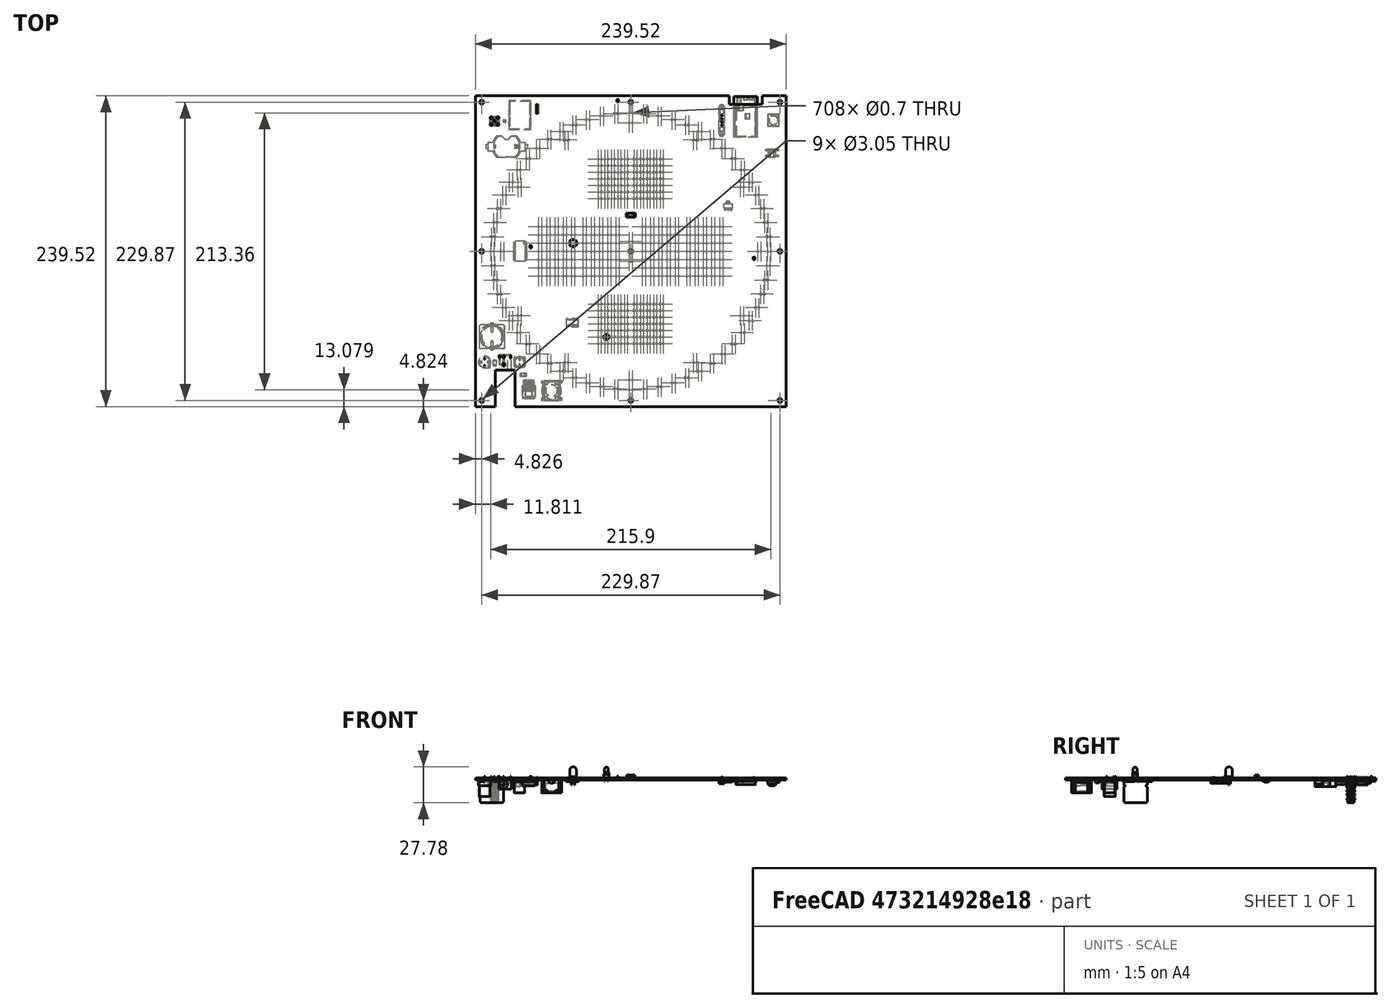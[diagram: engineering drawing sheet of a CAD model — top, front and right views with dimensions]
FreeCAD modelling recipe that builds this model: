
FCSTD DOCUMENT  (FreeCAD 0.20R29603 (Git))
Label: printed_circuit_board
License: All rights reserved
LicenseURL: http://en.wikipedia.org/wiki/All_rights_reserved
objects: App::Link×552, Part::Feature×29, App::Part×5, PartDesign::CoordinateSystem×1, Sketcher::SketchObject×1
note: 31 computed .brp shape members not serialized (recipe doc carries the construction recipe); baked Part::Feature solids carry a one-line shape summary decoded from their .brp

FEATURE [PartDesign::CoordinateSystem] Local_CS_7181
  AttacherType = Attacher::AttachEngine3D
  MapMode = 2
  Support = -> [X_Axis001]
FEATURE [Part::Feature] Pcb_7181
  Placement = pos=(-25.654,25.654,0) rot=(0,0,1;0rad)
  shape: bbox 239.5 x 239.5 x 1.6 mm, 770 faces (baked)
FEATURE [Sketcher::SketchObject] PCB_Sketch_7181
  FullyConstrained = false
  sketch-geometry (21):
    g0: LineSegment StartX=195.58 StartY=0 StartZ=0 EndX=0 EndY=0 EndZ=0
    g1: LineSegment StartX=239.522 StartY=-239.522 StartZ=0 EndX=239.522 EndY=0 EndZ=0
    g2: LineSegment StartX=0 StartY=-239.522 StartZ=0 EndX=15.24 EndY=-239.522 EndZ=0
    g3: LineSegment StartX=220.98 StartY=-6.604 StartZ=0 EndX=220.98 EndY=0 EndZ=0
    g4: LineSegment StartX=30.48 StartY=-239.522 StartZ=0 EndX=239.522 EndY=-239.522 EndZ=0
    g5: LineSegment StartX=30.48 StartY=-211.328 StartZ=0 EndX=30.48 EndY=-239.522 EndZ=0
    g6: LineSegment StartX=195.58 StartY=0 StartZ=0 EndX=195.58 EndY=-6.604 EndZ=0
    g7: LineSegment StartX=195.58 StartY=-6.604 StartZ=0 EndX=220.98 EndY=-6.604 EndZ=0
    g8: LineSegment StartX=15.24 StartY=-239.522 StartZ=0 EndX=15.24 EndY=-211.328 EndZ=0
    g9: LineSegment StartX=220.98 StartY=0 StartZ=0 EndX=239.522 EndY=0 EndZ=0
    g10: LineSegment StartX=0 StartY=0 StartZ=0 EndX=0 EndY=-239.522 EndZ=0
    g11: LineSegment StartX=15.24 StartY=-211.328 StartZ=0 EndX=30.48 EndY=-211.328 EndZ=0
    g12: Circle CenterX=234.696 CenterY=-119.761 CenterZ=0 NormalX=0 NormalY=0 NormalZ=1 AngleXU=0 Radius=1.524
    g13: Circle CenterX=234.696 CenterY=-234.696 CenterZ=0 NormalX=0 NormalY=0 NormalZ=1 AngleXU=0 Radius=1.524
    g14: Circle CenterX=4.826 CenterY=-4.826 CenterZ=0 NormalX=0 NormalY=0 NormalZ=1 AngleXU=0 Radius=1.524
    g15: Circle CenterX=234.696 CenterY=-4.826 CenterZ=0 NormalX=0 NormalY=0 NormalZ=1 AngleXU=0 Radius=1.524
    g16: Circle CenterX=119.761 CenterY=-234.696 CenterZ=0 NormalX=0 NormalY=0 NormalZ=1 AngleXU=0 Radius=1.524
    g17: Circle CenterX=119.761 CenterY=-4.826 CenterZ=0 NormalX=0 NormalY=0 NormalZ=1 AngleXU=0 Radius=1.524
    g18: Circle CenterX=119.761 CenterY=-119.761 CenterZ=0 NormalX=0 NormalY=0 NormalZ=1 AngleXU=0 Radius=1.524
    g19: Circle CenterX=4.826 CenterY=-119.761 CenterZ=0 NormalX=0 NormalY=0 NormalZ=1 AngleXU=0 Radius=1.524
    g20: Circle CenterX=4.826 CenterY=-234.696 CenterZ=0 NormalX=0 NormalY=0 NormalZ=1 AngleXU=0 Radius=1.524
  constraints (12):
    c: Coincident(g2,g10)
    c: Coincident(g0,g10)
    c: Coincident(g2,g8)
    c: Coincident(g8,g11)
    c: Coincident(g4,g5)
    c: Coincident(g5,g11)
    c: Coincident(g6,g7)
    c: Coincident(g0,g6)
    c: Coincident(g3,g7)
    c: Coincident(g3,g9)
    c: Coincident(g1,g4)
    c: Coincident(g1,g9)
FEATURE [App::Part] Board_Geoms_7181
  Group = -> [Pcb_7181,PCB_Sketch_7181]
  Origin = -> Origin
FEATURE [Part::Feature] Shape  label="${REFERENCE}_LED_D3.0mm_null"
  Placement = pos=(99.695,-185.801,0) rot=(0,0,1;0rad)
  shape: bbox 3.4 x 3.8 x 10.8 mm, 16 faces (baked)
FEATURE [Part::Feature] Shape001  label="${REFERENCE}_Body_null[2]"
  Placement = pos=(100.965,-185.801,0) rot=(0,0,1;0rad)
  shape: bbox 4 x 4 x 3 mm, 17 faces (baked)
FEATURE [App::Link] __REFERENCE__LED_D3_0mm_null_ln_  label="${REFERENCE}_LED_D3.0mm_null001"
  LinkPlacement = pos=(122.047,-190.881,0) rot=(0,0,1;0rad)
  LinkedObject = -> Shape
  Placement = pos=(122.047,-190.881,0) rot=(0,0,1;0rad)
FEATURE [App::Link] __REFERENCE__Body_null_2__ln_  label="${REFERENCE}_Body_null[2]001"
  LinkPlacement = pos=(123.317,-190.881,0) rot=(0,0,1;0rad)
  LinkedObject = -> Shape001
  Placement = pos=(123.317,-190.881,0) rot=(0,0,1;0rad)
FEATURE [Part::Feature] Shape002  label="${REFERENCE}_LED_D5.0mm_null"
  Placement = pos=(74.041,-113.411,-3) rot=(0,0,1;0rad)
  shape: bbox 5.4 x 5.8 x 14.1 mm, 16 faces (baked)
FEATURE [App::Link] __REFERENCE__LED_D5_0mm_null_ln_  label="${REFERENCE}_LED_D5.0mm_null001"
  LinkPlacement = pos=(55.7861,-33.4551,-3) rot=(0,0,1;0rad)
  LinkedObject = -> Shape002
  Placement = pos=(55.7861,-33.4551,-3) rot=(0,0,1;0rad)
FEATURE [App::Link] __REFERENCE__LED_D5_0mm_null_ln_001  label="${REFERENCE}_LED_D5.0mm_null002"
  LinkPlacement = pos=(147.701,-132.461,-3) rot=(0,0,1;0rad)
  LinkedObject = -> Shape002
  Placement = pos=(147.701,-132.461,-3) rot=(0,0,1;0rad)
FEATURE [App::Link] __REFERENCE__LED_D5_0mm_null_ln_002  label="${REFERENCE}_LED_D5.0mm_null003"
  LinkPlacement = pos=(11.811,-119.761,-3) rot=(0,0,1;0rad)
  LinkedObject = -> Shape002
  Placement = pos=(11.811,-119.761,-3) rot=(0,0,1;0rad)
FEATURE [App::Link] __REFERENCE__LED_D5_0mm_null_ln_003  label="${REFERENCE}_LED_D5.0mm_null004"
  LinkPlacement = pos=(168.021,-205.549,-3) rot=(0,0,1;0rad)
  LinkedObject = -> Shape002
  Placement = pos=(168.021,-205.549,-3) rot=(0,0,1;0rad)
FEATURE [App::Link] __REFERENCE__LED_D5_0mm_null_ln_004  label="${REFERENCE}_LED_D5.0mm_null005"
  LinkPlacement = pos=(118.491,-226.441,-3) rot=(0,0,1;0rad)
  LinkedObject = -> Shape002
  Placement = pos=(118.491,-226.441,-3) rot=(0,0,1;0rad)
FEATURE [App::Link] __REFERENCE__LED_D5_0mm_null_ln_005  label="${REFERENCE}_LED_D5.0mm_null006"
  LinkPlacement = pos=(95.631,-138.811,-3) rot=(0,0,1;0rad)
  LinkedObject = -> Shape002
  Placement = pos=(95.631,-138.811,-3) rot=(0,0,1;0rad)
FEATURE [App::Link] __REFERENCE__LED_D5_0mm_null_ln_006  label="${REFERENCE}_LED_D5.0mm_null007"
  LinkPlacement = pos=(82.931,-107.061,-3) rot=(0,0,1;0rad)
  LinkedObject = -> Shape002
  Placement = pos=(82.931,-107.061,-3) rot=(0,0,1;0rad)
FEATURE [App::Link] __REFERENCE__LED_D5_0mm_null_ln_007  label="${REFERENCE}_LED_D5.0mm_null008"
  LinkPlacement = pos=(118.491,-112.141,-3) rot=(0,0,1;0rad)
  LinkedObject = -> Shape002
  Placement = pos=(118.491,-112.141,-3) rot=(0,0,1;0rad)
FEATURE [App::Link] __REFERENCE__LED_D5_0mm_null_ln_008  label="${REFERENCE}_LED_D5.0mm_null009"
  LinkPlacement = pos=(54.991,-132.461,-3) rot=(0,0,1;0rad)
  LinkedObject = -> Shape002
  Placement = pos=(54.991,-132.461,-3) rot=(0,0,1;0rad)
FEATURE [App::Link] __REFERENCE__LED_D3_0mm_null_ln_001  label="${REFERENCE}_LED_D3.0mm_null002"
  LinkPlacement = pos=(109.855,-180.721,0) rot=(0,0,1;0rad)
  LinkedObject = -> Shape
  Placement = pos=(109.855,-180.721,0) rot=(0,0,1;0rad)
FEATURE [App::Link] __REFERENCE__Body_null_2__ln_001  label="${REFERENCE}_Body_null[2]002"
  LinkPlacement = pos=(111.125,-180.721,0) rot=(0,0,1;0rad)
  LinkedObject = -> Shape001
  Placement = pos=(111.125,-180.721,0) rot=(0,0,1;0rad)
FEATURE [App::Link] __REFERENCE__LED_D5_0mm_null_ln_009  label="${REFERENCE}_LED_D5.0mm_null010"
  LinkPlacement = pos=(161.882,-217.218,-3) rot=(0,0,1;0rad)
  LinkedObject = -> Shape002
  Placement = pos=(161.882,-217.218,-3) rot=(0,0,1;0rad)
FEATURE [App::Link] __REFERENCE__LED_D5_0mm_null_ln_010  label="${REFERENCE}_LED_D5.0mm_null011"
  LinkPlacement = pos=(82.931,-126.111,-3) rot=(0,0,1;0rad)
  LinkedObject = -> Shape002
  Placement = pos=(82.931,-126.111,-3) rot=(0,0,1;0rad)
FEATURE [App::Link] __REFERENCE__LED_D3_0mm_null_ln_002  label="${REFERENCE}_LED_D3.0mm_null003"
  LinkPlacement = pos=(137.287,-53.721,0) rot=(0,0,1;0rad)
  LinkedObject = -> Shape
  Placement = pos=(137.287,-53.721,0) rot=(0,0,1;0rad)
FEATURE [App::Link] __REFERENCE__Body_null_2__ln_002  label="${REFERENCE}_Body_null[2]003"
  LinkPlacement = pos=(138.557,-53.721,0) rot=(0,0,1;0rad)
  LinkedObject = -> Shape001
  Placement = pos=(138.557,-53.721,0) rot=(0,0,1;0rad)
FEATURE [App::Link] __REFERENCE__LED_D3_0mm_null_ln_003  label="${REFERENCE}_LED_D3.0mm_null004"
  LinkPlacement = pos=(99.695,-63.881,0) rot=(0,0,1;0rad)
  LinkedObject = -> Shape
  Placement = pos=(99.695,-63.881,0) rot=(0,0,1;0rad)
FEATURE [App::Link] __REFERENCE__Body_null_2__ln_003  label="${REFERENCE}_Body_null[2]004"
  LinkPlacement = pos=(100.965,-63.881,0) rot=(0,0,1;0rad)
  LinkedObject = -> Shape001
  Placement = pos=(100.965,-63.881,0) rot=(0,0,1;0rad)
FEATURE [App::Link] __REFERENCE__LED_D5_0mm_null_ln_011  label="${REFERENCE}_LED_D5.0mm_null012"
  LinkPlacement = pos=(82.931,-113.411,-3) rot=(0,0,1;0rad)
  LinkedObject = -> Shape002
  Placement = pos=(82.931,-113.411,-3) rot=(0,0,1;0rad)
FEATURE [App::Link] __REFERENCE__LED_D5_0mm_null_ln_012  label="${REFERENCE}_LED_D5.0mm_null013"
  LinkPlacement = pos=(67.691,-132.461,-3) rot=(0,0,1;0rad)
  LinkedObject = -> Shape002
  Placement = pos=(67.691,-132.461,-3) rot=(0,0,1;0rad)
FEATURE [App::Link] __REFERENCE__LED_D5_0mm_null_ln_013  label="${REFERENCE}_LED_D5.0mm_null014"
  LinkPlacement = pos=(181.991,-100.711,-3) rot=(0,0,1;0rad)
  LinkedObject = -> Shape002
  Placement = pos=(181.991,-100.711,-3) rot=(0,0,1;0rad)
FEATURE [App::Link] __REFERENCE__LED_D5_0mm_null_ln_014  label="${REFERENCE}_LED_D5.0mm_null015"
  LinkPlacement = pos=(154.051,-138.811,-3) rot=(0,0,1;0rad)
  LinkedObject = -> Shape002
  Placement = pos=(154.051,-138.811,-3) rot=(0,0,1;0rad)
FEATURE [App::Link] __REFERENCE__LED_D5_0mm_null_ln_015  label="${REFERENCE}_LED_D5.0mm_null016"
  LinkPlacement = pos=(82.931,-119.761,-3) rot=(0,0,1;0rad)
  LinkedObject = -> Shape002
  Placement = pos=(82.931,-119.761,-3) rot=(0,0,1;0rad)
FEATURE [App::Link] __REFERENCE__LED_D5_0mm_null_ln_016  label="${REFERENCE}_LED_D5.0mm_null017"
  LinkPlacement = pos=(129.642,-13.6654,-3) rot=(0,0,1;0rad)
  LinkedObject = -> Shape002
  Placement = pos=(129.642,-13.6654,-3) rot=(0,0,1;0rad)
FEATURE [Part::Feature] Shape003  label="${REFERENCE}_R_0805_2012Metric_null"
  Placement = pos=(214.757,-125.222,0) rot=(0,0,1;1.5708rad)
  shape: bbox 1.2 x 2 x 0.45 mm, 26 faces (baked)
FEATURE [App::Link] __REFERENCE__LED_D5_0mm_null_ln_017  label="${REFERENCE}_LED_D5.0mm_null018"
  LinkPlacement = pos=(108.331,-113.411,-3) rot=(0,0,1;0rad)
  LinkedObject = -> Shape002
  Placement = pos=(108.331,-113.411,-3) rot=(0,0,1;0rad)
FEATURE [App::Link] __REFERENCE__LED_D5_0mm_null_ln_018  label="${REFERENCE}_LED_D5.0mm_null019"
  LinkPlacement = pos=(108.331,-119.761,-3) rot=(0,0,1;0rad)
  LinkedObject = -> Shape002
  Placement = pos=(108.331,-119.761,-3) rot=(0,0,1;0rad)
FEATURE [App::Link] __REFERENCE__LED_D5_0mm_null_ln_019  label="${REFERENCE}_LED_D5.0mm_null020"
  LinkPlacement = pos=(54.991,-113.411,-3) rot=(0,0,1;0rad)
  LinkedObject = -> Shape002
  Placement = pos=(54.991,-113.411,-3) rot=(0,0,1;0rad)
FEATURE [App::Link] __REFERENCE__LED_D3_0mm_null_ln_004  label="${REFERENCE}_LED_D3.0mm_null005"
  LinkPlacement = pos=(127.127,-58.801,0) rot=(0,0,1;0rad)
  LinkedObject = -> Shape
  Placement = pos=(127.127,-58.801,0) rot=(0,0,1;0rad)
FEATURE [App::Link] __REFERENCE__Body_null_2__ln_004  label="${REFERENCE}_Body_null[2]005"
  LinkPlacement = pos=(128.397,-58.801,0) rot=(0,0,1;0rad)
  LinkedObject = -> Shape001
  Placement = pos=(128.397,-58.801,0) rot=(0,0,1;0rad)
FEATURE [App::Link] __REFERENCE__LED_D5_0mm_null_ln_020  label="${REFERENCE}_LED_D5.0mm_null021"
  LinkPlacement = pos=(21.034,-163.152,-3) rot=(0,0,1;0rad)
  LinkedObject = -> Shape002
  Placement = pos=(21.034,-163.152,-3) rot=(0,0,1;0rad)
FEATURE [App::Link] __REFERENCE__LED_D3_0mm_null_ln_005  label="${REFERENCE}_LED_D3.0mm_null006"
  LinkPlacement = pos=(109.855,-74.041,0) rot=(0,0,1;0rad)
  LinkedObject = -> Shape
  Placement = pos=(109.855,-74.041,0) rot=(0,0,1;0rad)
FEATURE [App::Link] __REFERENCE__Body_null_2__ln_005  label="${REFERENCE}_Body_null[2]006"
  LinkPlacement = pos=(111.125,-74.041,0) rot=(0,0,1;0rad)
  LinkedObject = -> Shape001
  Placement = pos=(111.125,-74.041,0) rot=(0,0,1;0rad)
FEATURE [App::Link] __REFERENCE__LED_D5_0mm_null_ln_021  label="${REFERENCE}_LED_D5.0mm_null022"
  LinkPlacement = pos=(108.331,-132.461,-3) rot=(0,0,1;0rad)
  LinkedObject = -> Shape002
  Placement = pos=(108.331,-132.461,-3) rot=(0,0,1;0rad)
FEATURE [App::Link] __REFERENCE__LED_D3_0mm_null_ln_006  label="${REFERENCE}_LED_D3.0mm_null007"
  LinkPlacement = pos=(104.775,-79.121,0) rot=(0,0,1;0rad)
  LinkedObject = -> Shape
  Placement = pos=(104.775,-79.121,0) rot=(0,0,1;0rad)
FEATURE [App::Link] __REFERENCE__Body_null_2__ln_006  label="${REFERENCE}_Body_null[2]007"
  LinkPlacement = pos=(106.045,-79.121,0) rot=(0,0,1;0rad)
  LinkedObject = -> Shape001
  Placement = pos=(106.045,-79.121,0) rot=(0,0,1;0rad)
FEATURE [App::Link] __REFERENCE__LED_D3_0mm_null_ln_007  label="${REFERENCE}_LED_D3.0mm_null008"
  LinkPlacement = pos=(94.615,-48.641,0) rot=(0,0,1;0rad)
  LinkedObject = -> Shape
  Placement = pos=(94.615,-48.641,0) rot=(0,0,1;0rad)
FEATURE [App::Link] __REFERENCE__Body_null_2__ln_007  label="${REFERENCE}_Body_null[2]008"
  LinkPlacement = pos=(95.885,-48.641,0) rot=(0,0,1;0rad)
  LinkedObject = -> Shape001
  Placement = pos=(95.885,-48.641,0) rot=(0,0,1;0rad)
FEATURE [App::Link] __REFERENCE__LED_D3_0mm_null_ln_008  label="${REFERENCE}_LED_D3.0mm_null009"
  LinkPlacement = pos=(94.615,-190.881,0) rot=(0,0,1;0rad)
  LinkedObject = -> Shape
  Placement = pos=(94.615,-190.881,0) rot=(0,0,1;0rad)
FEATURE [App::Link] __REFERENCE__Body_null_2__ln_008  label="${REFERENCE}_Body_null[2]009"
  LinkPlacement = pos=(95.885,-190.881,0) rot=(0,0,1;0rad)
  LinkedObject = -> Shape001
  Placement = pos=(95.885,-190.881,0) rot=(0,0,1;0rad)
FEATURE [App::Link] __REFERENCE__LED_D5_0mm_null_ln_022  label="${REFERENCE}_LED_D5.0mm_null023"
  LinkPlacement = pos=(96.311,-15.4122,-3) rot=(0,0,1;0rad)
  LinkedObject = -> Shape002
  Placement = pos=(96.311,-15.4122,-3) rot=(0,0,1;0rad)
FEATURE [App::Link] __REFERENCE__LED_D5_0mm_null_ln_023  label="${REFERENCE}_LED_D5.0mm_null024"
  LinkPlacement = pos=(32.1851,-182.466,-3) rot=(0,0,1;0rad)
  LinkedObject = -> Shape002
  Placement = pos=(32.1851,-182.466,-3) rot=(0,0,1;0rad)
FEATURE [App::Link] __REFERENCE__LED_D5_0mm_null_ln_024  label="${REFERENCE}_LED_D5.0mm_null025"
  LinkPlacement = pos=(128.651,-100.711,-3) rot=(0,0,1;0rad)
  LinkedObject = -> Shape002
  Placement = pos=(128.651,-100.711,-3) rot=(0,0,1;0rad)
FEATURE [App::Link] __REFERENCE__LED_D5_0mm_null_ln_025  label="${REFERENCE}_LED_D5.0mm_null026"
  LinkPlacement = pos=(140.671,-224.11,-3) rot=(0,0,1;0rad)
  LinkedObject = -> Shape002
  Placement = pos=(140.671,-224.11,-3) rot=(0,0,1;0rad)
FEATURE [App::Link] __REFERENCE__LED_D3_0mm_null_ln_009  label="${REFERENCE}_LED_D3.0mm_null010"
  LinkPlacement = pos=(99.695,-53.721,0) rot=(0,0,1;0rad)
  LinkedObject = -> Shape
  Placement = pos=(99.695,-53.721,0) rot=(0,0,1;0rad)
FEATURE [App::Link] __REFERENCE__Body_null_2__ln_009  label="${REFERENCE}_Body_null[2]010"
  LinkPlacement = pos=(100.965,-53.721,0) rot=(0,0,1;0rad)
  LinkedObject = -> Shape001
  Placement = pos=(100.965,-53.721,0) rot=(0,0,1;0rad)
FEATURE [App::Link] __REFERENCE__LED_D3_0mm_null_ln_010  label="${REFERENCE}_LED_D3.0mm_null011"
  LinkPlacement = pos=(132.207,-175.641,0) rot=(0,0,1;0rad)
  LinkedObject = -> Shape
  Placement = pos=(132.207,-175.641,0) rot=(0,0,1;0rad)
FEATURE [App::Link] __REFERENCE__Body_null_2__ln_010  label="${REFERENCE}_Body_null[2]011"
  LinkPlacement = pos=(133.477,-175.641,0) rot=(0,0,1;0rad)
  LinkedObject = -> Shape001
  Placement = pos=(133.477,-175.641,0) rot=(0,0,1;0rad)
FEATURE [App::Link] __REFERENCE__LED_D5_0mm_null_ln_026  label="${REFERENCE}_LED_D5.0mm_null027"
  LinkPlacement = pos=(89.281,-132.461,-3) rot=(0,0,1;0rad)
  LinkedObject = -> Shape002
  Placement = pos=(89.281,-132.461,-3) rot=(0,0,1;0rad)
FEATURE [App::Link] __REFERENCE__LED_D5_0mm_null_ln_027  label="${REFERENCE}_LED_D5.0mm_null028"
  LinkPlacement = pos=(55.7861,-206.067,-3) rot=(0,0,1;0rad)
  LinkedObject = -> Shape002
  Placement = pos=(55.7861,-206.067,-3) rot=(0,0,1;0rad)
FEATURE [App::Link] __REFERENCE__LED_D3_0mm_null_ln_011  label="${REFERENCE}_LED_D3.0mm_null012"
  LinkPlacement = pos=(122.047,-79.121,0) rot=(0,0,1;0rad)
  LinkedObject = -> Shape
  Placement = pos=(122.047,-79.121,0) rot=(0,0,1;0rad)
FEATURE [App::Link] __REFERENCE__Body_null_2__ln_011  label="${REFERENCE}_Body_null[2]012"
  LinkPlacement = pos=(123.317,-79.121,0) rot=(0,0,1;0rad)
  LinkedObject = -> Shape001
  Placement = pos=(123.317,-79.121,0) rot=(0,0,1;0rad)
FEATURE [App::Link] __REFERENCE__LED_D5_0mm_null_ln_028  label="${REFERENCE}_LED_D5.0mm_null029"
  LinkPlacement = pos=(67.691,-100.711,-3) rot=(0,0,1;0rad)
  LinkedObject = -> Shape002
  Placement = pos=(67.691,-100.711,-3) rot=(0,0,1;0rad)
FEATURE [App::Link] __REFERENCE__LED_D5_0mm_null_ln_029  label="${REFERENCE}_LED_D5.0mm_null030"
  LinkPlacement = pos=(54.991,-100.711,-3) rot=(0,0,1;0rad)
  LinkedObject = -> Shape002
  Placement = pos=(54.991,-100.711,-3) rot=(0,0,1;0rad)
FEATURE [App::Link] __REFERENCE__LED_D5_0mm_null_ln_030  label="${REFERENCE}_LED_D5.0mm_null031"
  LinkPlacement = pos=(89.281,-113.411,-3) rot=(0,0,1;0rad)
  LinkedObject = -> Shape002
  Placement = pos=(89.281,-113.411,-3) rot=(0,0,1;0rad)
FEATURE [App::Link] __REFERENCE__LED_D3_0mm_null_ln_012  label="${REFERENCE}_LED_D3.0mm_null013"
  LinkPlacement = pos=(142.367,-160.401,0) rot=(0,0,1;0rad)
  LinkedObject = -> Shape
  Placement = pos=(142.367,-160.401,0) rot=(0,0,1;0rad)
FEATURE [App::Link] __REFERENCE__Body_null_2__ln_012  label="${REFERENCE}_Body_null[2]013"
  LinkPlacement = pos=(143.637,-160.401,0) rot=(0,0,1;0rad)
  LinkedObject = -> Shape001
  Placement = pos=(143.637,-160.401,0) rot=(0,0,1;0rad)
FEATURE [Part::Feature] Shape004  label="${REFERENCE}_C_0805_2012Metric_null"
  Placement = pos=(42.545,-116.332,0) rot=(0,0,-1;1.5708rad)
  shape: bbox 1.25 x 2 x 1.25 mm, 28 faces (baked)
FEATURE [App::Link] __REFERENCE__LED_D5_0mm_null_ln_031  label="${REFERENCE}_LED_D5.0mm_null032"
  LinkPlacement = pos=(95.631,-126.111,-3) rot=(0,0,1;0rad)
  LinkedObject = -> Shape002
  Placement = pos=(95.631,-126.111,-3) rot=(0,0,1;0rad)
FEATURE [App::Link] __REFERENCE__LED_D3_0mm_null_ln_013  label="${REFERENCE}_LED_D3.0mm_null014"
  LinkPlacement = pos=(142.367,-170.561,0) rot=(0,0,1;0rad)
  LinkedObject = -> Shape
  Placement = pos=(142.367,-170.561,0) rot=(0,0,1;0rad)
FEATURE [App::Link] __REFERENCE__Body_null_2__ln_013  label="${REFERENCE}_Body_null[2]014"
  LinkPlacement = pos=(143.637,-170.561,0) rot=(0,0,1;0rad)
  LinkedObject = -> Shape001
  Placement = pos=(143.637,-170.561,0) rot=(0,0,1;0rad)
FEATURE [App::Link] __REFERENCE__LED_D3_0mm_null_ln_014  label="${REFERENCE}_LED_D3.0mm_null015"
  LinkPlacement = pos=(94.615,-53.721,0) rot=(0,0,1;0rad)
  LinkedObject = -> Shape
  Placement = pos=(94.615,-53.721,0) rot=(0,0,1;0rad)
FEATURE [App::Link] __REFERENCE__Body_null_2__ln_014  label="${REFERENCE}_Body_null[2]015"
  LinkPlacement = pos=(95.885,-53.721,0) rot=(0,0,1;0rad)
  LinkedObject = -> Shape001
  Placement = pos=(95.885,-53.721,0) rot=(0,0,1;0rad)
FEATURE [App::Link] __REFERENCE__LED_D5_0mm_null_ln_032  label="${REFERENCE}_LED_D5.0mm_null033"
  LinkPlacement = pos=(12.3954,-108.61,-3) rot=(0,0,1;0rad)
  LinkedObject = -> Shape002
  Placement = pos=(12.3954,-108.61,-3) rot=(0,0,1;0rad)
FEATURE [App::Link] __REFERENCE__LED_D5_0mm_null_ln_033  label="${REFERENCE}_LED_D5.0mm_null034"
  LinkPlacement = pos=(54.991,-119.761,-3) rot=(0,0,1;0rad)
  LinkedObject = -> Shape002
  Placement = pos=(54.991,-119.761,-3) rot=(0,0,1;0rad)
FEATURE [App::Link] __REFERENCE__LED_D5_0mm_null_ln_034  label="${REFERENCE}_LED_D5.0mm_null035"
  LinkPlacement = pos=(154.051,-107.061,-3) rot=(0,0,1;0rad)
  LinkedObject = -> Shape002
  Placement = pos=(154.051,-107.061,-3) rot=(0,0,1;0rad)
FEATURE [App::Link] __REFERENCE__LED_D3_0mm_null_ln_015  label="${REFERENCE}_LED_D3.0mm_null016"
  LinkPlacement = pos=(94.615,-63.881,0) rot=(0,0,1;0rad)
  LinkedObject = -> Shape
  Placement = pos=(94.615,-63.881,0) rot=(0,0,1;0rad)
FEATURE [App::Link] __REFERENCE__Body_null_2__ln_015  label="${REFERENCE}_Body_null[2]016"
  LinkPlacement = pos=(95.885,-63.881,0) rot=(0,0,1;0rad)
  LinkedObject = -> Shape001
  Placement = pos=(95.885,-63.881,0) rot=(0,0,1;0rad)
FEATURE [App::Link] __REFERENCE__LED_D3_0mm_null_ln_016  label="${REFERENCE}_LED_D3.0mm_null017"
  LinkPlacement = pos=(122.047,-48.641,0) rot=(0,0,1;0rad)
  LinkedObject = -> Shape
  Placement = pos=(122.047,-48.641,0) rot=(0,0,1;0rad)
FEATURE [App::Link] __REFERENCE__Body_null_2__ln_016  label="${REFERENCE}_Body_null[2]017"
  LinkPlacement = pos=(123.317,-48.641,0) rot=(0,0,1;0rad)
  LinkedObject = -> Shape001
  Placement = pos=(123.317,-48.641,0) rot=(0,0,1;0rad)
FEATURE [App::Link] __REFERENCE__LED_D5_0mm_null_ln_035  label="${REFERENCE}_LED_D5.0mm_null036"
  LinkPlacement = pos=(161.882,-22.304,-3) rot=(0,0,1;0rad)
  LinkedObject = -> Shape002
  Placement = pos=(161.882,-22.304,-3) rot=(0,0,1;0rad)
FEATURE [App::Link] __REFERENCE__LED_D3_0mm_null_ln_017  label="${REFERENCE}_LED_D3.0mm_null018"
  LinkPlacement = pos=(132.207,-53.721,0) rot=(0,0,1;0rad)
  LinkedObject = -> Shape
  Placement = pos=(132.207,-53.721,0) rot=(0,0,1;0rad)
FEATURE [App::Link] __REFERENCE__Body_null_2__ln_017  label="${REFERENCE}_Body_null[2]018"
  LinkPlacement = pos=(133.477,-53.721,0) rot=(0,0,1;0rad)
  LinkedObject = -> Shape001
  Placement = pos=(133.477,-53.721,0) rot=(0,0,1;0rad)
FEATURE [App::Link] __REFERENCE__LED_D3_0mm_null_ln_018  label="${REFERENCE}_LED_D3.0mm_null019"
  LinkPlacement = pos=(114.935,-58.801,0) rot=(0,0,1;0rad)
  LinkedObject = -> Shape
  Placement = pos=(114.935,-58.801,0) rot=(0,0,1;0rad)
FEATURE [App::Link] __REFERENCE__Body_null_2__ln_018  label="${REFERENCE}_Body_null[2]019"
  LinkPlacement = pos=(116.205,-58.801,0) rot=(0,0,1;0rad)
  LinkedObject = -> Shape001
  Placement = pos=(116.205,-58.801,0) rot=(0,0,1;0rad)
FEATURE [App::Link] __REFERENCE__LED_D5_0mm_null_ln_036  label="${REFERENCE}_LED_D5.0mm_null037"
  LinkPlacement = pos=(26.1034,-173.101,-3) rot=(0,0,1;0rad)
  LinkedObject = -> Shape002
  Placement = pos=(26.1034,-173.101,-3) rot=(0,0,1;0rad)
FEATURE [App::Link] __REFERENCE__LED_D3_0mm_null_ln_019  label="${REFERENCE}_LED_D3.0mm_null020"
  LinkPlacement = pos=(94.615,-170.561,0) rot=(0,0,1;0rad)
  LinkedObject = -> Shape
  Placement = pos=(94.615,-170.561,0) rot=(0,0,1;0rad)
FEATURE [App::Link] __REFERENCE__Body_null_2__ln_019  label="${REFERENCE}_Body_null[2]020"
  LinkPlacement = pos=(95.885,-170.561,0) rot=(0,0,1;0rad)
  LinkedObject = -> Shape001
  Placement = pos=(95.885,-170.561,0) rot=(0,0,1;0rad)
FEATURE [App::Link] __REFERENCE__R_0805_2012Metric_null_ln_  label="${REFERENCE}_R_0805_2012Metric_null001"
  LinkPlacement = pos=(212.471,-125.222,0) rot=(0,0,-1;1.5708rad)
  LinkedObject = -> Shape003
  Placement = pos=(212.471,-125.222,0) rot=(0,0,-1;1.5708rad)
FEATURE [App::Link] __REFERENCE__LED_D3_0mm_null_ln_020  label="${REFERENCE}_LED_D3.0mm_null021"
  LinkPlacement = pos=(142.367,-58.801,0) rot=(0,0,1;0rad)
  LinkedObject = -> Shape
  Placement = pos=(142.367,-58.801,0) rot=(0,0,1;0rad)
FEATURE [App::Link] __REFERENCE__Body_null_2__ln_020  label="${REFERENCE}_Body_null[2]021"
  LinkPlacement = pos=(143.637,-58.801,0) rot=(0,0,1;0rad)
  LinkedObject = -> Shape001
  Placement = pos=(143.637,-58.801,0) rot=(0,0,1;0rad)
FEATURE [App::Link] __REFERENCE__R_0805_2012Metric_null_ln_001  label="${REFERENCE}_R_0805_2012Metric_null002"
  LinkPlacement = pos=(212.09,-19.558,0) rot=(0,0,1;1.5708rad)
  LinkedObject = -> Shape003
  Placement = pos=(212.09,-19.558,0) rot=(0,0,1;1.5708rad)
FEATURE [App::Link] __REFERENCE__LED_D5_0mm_null_ln_037  label="${REFERENCE}_LED_D5.0mm_null038"
  LinkPlacement = pos=(175.641,-100.711,-3) rot=(0,0,1;0rad)
  LinkedObject = -> Shape002
  Placement = pos=(175.641,-100.711,-3) rot=(0,0,1;0rad)
FEATURE [App::Link] __REFERENCE__LED_D5_0mm_null_ln_038  label="${REFERENCE}_LED_D5.0mm_null039"
  LinkPlacement = pos=(48.641,-138.811,-3) rot=(0,0,1;0rad)
  LinkedObject = -> Shape002
  Placement = pos=(48.641,-138.811,-3) rot=(0,0,1;0rad)
FEATURE [App::Link] __REFERENCE__LED_D5_0mm_null_ln_039  label="${REFERENCE}_LED_D5.0mm_null040"
  LinkPlacement = pos=(129.642,-225.857,-3) rot=(0,0,1;0rad)
  LinkedObject = -> Shape002
  Placement = pos=(129.642,-225.857,-3) rot=(0,0,1;0rad)
FEATURE [App::Link] __REFERENCE__LED_D5_0mm_null_ln_040  label="${REFERENCE}_LED_D5.0mm_null041"
  LinkPlacement = pos=(82.931,-138.811,-3) rot=(0,0,1;0rad)
  LinkedObject = -> Shape002
  Placement = pos=(82.931,-138.811,-3) rot=(0,0,1;0rad)
FEATURE [App::Link] __REFERENCE__LED_D3_0mm_null_ln_021  label="${REFERENCE}_LED_D3.0mm_null022"
  LinkPlacement = pos=(137.287,-79.121,0) rot=(0,0,1;0rad)
  LinkedObject = -> Shape
  Placement = pos=(137.287,-79.121,0) rot=(0,0,1;0rad)
FEATURE [App::Link] __REFERENCE__Body_null_2__ln_021  label="${REFERENCE}_Body_null[2]022"
  LinkPlacement = pos=(138.557,-79.121,0) rot=(0,0,1;0rad)
  LinkedObject = -> Shape001
  Placement = pos=(138.557,-79.121,0) rot=(0,0,1;0rad)
FEATURE [App::Link] __REFERENCE__LED_D5_0mm_null_ln_041  label="${REFERENCE}_LED_D5.0mm_null042"
  LinkPlacement = pos=(181.991,-138.811,-3) rot=(0,0,1;0rad)
  LinkedObject = -> Shape002
  Placement = pos=(181.991,-138.811,-3) rot=(0,0,1;0rad)
FEATURE [App::Link] __REFERENCE__LED_D5_0mm_null_ln_042  label="${REFERENCE}_LED_D5.0mm_null043"
  LinkPlacement = pos=(210.879,-173.101,-3) rot=(0,0,1;0rad)
  LinkedObject = -> Shape002
  Placement = pos=(210.879,-173.101,-3) rot=(0,0,1;0rad)
FEATURE [App::Link] __REFERENCE__LED_D5_0mm_null_ln_043  label="${REFERENCE}_LED_D5.0mm_null044"
  LinkPlacement = pos=(108.331,-100.711,-3) rot=(0,0,1;0rad)
  LinkedObject = -> Shape002
  Placement = pos=(108.331,-100.711,-3) rot=(0,0,1;0rad)
FEATURE [App::Link] __REFERENCE__LED_D3_0mm_null_ln_022  label="${REFERENCE}_LED_D3.0mm_null023"
  LinkPlacement = pos=(109.855,-185.801,0) rot=(0,0,1;0rad)
  LinkedObject = -> Shape
  Placement = pos=(109.855,-185.801,0) rot=(0,0,1;0rad)
FEATURE [App::Link] __REFERENCE__Body_null_2__ln_022  label="${REFERENCE}_Body_null[2]023"
  LinkPlacement = pos=(111.125,-185.801,0) rot=(0,0,1;0rad)
  LinkedObject = -> Shape001
  Placement = pos=(111.125,-185.801,0) rot=(0,0,1;0rad)
FEATURE [App::Link] __REFERENCE__LED_D3_0mm_null_ln_023  label="${REFERENCE}_LED_D3.0mm_null024"
  LinkPlacement = pos=(109.855,-53.721,0) rot=(0,0,1;0rad)
  LinkedObject = -> Shape
  Placement = pos=(109.855,-53.721,0) rot=(0,0,1;0rad)
FEATURE [App::Link] __REFERENCE__Body_null_2__ln_023  label="${REFERENCE}_Body_null[2]024"
  LinkPlacement = pos=(111.125,-53.721,0) rot=(0,0,1;0rad)
  LinkedObject = -> Shape001
  Placement = pos=(111.125,-53.721,0) rot=(0,0,1;0rad)
FEATURE [App::Link] __REFERENCE__LED_D5_0mm_null_ln_044  label="${REFERENCE}_LED_D5.0mm_null045"
  LinkPlacement = pos=(61.341,-126.111,-3) rot=(0,0,1;0rad)
  LinkedObject = -> Shape002
  Placement = pos=(61.341,-126.111,-3) rot=(0,0,1;0rad)
FEATURE [App::Link] __REFERENCE__LED_D5_0mm_null_ln_045  label="${REFERENCE}_LED_D5.0mm_null046"
  LinkPlacement = pos=(141.351,-138.811,-3) rot=(0,0,1;0rad)
  LinkedObject = -> Shape002
  Placement = pos=(141.351,-138.811,-3) rot=(0,0,1;0rad)
FEATURE [App::Link] __REFERENCE__R_0805_2012Metric_null_ln_002  label="${REFERENCE}_R_0805_2012Metric_null003"
  LinkPlacement = pos=(160.274,-169.672,0) rot=(0,0,1;3.14159rad)
  LinkedObject = -> Shape003
  Placement = pos=(160.274,-169.672,0) rot=(0,0,1;3.14159rad)
FEATURE [App::Link] __REFERENCE__LED_D3_0mm_null_ln_024  label="${REFERENCE}_LED_D3.0mm_null025"
  LinkPlacement = pos=(104.775,-160.401,0) rot=(0,0,1;0rad)
  LinkedObject = -> Shape
  Placement = pos=(104.775,-160.401,0) rot=(0,0,1;0rad)
FEATURE [App::Link] __REFERENCE__Body_null_2__ln_024  label="${REFERENCE}_Body_null[2]025"
  LinkPlacement = pos=(106.045,-160.401,0) rot=(0,0,1;0rad)
  LinkedObject = -> Shape001
  Placement = pos=(106.045,-160.401,0) rot=(0,0,1;0rad)
FEATURE [App::Link] __REFERENCE__LED_D3_0mm_null_ln_025  label="${REFERENCE}_LED_D3.0mm_null026"
  LinkPlacement = pos=(132.207,-165.481,0) rot=(0,0,1;0rad)
  LinkedObject = -> Shape
  Placement = pos=(132.207,-165.481,0) rot=(0,0,1;0rad)
FEATURE [App::Link] __REFERENCE__Body_null_2__ln_025  label="${REFERENCE}_Body_null[2]026"
  LinkPlacement = pos=(133.477,-165.481,0) rot=(0,0,1;0rad)
  LinkedObject = -> Shape001
  Placement = pos=(133.477,-165.481,0) rot=(0,0,1;0rad)
FEATURE [App::Link] __REFERENCE__LED_D3_0mm_null_ln_026  label="${REFERENCE}_LED_D3.0mm_null027"
  LinkPlacement = pos=(132.207,-79.121,0) rot=(0,0,1;0rad)
  LinkedObject = -> Shape
  Placement = pos=(132.207,-79.121,0) rot=(0,0,1;0rad)
FEATURE [App::Link] __REFERENCE__Body_null_2__ln_026  label="${REFERENCE}_Body_null[2]027"
  LinkPlacement = pos=(133.477,-79.121,0) rot=(0,0,1;0rad)
  LinkedObject = -> Shape001
  Placement = pos=(133.477,-79.121,0) rot=(0,0,1;0rad)
FEATURE [App::Link] __REFERENCE__LED_D5_0mm_null_ln_046  label="${REFERENCE}_LED_D5.0mm_null047"
  LinkPlacement = pos=(204.797,-57.0561,-3) rot=(0,0,1;0rad)
  LinkedObject = -> Shape002
  Placement = pos=(204.797,-57.0561,-3) rot=(0,0,1;0rad)
FEATURE [App::Link] __REFERENCE__LED_D5_0mm_null_ln_047  label="${REFERENCE}_LED_D5.0mm_null048"
  LinkPlacement = pos=(19.431,-119.761,-3) rot=(0,0,1;0rad)
  LinkedObject = -> Shape002
  Placement = pos=(19.431,-119.761,-3) rot=(0,0,1;0rad)
FEATURE [App::Link] __REFERENCE__LED_D3_0mm_null_ln_027  label="${REFERENCE}_LED_D3.0mm_null028"
  LinkPlacement = pos=(94.615,-165.481,0) rot=(0,0,1;0rad)
  LinkedObject = -> Shape
  Placement = pos=(94.615,-165.481,0) rot=(0,0,1;0rad)
FEATURE [App::Link] __REFERENCE__Body_null_2__ln_027  label="${REFERENCE}_Body_null[2]028"
  LinkPlacement = pos=(95.885,-165.481,0) rot=(0,0,1;0rad)
  LinkedObject = -> Shape001
  Placement = pos=(95.885,-165.481,0) rot=(0,0,1;0rad)
FEATURE [App::Link] __REFERENCE__LED_D5_0mm_null_ln_048  label="${REFERENCE}_LED_D5.0mm_null049"
  LinkPlacement = pos=(210.879,-66.421,-3) rot=(0,0,1;0rad)
  LinkedObject = -> Shape002
  Placement = pos=(210.879,-66.421,-3) rot=(0,0,1;0rad)
FEATURE [App::Link] __REFERENCE__LED_D5_0mm_null_ln_049  label="${REFERENCE}_LED_D5.0mm_null050"
  LinkPlacement = pos=(169.291,-138.811,-3) rot=(0,0,1;0rad)
  LinkedObject = -> Shape002
  Placement = pos=(169.291,-138.811,-3) rot=(0,0,1;0rad)
FEATURE [App::Link] __REFERENCE__LED_D5_0mm_null_ln_050  label="${REFERENCE}_LED_D5.0mm_null051"
  LinkPlacement = pos=(197.77,-191.144,-3) rot=(0,0,1;0rad)
  LinkedObject = -> Shape002
  Placement = pos=(197.77,-191.144,-3) rot=(0,0,1;0rad)
FEATURE [App::Link] __REFERENCE__LED_D3_0mm_null_ln_028  label="${REFERENCE}_LED_D3.0mm_null029"
  LinkPlacement = pos=(137.287,-68.961,0) rot=(0,0,1;0rad)
  LinkedObject = -> Shape
  Placement = pos=(137.287,-68.961,0) rot=(0,0,1;0rad)
FEATURE [App::Link] __REFERENCE__Body_null_2__ln_028  label="${REFERENCE}_Body_null[2]029"
  LinkPlacement = pos=(138.557,-68.961,0) rot=(0,0,1;0rad)
  LinkedObject = -> Shape001
  Placement = pos=(138.557,-68.961,0) rot=(0,0,1;0rad)
FEATURE [App::Link] __REFERENCE__LED_D5_0mm_null_ln_051  label="${REFERENCE}_LED_D5.0mm_null052"
  LinkPlacement = pos=(118.491,-218.821,-3) rot=(0,0,1;0rad)
  LinkedObject = -> Shape002
  Placement = pos=(118.491,-218.821,-3) rot=(0,0,1;0rad)
FEATURE [App::Link] __REFERENCE__LED_D3_0mm_null_ln_029  label="${REFERENCE}_LED_D3.0mm_null030"
  LinkPlacement = pos=(104.775,-180.721,0) rot=(0,0,1;0rad)
  LinkedObject = -> Shape
  Placement = pos=(104.775,-180.721,0) rot=(0,0,1;0rad)
FEATURE [App::Link] __REFERENCE__Body_null_2__ln_029  label="${REFERENCE}_Body_null[2]030"
  LinkPlacement = pos=(106.045,-180.721,0) rot=(0,0,1;0rad)
  LinkedObject = -> Shape001
  Placement = pos=(106.045,-180.721,0) rot=(0,0,1;0rad)
FEATURE [App::Link] __REFERENCE__LED_D5_0mm_null_ln_052  label="${REFERENCE}_LED_D5.0mm_null053"
  LinkPlacement = pos=(89.281,-107.061,-3) rot=(0,0,1;0rad)
  LinkedObject = -> Shape002
  Placement = pos=(89.281,-107.061,-3) rot=(0,0,1;0rad)
FEATURE [App::Link] __REFERENCE__LED_D3_0mm_null_ln_030  label="${REFERENCE}_LED_D3.0mm_null031"
  LinkPlacement = pos=(132.207,-190.881,0) rot=(0,0,1;0rad)
  LinkedObject = -> Shape
  Placement = pos=(132.207,-190.881,0) rot=(0,0,1;0rad)
FEATURE [App::Link] __REFERENCE__Body_null_2__ln_030  label="${REFERENCE}_Body_null[2]031"
  LinkPlacement = pos=(133.477,-190.881,0) rot=(0,0,1;0rad)
  LinkedObject = -> Shape001
  Placement = pos=(133.477,-190.881,0) rot=(0,0,1;0rad)
FEATURE [App::Link] __REFERENCE__LED_D3_0mm_null_ln_031  label="${REFERENCE}_LED_D3.0mm_null032"
  LinkPlacement = pos=(127.127,-160.401,0) rot=(0,0,1;0rad)
  LinkedObject = -> Shape
  Placement = pos=(127.127,-160.401,0) rot=(0,0,1;0rad)
FEATURE [App::Link] __REFERENCE__Body_null_2__ln_031  label="${REFERENCE}_Body_null[2]032"
  LinkPlacement = pos=(128.397,-160.401,0) rot=(0,0,1;0rad)
  LinkedObject = -> Shape001
  Placement = pos=(128.397,-160.401,0) rot=(0,0,1;0rad)
FEATURE [App::Link] __REFERENCE__LED_D3_0mm_null_ln_032  label="${REFERENCE}_LED_D3.0mm_null033"
  LinkPlacement = pos=(127.127,-165.481,0) rot=(0,0,1;0rad)
  LinkedObject = -> Shape
  Placement = pos=(127.127,-165.481,0) rot=(0,0,1;0rad)
FEATURE [App::Link] __REFERENCE__Body_null_2__ln_032  label="${REFERENCE}_Body_null[2]033"
  LinkPlacement = pos=(128.397,-165.481,0) rot=(0,0,1;0rad)
  LinkedObject = -> Shape001
  Placement = pos=(128.397,-165.481,0) rot=(0,0,1;0rad)
FEATURE [App::Link] __REFERENCE__LED_D5_0mm_null_ln_053  label="${REFERENCE}_LED_D5.0mm_null054"
  LinkPlacement = pos=(151.457,-221.22,-3) rot=(0,0,1;0rad)
  LinkedObject = -> Shape002
  Placement = pos=(151.457,-221.22,-3) rot=(0,0,1;0rad)
FEATURE [App::Link] __REFERENCE__LED_D5_0mm_null_ln_054  label="${REFERENCE}_LED_D5.0mm_null055"
  LinkPlacement = pos=(162.941,-126.111,-3) rot=(0,0,1;0rad)
  LinkedObject = -> Shape002
  Placement = pos=(162.941,-126.111,-3) rot=(0,0,1;0rad)
FEATURE [App::Link] __REFERENCE__R_0805_2012Metric_null_ln_003  label="${REFERENCE}_R_0805_2012Metric_null004"
  LinkPlacement = pos=(214.757,-12.065,0) rot=(0,0,-1;1.5708rad)
  LinkedObject = -> Shape003
  Placement = pos=(214.757,-12.065,0) rot=(0,0,-1;1.5708rad)
FEATURE [App::Link] __REFERENCE__LED_D5_0mm_null_ln_055  label="${REFERENCE}_LED_D5.0mm_null056"
  LinkPlacement = pos=(39.2123,-191.144,-3) rot=(0,0,1;0rad)
  LinkedObject = -> Shape002
  Placement = pos=(39.2123,-191.144,-3) rot=(0,0,1;0rad)
FEATURE [App::Link] __REFERENCE__LED_D5_0mm_null_ln_056  label="${REFERENCE}_LED_D5.0mm_null057"
  LinkPlacement = pos=(154.051,-100.711,-3) rot=(0,0,1;0rad)
  LinkedObject = -> Shape002
  Placement = pos=(154.051,-100.711,-3) rot=(0,0,1;0rad)
FEATURE [App::Link] __REFERENCE__LED_D5_0mm_null_ln_057  label="${REFERENCE}_LED_D5.0mm_null058"
  LinkPlacement = pos=(135.001,-107.061,-3) rot=(0,0,1;0rad)
  LinkedObject = -> Shape002
  Placement = pos=(135.001,-107.061,-3) rot=(0,0,1;0rad)
FEATURE [App::Link] __REFERENCE__LED_D5_0mm_null_ln_058  label="${REFERENCE}_LED_D5.0mm_null059"
  LinkPlacement = pos=(39.2123,-48.3781,-3) rot=(0,0,1;0rad)
  LinkedObject = -> Shape002
  Placement = pos=(39.2123,-48.3781,-3) rot=(0,0,1;0rad)
FEATURE [App::Link] __REFERENCE__LED_D5_0mm_null_ln_059  label="${REFERENCE}_LED_D5.0mm_null060"
  LinkPlacement = pos=(128.651,-113.411,-3) rot=(0,0,1;0rad)
  LinkedObject = -> Shape002
  Placement = pos=(128.651,-113.411,-3) rot=(0,0,1;0rad)
FEATURE [App::Link] __REFERENCE__LED_D5_0mm_null_ln_060  label="${REFERENCE}_LED_D5.0mm_null061"
  LinkPlacement = pos=(14.1422,-97.581,-3) rot=(0,0,1;0rad)
  LinkedObject = -> Shape002
  Placement = pos=(14.1422,-97.581,-3) rot=(0,0,1;0rad)
FEATURE [App::Link] __REFERENCE__C_0805_2012Metric_null_ln_  label="${REFERENCE}_C_0805_2012Metric_null001"
  LinkPlacement = pos=(158.191,-174.752,0) rot=(0,0,-1;1.5708rad)
  LinkedObject = -> Shape004
  Placement = pos=(158.191,-174.752,0) rot=(0,0,-1;1.5708rad)
FEATURE [App::Link] __REFERENCE__LED_D3_0mm_null_ln_033  label="${REFERENCE}_LED_D3.0mm_null034"
  LinkPlacement = pos=(142.367,-185.801,0) rot=(0,0,1;0rad)
  LinkedObject = -> Shape
  Placement = pos=(142.367,-185.801,0) rot=(0,0,1;0rad)
FEATURE [App::Link] __REFERENCE__Body_null_2__ln_033  label="${REFERENCE}_Body_null[2]034"
  LinkPlacement = pos=(143.637,-185.801,0) rot=(0,0,1;0rad)
  LinkedObject = -> Shape001
  Placement = pos=(143.637,-185.801,0) rot=(0,0,1;0rad)
FEATURE [App::Link] __REFERENCE__LED_D5_0mm_null_ln_061  label="${REFERENCE}_LED_D5.0mm_null062"
  LinkPlacement = pos=(188.341,-113.411,-3) rot=(0,0,1;0rad)
  LinkedObject = -> Shape002
  Placement = pos=(188.341,-113.411,-3) rot=(0,0,1;0rad)
FEATURE [App::Link] __REFERENCE__LED_D3_0mm_null_ln_034  label="${REFERENCE}_LED_D3.0mm_null035"
  LinkPlacement = pos=(137.287,-185.801,0) rot=(0,0,1;0rad)
  LinkedObject = -> Shape
  Placement = pos=(137.287,-185.801,0) rot=(0,0,1;0rad)
FEATURE [App::Link] __REFERENCE__Body_null_2__ln_034  label="${REFERENCE}_Body_null[2]035"
  LinkPlacement = pos=(138.557,-185.801,0) rot=(0,0,1;0rad)
  LinkedObject = -> Shape001
  Placement = pos=(138.557,-185.801,0) rot=(0,0,1;0rad)
FEATURE [App::Link] __REFERENCE__LED_D3_0mm_null_ln_035  label="${REFERENCE}_LED_D3.0mm_null036"
  LinkPlacement = pos=(127.127,-53.721,0) rot=(0,0,1;0rad)
  LinkedObject = -> Shape
  Placement = pos=(127.127,-53.721,0) rot=(0,0,1;0rad)
FEATURE [App::Link] __REFERENCE__Body_null_2__ln_035  label="${REFERENCE}_Body_null[2]036"
  LinkPlacement = pos=(128.397,-53.721,0) rot=(0,0,1;0rad)
  LinkedObject = -> Shape001
  Placement = pos=(128.397,-53.721,0) rot=(0,0,1;0rad)
FEATURE [App::Link] __REFERENCE__LED_D3_0mm_null_ln_036  label="${REFERENCE}_LED_D3.0mm_null037"
  LinkPlacement = pos=(94.615,-160.401,0) rot=(0,0,1;0rad)
  LinkedObject = -> Shape
  Placement = pos=(94.615,-160.401,0) rot=(0,0,1;0rad)
FEATURE [App::Link] __REFERENCE__Body_null_2__ln_036  label="${REFERENCE}_Body_null[2]037"
  LinkPlacement = pos=(95.885,-160.401,0) rot=(0,0,1;0rad)
  LinkedObject = -> Shape001
  Placement = pos=(95.885,-160.401,0) rot=(0,0,1;0rad)
FEATURE [App::Link] __REFERENCE__LED_D3_0mm_null_ln_037  label="${REFERENCE}_LED_D3.0mm_null038"
  LinkPlacement = pos=(142.367,-74.041,0) rot=(0,0,1;0rad)
  LinkedObject = -> Shape
  Placement = pos=(142.367,-74.041,0) rot=(0,0,1;0rad)
FEATURE [App::Link] __REFERENCE__Body_null_2__ln_037  label="${REFERENCE}_Body_null[2]038"
  LinkPlacement = pos=(143.637,-74.041,0) rot=(0,0,1;0rad)
  LinkedObject = -> Shape001
  Placement = pos=(143.637,-74.041,0) rot=(0,0,1;0rad)
FEATURE [App::Link] __REFERENCE__LED_D3_0mm_null_ln_038  label="${REFERENCE}_LED_D3.0mm_null039"
  LinkPlacement = pos=(109.855,-68.961,0) rot=(0,0,1;0rad)
  LinkedObject = -> Shape
  Placement = pos=(109.855,-68.961,0) rot=(0,0,1;0rad)
FEATURE [App::Link] __REFERENCE__Body_null_2__ln_038  label="${REFERENCE}_Body_null[2]039"
  LinkPlacement = pos=(111.125,-68.961,0) rot=(0,0,1;0rad)
  LinkedObject = -> Shape001
  Placement = pos=(111.125,-68.961,0) rot=(0,0,1;0rad)
FEATURE [App::Link] __REFERENCE__LED_D5_0mm_null_ln_062  label="${REFERENCE}_LED_D5.0mm_null063"
  LinkPlacement = pos=(175.641,-138.811,-3) rot=(0,0,1;0rad)
  LinkedObject = -> Shape002
  Placement = pos=(175.641,-138.811,-3) rot=(0,0,1;0rad)
FEATURE [App::Link] __REFERENCE__LED_D3_0mm_null_ln_039  label="${REFERENCE}_LED_D3.0mm_null040"
  LinkPlacement = pos=(127.127,-175.641,0) rot=(0,0,1;0rad)
  LinkedObject = -> Shape
  Placement = pos=(127.127,-175.641,0) rot=(0,0,1;0rad)
FEATURE [App::Link] __REFERENCE__Body_null_2__ln_039  label="${REFERENCE}_Body_null[2]040"
  LinkPlacement = pos=(128.397,-175.641,0) rot=(0,0,1;0rad)
  LinkedObject = -> Shape001
  Placement = pos=(128.397,-175.641,0) rot=(0,0,1;0rad)
FEATURE [App::Link] __REFERENCE__LED_D5_0mm_null_ln_063  label="${REFERENCE}_LED_D5.0mm_null064"
  LinkPlacement = pos=(154.051,-119.761,-3) rot=(0,0,1;0rad)
  LinkedObject = -> Shape002
  Placement = pos=(154.051,-119.761,-3) rot=(0,0,1;0rad)
FEATURE [App::Link] __REFERENCE__R_0805_2012Metric_null_ln_004  label="${REFERENCE}_R_0805_2012Metric_null005"
  LinkPlacement = pos=(115.214,-199.695,0) rot=(0,0,1;3.14159rad)
  LinkedObject = -> Shape003
  Placement = pos=(115.214,-199.695,0) rot=(0,0,1;3.14159rad)
FEATURE [App::Link] __REFERENCE__LED_D5_0mm_null_ln_064  label="${REFERENCE}_LED_D5.0mm_null065"
  LinkPlacement = pos=(108.331,-107.061,-3) rot=(0,0,1;0rad)
  LinkedObject = -> Shape002
  Placement = pos=(108.331,-107.061,-3) rot=(0,0,1;0rad)
FEATURE [App::Link] __REFERENCE__LED_D3_0mm_null_ln_040  label="${REFERENCE}_LED_D3.0mm_null041"
  LinkPlacement = pos=(114.935,-48.641,0) rot=(0,0,1;0rad)
  LinkedObject = -> Shape
  Placement = pos=(114.935,-48.641,0) rot=(0,0,1;0rad)
FEATURE [App::Link] __REFERENCE__Body_null_2__ln_040  label="${REFERENCE}_Body_null[2]041"
  LinkPlacement = pos=(116.205,-48.641,0) rot=(0,0,1;0rad)
  LinkedObject = -> Shape001
  Placement = pos=(116.205,-48.641,0) rot=(0,0,1;0rad)
FEATURE [App::Link] __REFERENCE__LED_D5_0mm_null_ln_065  label="${REFERENCE}_LED_D5.0mm_null066"
  LinkPlacement = pos=(101.981,-107.061,-3) rot=(0,0,1;0rad)
  LinkedObject = -> Shape002
  Placement = pos=(101.981,-107.061,-3) rot=(0,0,1;0rad)
FEATURE [App::Link] __REFERENCE__LED_D3_0mm_null_ln_041  label="${REFERENCE}_LED_D3.0mm_null042"
  LinkPlacement = pos=(104.775,-48.641,0) rot=(0,0,1;0rad)
  LinkedObject = -> Shape
  Placement = pos=(104.775,-48.641,0) rot=(0,0,1;0rad)
FEATURE [App::Link] __REFERENCE__Body_null_2__ln_041  label="${REFERENCE}_Body_null[2]042"
  LinkPlacement = pos=(106.045,-48.641,0) rot=(0,0,1;0rad)
  LinkedObject = -> Shape001
  Placement = pos=(106.045,-48.641,0) rot=(0,0,1;0rad)
FEATURE [App::Link] __REFERENCE__LED_D5_0mm_null_ln_066  label="${REFERENCE}_LED_D5.0mm_null067"
  LinkPlacement = pos=(154.051,-132.461,-3) rot=(0,0,1;0rad)
  LinkedObject = -> Shape002
  Placement = pos=(154.051,-132.461,-3) rot=(0,0,1;0rad)
FEATURE [App::Link] __REFERENCE__LED_D5_0mm_null_ln_067  label="${REFERENCE}_LED_D5.0mm_null068"
  LinkPlacement = pos=(61.341,-132.461,-3) rot=(0,0,1;0rad)
  LinkedObject = -> Shape002
  Placement = pos=(61.341,-132.461,-3) rot=(0,0,1;0rad)
FEATURE [App::Link] __REFERENCE__LED_D5_0mm_null_ln_068  label="${REFERENCE}_LED_D5.0mm_null069"
  LinkPlacement = pos=(48.641,-113.411,-3) rot=(0,0,1;0rad)
  LinkedObject = -> Shape002
  Placement = pos=(48.641,-113.411,-3) rot=(0,0,1;0rad)
FEATURE [Part::Feature] Shape005  label="${REFERENCE}_LED_0805_2012Metric_null"
  Placement = pos=(109.727,-3.75988,0) rot=(0,0,1;1.5708rad)
  shape: bbox 1.25 x 2 x 1.1 mm, 50 faces (baked)
FEATURE [App::Link] __REFERENCE__LED_D3_0mm_null_ln_042  label="${REFERENCE}_LED_D3.0mm_null043"
  LinkPlacement = pos=(114.935,-79.121,0) rot=(0,0,1;0rad)
  LinkedObject = -> Shape
  Placement = pos=(114.935,-79.121,0) rot=(0,0,1;0rad)
FEATURE [App::Link] __REFERENCE__Body_null_2__ln_042  label="${REFERENCE}_Body_null[2]043"
  LinkPlacement = pos=(116.205,-79.121,0) rot=(0,0,1;0rad)
  LinkedObject = -> Shape001
  Placement = pos=(116.205,-79.121,0) rot=(0,0,1;0rad)
FEATURE [App::Link] __REFERENCE__C_0805_2012Metric_null_ln_001  label="${REFERENCE}_C_0805_2012Metric_null002"
  LinkPlacement = pos=(159.639,-69.469,0) rot=(0,0,1;3.14159rad)
  LinkedObject = -> Shape004
  Placement = pos=(159.639,-69.469,0) rot=(0,0,1;3.14159rad)
FEATURE [App::Link] __REFERENCE__LED_D5_0mm_null_ln_069  label="${REFERENCE}_LED_D5.0mm_null070"
  LinkPlacement = pos=(108.331,-126.111,-3) rot=(0,0,1;0rad)
  LinkedObject = -> Shape002
  Placement = pos=(108.331,-126.111,-3) rot=(0,0,1;0rad)
FEATURE [App::Link] __REFERENCE__LED_D5_0mm_null_ln_070  label="${REFERENCE}_LED_D5.0mm_null071"
  LinkPlacement = pos=(204.797,-182.466,-3) rot=(0,0,1;0rad)
  LinkedObject = -> Shape002
  Placement = pos=(204.797,-182.466,-3) rot=(0,0,1;0rad)
FEATURE [App::Link] __REFERENCE__LED_D5_0mm_null_ln_071  label="${REFERENCE}_LED_D5.0mm_null072"
  LinkPlacement = pos=(89.281,-119.761,-3) rot=(0,0,1;0rad)
  LinkedObject = -> Shape002
  Placement = pos=(89.281,-119.761,-3) rot=(0,0,1;0rad)
FEATURE [App::Link] __REFERENCE__LED_D5_0mm_null_ln_072  label="${REFERENCE}_LED_D5.0mm_null073"
  LinkPlacement = pos=(95.631,-132.461,-3) rot=(0,0,1;0rad)
  LinkedObject = -> Shape002
  Placement = pos=(95.631,-132.461,-3) rot=(0,0,1;0rad)
FEATURE [App::Link] __REFERENCE__LED_D3_0mm_null_ln_043  label="${REFERENCE}_LED_D3.0mm_null044"
  LinkPlacement = pos=(94.615,-79.121,0) rot=(0,0,1;0rad)
  LinkedObject = -> Shape
  Placement = pos=(94.615,-79.121,0) rot=(0,0,1;0rad)
FEATURE [App::Link] __REFERENCE__Body_null_2__ln_043  label="${REFERENCE}_Body_null[2]044"
  LinkPlacement = pos=(95.885,-79.121,0) rot=(0,0,1;0rad)
  LinkedObject = -> Shape001
  Placement = pos=(95.885,-79.121,0) rot=(0,0,1;0rad)
FEATURE [App::Link] __REFERENCE__LED_D5_0mm_null_ln_073  label="${REFERENCE}_LED_D5.0mm_null074"
  LinkPlacement = pos=(135.001,-132.461,-3) rot=(0,0,1;0rad)
  LinkedObject = -> Shape002
  Placement = pos=(135.001,-132.461,-3) rot=(0,0,1;0rad)
FEATURE [App::Link] __REFERENCE__LED_D3_0mm_null_ln_044  label="${REFERENCE}_LED_D3.0mm_null045"
  LinkPlacement = pos=(104.775,-53.721,0) rot=(0,0,1;0rad)
  LinkedObject = -> Shape
  Placement = pos=(104.775,-53.721,0) rot=(0,0,1;0rad)
FEATURE [App::Link] __REFERENCE__Body_null_2__ln_044  label="${REFERENCE}_Body_null[2]045"
  LinkPlacement = pos=(106.045,-53.721,0) rot=(0,0,1;0rad)
  LinkedObject = -> Shape001
  Placement = pos=(106.045,-53.721,0) rot=(0,0,1;0rad)
FEATURE [App::Link] __REFERENCE__LED_D3_0mm_null_ln_045  label="${REFERENCE}_LED_D3.0mm_null046"
  LinkPlacement = pos=(104.775,-170.561,0) rot=(0,0,1;0rad)
  LinkedObject = -> Shape
  Placement = pos=(104.775,-170.561,0) rot=(0,0,1;0rad)
FEATURE [App::Link] __REFERENCE__Body_null_2__ln_045  label="${REFERENCE}_Body_null[2]046"
  LinkPlacement = pos=(106.045,-170.561,0) rot=(0,0,1;0rad)
  LinkedObject = -> Shape001
  Placement = pos=(106.045,-170.561,0) rot=(0,0,1;0rad)
FEATURE [App::Link] __REFERENCE__LED_D5_0mm_null_ln_074  label="${REFERENCE}_LED_D5.0mm_null075"
  LinkPlacement = pos=(175.641,-119.761,-3) rot=(0,0,1;0rad)
  LinkedObject = -> Shape002
  Placement = pos=(175.641,-119.761,-3) rot=(0,0,1;0rad)
FEATURE [App::Link] __REFERENCE__LED_D5_0mm_null_ln_075  label="${REFERENCE}_LED_D5.0mm_null076"
  LinkPlacement = pos=(135.001,-119.761,-3) rot=(0,0,1;0rad)
  LinkedObject = -> Shape002
  Placement = pos=(135.001,-119.761,-3) rot=(0,0,1;0rad)
FEATURE [App::Link] __REFERENCE__LED_D3_0mm_null_ln_046  label="${REFERENCE}_LED_D3.0mm_null047"
  LinkPlacement = pos=(94.615,-68.961,0) rot=(0,0,1;0rad)
  LinkedObject = -> Shape
  Placement = pos=(94.615,-68.961,0) rot=(0,0,1;0rad)
FEATURE [App::Link] __REFERENCE__Body_null_2__ln_046  label="${REFERENCE}_Body_null[2]047"
  LinkPlacement = pos=(95.885,-68.961,0) rot=(0,0,1;0rad)
  LinkedObject = -> Shape001
  Placement = pos=(95.885,-68.961,0) rot=(0,0,1;0rad)
FEATURE [App::Link] __REFERENCE__LED_D3_0mm_null_ln_047  label="${REFERENCE}_LED_D3.0mm_null048"
  LinkPlacement = pos=(94.615,-185.801,0) rot=(0,0,1;0rad)
  LinkedObject = -> Shape
  Placement = pos=(94.615,-185.801,0) rot=(0,0,1;0rad)
FEATURE [App::Link] __REFERENCE__Body_null_2__ln_047  label="${REFERENCE}_Body_null[2]048"
  LinkPlacement = pos=(95.885,-185.801,0) rot=(0,0,1;0rad)
  LinkedObject = -> Shape001
  Placement = pos=(95.885,-185.801,0) rot=(0,0,1;0rad)
FEATURE [App::Link] __REFERENCE__LED_D5_0mm_null_ln_076  label="${REFERENCE}_LED_D5.0mm_null077"
  LinkPlacement = pos=(65.151,-27.3734,-3) rot=(0,0,1;0rad)
  LinkedObject = -> Shape002
  Placement = pos=(65.151,-27.3734,-3) rot=(0,0,1;0rad)
FEATURE [App::Link] __REFERENCE__LED_D5_0mm_null_ln_077  label="${REFERENCE}_LED_D5.0mm_null078"
  LinkPlacement = pos=(96.311,-224.11,-3) rot=(0,0,1;0rad)
  LinkedObject = -> Shape002
  Placement = pos=(96.311,-224.11,-3) rot=(0,0,1;0rad)
FEATURE [App::Link] __REFERENCE__LED_D3_0mm_null_ln_048  label="${REFERENCE}_LED_D3.0mm_null049"
  LinkPlacement = pos=(142.367,-63.881,0) rot=(0,0,1;0rad)
  LinkedObject = -> Shape
  Placement = pos=(142.367,-63.881,0) rot=(0,0,1;0rad)
FEATURE [App::Link] __REFERENCE__Body_null_2__ln_048  label="${REFERENCE}_Body_null[2]049"
  LinkPlacement = pos=(143.637,-63.881,0) rot=(0,0,1;0rad)
  LinkedObject = -> Shape001
  Placement = pos=(143.637,-63.881,0) rot=(0,0,1;0rad)
FEATURE [App::Link] __REFERENCE__LED_D3_0mm_null_ln_049  label="${REFERENCE}_LED_D3.0mm_null050"
  LinkPlacement = pos=(94.615,-58.801,0) rot=(0,0,1;0rad)
  LinkedObject = -> Shape
  Placement = pos=(94.615,-58.801,0) rot=(0,0,1;0rad)
FEATURE [App::Link] __REFERENCE__Body_null_2__ln_049  label="${REFERENCE}_Body_null[2]050"
  LinkPlacement = pos=(95.885,-58.801,0) rot=(0,0,1;0rad)
  LinkedObject = -> Shape001
  Placement = pos=(95.885,-58.801,0) rot=(0,0,1;0rad)
FEATURE [App::Link] __REFERENCE__LED_D3_0mm_null_ln_050  label="${REFERENCE}_LED_D3.0mm_null051"
  LinkPlacement = pos=(114.935,-68.961,0) rot=(0,0,1;0rad)
  LinkedObject = -> Shape
  Placement = pos=(114.935,-68.961,0) rot=(0,0,1;0rad)
FEATURE [App::Link] __REFERENCE__Body_null_2__ln_050  label="${REFERENCE}_Body_null[2]051"
  LinkPlacement = pos=(116.205,-68.961,0) rot=(0,0,1;0rad)
  LinkedObject = -> Shape001
  Placement = pos=(116.205,-68.961,0) rot=(0,0,1;0rad)
FEATURE [App::Link] __REFERENCE__LED_D5_0mm_null_ln_078  label="${REFERENCE}_LED_D5.0mm_null079"
  LinkPlacement = pos=(74.041,-100.711,-3) rot=(0,0,1;0rad)
  LinkedObject = -> Shape002
  Placement = pos=(74.041,-100.711,-3) rot=(0,0,1;0rad)
FEATURE [App::Link] __REFERENCE__LED_D3_0mm_null_ln_051  label="${REFERENCE}_LED_D3.0mm_null052"
  LinkPlacement = pos=(104.775,-58.801,0) rot=(0,0,1;0rad)
  LinkedObject = -> Shape
  Placement = pos=(104.775,-58.801,0) rot=(0,0,1;0rad)
FEATURE [App::Link] __REFERENCE__Body_null_2__ln_051  label="${REFERENCE}_Body_null[2]052"
  LinkPlacement = pos=(106.045,-58.801,0) rot=(0,0,1;0rad)
  LinkedObject = -> Shape001
  Placement = pos=(106.045,-58.801,0) rot=(0,0,1;0rad)
FEATURE [App::Link] __REFERENCE__LED_D5_0mm_null_ln_079  label="${REFERENCE}_LED_D5.0mm_null080"
  LinkPlacement = pos=(118.491,-127.381,-3) rot=(0,0,1;0rad)
  LinkedObject = -> Shape002
  Placement = pos=(118.491,-127.381,-3) rot=(0,0,1;0rad)
FEATURE [App::Link] __REFERENCE__LED_D5_0mm_null_ln_080  label="${REFERENCE}_LED_D5.0mm_null081"
  LinkPlacement = pos=(32.1851,-57.0561,-3) rot=(0,0,1;0rad)
  LinkedObject = -> Shape002
  Placement = pos=(32.1851,-57.0561,-3) rot=(0,0,1;0rad)
FEATURE [App::Link] __REFERENCE__LED_D5_0mm_null_ln_081  label="${REFERENCE}_LED_D5.0mm_null082"
  LinkPlacement = pos=(175.641,-107.061,-3) rot=(0,0,1;0rad)
  LinkedObject = -> Shape002
  Placement = pos=(175.641,-107.061,-3) rot=(0,0,1;0rad)
FEATURE [App::Link] __REFERENCE__LED_D3_0mm_null_ln_052  label="${REFERENCE}_LED_D3.0mm_null053"
  LinkPlacement = pos=(122.047,-170.561,0) rot=(0,0,1;0rad)
  LinkedObject = -> Shape
  Placement = pos=(122.047,-170.561,0) rot=(0,0,1;0rad)
FEATURE [App::Link] __REFERENCE__Body_null_2__ln_052  label="${REFERENCE}_Body_null[2]053"
  LinkPlacement = pos=(123.317,-170.561,0) rot=(0,0,1;0rad)
  LinkedObject = -> Shape001
  Placement = pos=(123.317,-170.561,0) rot=(0,0,1;0rad)
FEATURE [App::Link] __REFERENCE__LED_D5_0mm_null_ln_082  label="${REFERENCE}_LED_D5.0mm_null083"
  LinkPlacement = pos=(67.691,-107.061,-3) rot=(0,0,1;0rad)
  LinkedObject = -> Shape002
  Placement = pos=(67.691,-107.061,-3) rot=(0,0,1;0rad)
FEATURE [App::Link] __REFERENCE__LED_D5_0mm_null_ln_083  label="${REFERENCE}_LED_D5.0mm_null084"
  LinkPlacement = pos=(17.0323,-86.7951,-3) rot=(0,0,1;0rad)
  LinkedObject = -> Shape002
  Placement = pos=(17.0323,-86.7951,-3) rot=(0,0,1;0rad)
FEATURE [App::Link] __REFERENCE__LED_D5_0mm_null_ln_084  label="${REFERENCE}_LED_D5.0mm_null085"
  LinkPlacement = pos=(48.641,-119.761,-3) rot=(0,0,1;0rad)
  LinkedObject = -> Shape002
  Placement = pos=(48.641,-119.761,-3) rot=(0,0,1;0rad)
FEATURE [App::Link] __REFERENCE__LED_D3_0mm_null_ln_053  label="${REFERENCE}_LED_D3.0mm_null054"
  LinkPlacement = pos=(137.287,-48.641,0) rot=(0,0,1;0rad)
  LinkedObject = -> Shape
  Placement = pos=(137.287,-48.641,0) rot=(0,0,1;0rad)
FEATURE [App::Link] __REFERENCE__Body_null_2__ln_053  label="${REFERENCE}_Body_null[2]054"
  LinkPlacement = pos=(138.557,-48.641,0) rot=(0,0,1;0rad)
  LinkedObject = -> Shape001
  Placement = pos=(138.557,-48.641,0) rot=(0,0,1;0rad)
FEATURE [App::Link] __REFERENCE__LED_D5_0mm_null_ln_085  label="${REFERENCE}_LED_D5.0mm_null086"
  LinkPlacement = pos=(147.701,-107.061,-3) rot=(0,0,1;0rad)
  LinkedObject = -> Shape002
  Placement = pos=(147.701,-107.061,-3) rot=(0,0,1;0rad)
FEATURE [App::Link] __REFERENCE__LED_D3_0mm_null_ln_054  label="${REFERENCE}_LED_D3.0mm_null055"
  LinkPlacement = pos=(127.127,-79.121,0) rot=(0,0,1;0rad)
  LinkedObject = -> Shape
  Placement = pos=(127.127,-79.121,0) rot=(0,0,1;0rad)
FEATURE [App::Link] __REFERENCE__Body_null_2__ln_054  label="${REFERENCE}_Body_null[2]055"
  LinkPlacement = pos=(128.397,-79.121,0) rot=(0,0,1;0rad)
  LinkedObject = -> Shape001
  Placement = pos=(128.397,-79.121,0) rot=(0,0,1;0rad)
FEATURE [App::Link] __REFERENCE__LED_D5_0mm_null_ln_086  label="${REFERENCE}_LED_D5.0mm_null087"
  LinkPlacement = pos=(189.874,-199.04,-3) rot=(0,0,1;0rad)
  LinkedObject = -> Shape002
  Placement = pos=(189.874,-199.04,-3) rot=(0,0,1;0rad)
FEATURE [App::Link] __REFERENCE__LED_D3_0mm_null_ln_055  label="${REFERENCE}_LED_D3.0mm_null056"
  LinkPlacement = pos=(109.855,-170.561,0) rot=(0,0,1;0rad)
  LinkedObject = -> Shape
  Placement = pos=(109.855,-170.561,0) rot=(0,0,1;0rad)
FEATURE [App::Link] __REFERENCE__Body_null_2__ln_055  label="${REFERENCE}_Body_null[2]056"
  LinkPlacement = pos=(111.125,-170.561,0) rot=(0,0,1;0rad)
  LinkedObject = -> Shape001
  Placement = pos=(111.125,-170.561,0) rot=(0,0,1;0rad)
FEATURE [App::Link] __REFERENCE__LED_D5_0mm_null_ln_087  label="${REFERENCE}_LED_D5.0mm_null088"
  LinkPlacement = pos=(32.7025,-169.291,-3) rot=(0,0,1;0rad)
  LinkedObject = -> Shape002
  Placement = pos=(32.7025,-169.291,-3) rot=(0,0,1;0rad)
FEATURE [App::Link] __REFERENCE__LED_D3_0mm_null_ln_056  label="${REFERENCE}_LED_D3.0mm_null057"
  LinkPlacement = pos=(114.935,-180.721,0) rot=(0,0,1;0rad)
  LinkedObject = -> Shape
  Placement = pos=(114.935,-180.721,0) rot=(0,0,1;0rad)
FEATURE [App::Link] __REFERENCE__Body_null_2__ln_056  label="${REFERENCE}_Body_null[2]057"
  LinkPlacement = pos=(116.205,-180.721,0) rot=(0,0,1;0rad)
  LinkedObject = -> Shape001
  Placement = pos=(116.205,-180.721,0) rot=(0,0,1;0rad)
FEATURE [App::Link] __REFERENCE__LED_D5_0mm_null_ln_088  label="${REFERENCE}_LED_D5.0mm_null089"
  LinkPlacement = pos=(101.981,-100.711,-3) rot=(0,0,1;0rad)
  LinkedObject = -> Shape002
  Placement = pos=(101.981,-100.711,-3) rot=(0,0,1;0rad)
FEATURE [App::Link] __REFERENCE__LED_D3_0mm_null_ln_057  label="${REFERENCE}_LED_D3.0mm_null058"
  LinkPlacement = pos=(142.367,-190.881,0) rot=(0,0,1;0rad)
  LinkedObject = -> Shape
  Placement = pos=(142.367,-190.881,0) rot=(0,0,1;0rad)
FEATURE [App::Link] __REFERENCE__Body_null_2__ln_057  label="${REFERENCE}_Body_null[2]058"
  LinkPlacement = pos=(143.637,-190.881,0) rot=(0,0,1;0rad)
  LinkedObject = -> Shape001
  Placement = pos=(143.637,-190.881,0) rot=(0,0,1;0rad)
FEATURE [App::Link] __REFERENCE__LED_D5_0mm_null_ln_089  label="${REFERENCE}_LED_D5.0mm_null090"
  LinkPlacement = pos=(188.341,-138.811,-3) rot=(0,0,1;0rad)
  LinkedObject = -> Shape002
  Placement = pos=(188.341,-138.811,-3) rot=(0,0,1;0rad)
FEATURE [App::Link] __REFERENCE__LED_D5_0mm_null_ln_090  label="${REFERENCE}_LED_D5.0mm_null091"
  LinkPlacement = pos=(67.691,-126.111,-3) rot=(0,0,1;0rad)
  LinkedObject = -> Shape002
  Placement = pos=(67.691,-126.111,-3) rot=(0,0,1;0rad)
FEATURE [App::Link] __REFERENCE__LED_D5_0mm_null_ln_091  label="${REFERENCE}_LED_D5.0mm_null092"
  LinkPlacement = pos=(215.948,-76.3703,-3) rot=(0,0,1;0rad)
  LinkedObject = -> Shape002
  Placement = pos=(215.948,-76.3703,-3) rot=(0,0,1;0rad)
FEATURE [App::Link] __REFERENCE__LED_D5_0mm_null_ln_092  label="${REFERENCE}_LED_D5.0mm_null093"
  LinkPlacement = pos=(118.491,-20.701,-3) rot=(0,0,1;0rad)
  LinkedObject = -> Shape002
  Placement = pos=(118.491,-20.701,-3) rot=(0,0,1;0rad)
FEATURE [App::Link] __REFERENCE__LED_D5_0mm_null_ln_093  label="${REFERENCE}_LED_D5.0mm_null094"
  LinkPlacement = pos=(171.831,-27.3734,-3) rot=(0,0,1;0rad)
  LinkedObject = -> Shape002
  Placement = pos=(171.831,-27.3734,-3) rot=(0,0,1;0rad)
FEATURE [App::Link] __REFERENCE__LED_D5_0mm_null_ln_094  label="${REFERENCE}_LED_D5.0mm_null095"
  LinkPlacement = pos=(147.701,-100.711,-3) rot=(0,0,1;0rad)
  LinkedObject = -> Shape002
  Placement = pos=(147.701,-100.711,-3) rot=(0,0,1;0rad)
FEATURE [App::Link] __REFERENCE__LED_D5_0mm_null_ln_095  label="${REFERENCE}_LED_D5.0mm_null096"
  LinkPlacement = pos=(141.351,-126.111,-3) rot=(0,0,1;0rad)
  LinkedObject = -> Shape002
  Placement = pos=(141.351,-126.111,-3) rot=(0,0,1;0rad)
FEATURE [App::Link] __REFERENCE__LED_D5_0mm_null_ln_096  label="${REFERENCE}_LED_D5.0mm_null097"
  LinkPlacement = pos=(169.291,-132.461,-3) rot=(0,0,1;0rad)
  LinkedObject = -> Shape002
  Placement = pos=(169.291,-132.461,-3) rot=(0,0,1;0rad)
FEATURE [App::Link] __REFERENCE__LED_D3_0mm_null_ln_058  label="${REFERENCE}_LED_D3.0mm_null059"
  LinkPlacement = pos=(109.855,-190.881,0) rot=(0,0,1;0rad)
  LinkedObject = -> Shape
  Placement = pos=(109.855,-190.881,0) rot=(0,0,1;0rad)
FEATURE [App::Link] __REFERENCE__Body_null_2__ln_058  label="${REFERENCE}_Body_null[2]059"
  LinkPlacement = pos=(111.125,-190.881,0) rot=(0,0,1;0rad)
  LinkedObject = -> Shape001
  Placement = pos=(111.125,-190.881,0) rot=(0,0,1;0rad)
FEATURE [App::Link] __REFERENCE__LED_D3_0mm_null_ln_059  label="${REFERENCE}_LED_D3.0mm_null060"
  LinkPlacement = pos=(122.047,-160.401,0) rot=(0,0,1;0rad)
  LinkedObject = -> Shape
  Placement = pos=(122.047,-160.401,0) rot=(0,0,1;0rad)
FEATURE [App::Link] __REFERENCE__Body_null_2__ln_059  label="${REFERENCE}_Body_null[2]060"
  LinkPlacement = pos=(123.317,-160.401,0) rot=(0,0,1;0rad)
  LinkedObject = -> Shape001
  Placement = pos=(123.317,-160.401,0) rot=(0,0,1;0rad)
FEATURE [App::Link] __REFERENCE__LED_D5_0mm_null_ln_097  label="${REFERENCE}_LED_D5.0mm_null098"
  LinkPlacement = pos=(74.041,-107.061,-3) rot=(0,0,1;0rad)
  LinkedObject = -> Shape002
  Placement = pos=(74.041,-107.061,-3) rot=(0,0,1;0rad)
FEATURE [App::Link] __REFERENCE__LED_D5_0mm_null_ln_098  label="${REFERENCE}_LED_D5.0mm_null099"
  LinkPlacement = pos=(107.34,-225.857,-3) rot=(0,0,1;0rad)
  LinkedObject = -> Shape002
  Placement = pos=(107.34,-225.857,-3) rot=(0,0,1;0rad)
FEATURE [App::Link] __REFERENCE__LED_D3_0mm_null_ln_060  label="${REFERENCE}_LED_D3.0mm_null061"
  LinkPlacement = pos=(99.695,-190.881,0) rot=(0,0,1;0rad)
  LinkedObject = -> Shape
  Placement = pos=(99.695,-190.881,0) rot=(0,0,1;0rad)
FEATURE [App::Link] __REFERENCE__Body_null_2__ln_060  label="${REFERENCE}_Body_null[2]061"
  LinkPlacement = pos=(100.965,-190.881,0) rot=(0,0,1;0rad)
  LinkedObject = -> Shape001
  Placement = pos=(100.965,-190.881,0) rot=(0,0,1;0rad)
FEATURE [App::Link] __REFERENCE__R_0805_2012Metric_null_ln_005  label="${REFERENCE}_R_0805_2012Metric_null006"
  LinkPlacement = pos=(27.0764,-125.07,0) rot=(0,0,-1;1.5708rad)
  LinkedObject = -> Shape003
  Placement = pos=(27.0764,-125.07,0) rot=(0,0,-1;1.5708rad)
FEATURE [App::Link] __REFERENCE__LED_D5_0mm_null_ln_099  label="${REFERENCE}_LED_D5.0mm_null100"
  LinkPlacement = pos=(147.701,-126.111,-3) rot=(0,0,1;0rad)
  LinkedObject = -> Shape002
  Placement = pos=(147.701,-126.111,-3) rot=(0,0,1;0rad)
FEATURE [App::Link] __REFERENCE__LED_D3_0mm_null_ln_061  label="${REFERENCE}_LED_D3.0mm_null062"
  LinkPlacement = pos=(137.287,-170.561,0) rot=(0,0,1;0rad)
  LinkedObject = -> Shape
  Placement = pos=(137.287,-170.561,0) rot=(0,0,1;0rad)
FEATURE [App::Link] __REFERENCE__Body_null_2__ln_061  label="${REFERENCE}_Body_null[2]062"
  LinkPlacement = pos=(138.557,-170.561,0) rot=(0,0,1;0rad)
  LinkedObject = -> Shape001
  Placement = pos=(138.557,-170.561,0) rot=(0,0,1;0rad)
FEATURE [App::Link] __REFERENCE__LED_D5_0mm_null_ln_100  label="${REFERENCE}_LED_D5.0mm_null101"
  LinkPlacement = pos=(68.961,-205.549,-3) rot=(0,0,1;0rad)
  LinkedObject = -> Shape002
  Placement = pos=(68.961,-205.549,-3) rot=(0,0,1;0rad)
FEATURE [App::Link] __REFERENCE__C_0805_2012Metric_null_ln_002  label="${REFERENCE}_C_0805_2012Metric_null003"
  LinkPlacement = pos=(114.161,-91.761,0) rot=(0,0,-1;1.5708rad)
  LinkedObject = -> Shape004
  Placement = pos=(114.161,-91.761,0) rot=(0,0,-1;1.5708rad)
FEATURE [App::Link] __REFERENCE__LED_D5_0mm_null_ln_101  label="${REFERENCE}_LED_D5.0mm_null102"
  LinkPlacement = pos=(181.991,-119.761,-3) rot=(0,0,1;0rad)
  LinkedObject = -> Shape002
  Placement = pos=(181.991,-119.761,-3) rot=(0,0,1;0rad)
FEATURE [App::Link] __REFERENCE__LED_D5_0mm_null_ln_102  label="${REFERENCE}_LED_D5.0mm_null103"
  LinkPlacement = pos=(169.291,-126.111,-3) rot=(0,0,1;0rad)
  LinkedObject = -> Shape002
  Placement = pos=(169.291,-126.111,-3) rot=(0,0,1;0rad)
FEATURE [App::Link] __REFERENCE__LED_D5_0mm_null_ln_103  label="${REFERENCE}_LED_D5.0mm_null104"
  LinkPlacement = pos=(141.351,-119.761,-3) rot=(0,0,1;0rad)
  LinkedObject = -> Shape002
  Placement = pos=(141.351,-119.761,-3) rot=(0,0,1;0rad)
FEATURE [App::Link] __REFERENCE__LED_D3_0mm_null_ln_062  label="${REFERENCE}_LED_D3.0mm_null063"
  LinkPlacement = pos=(132.207,-74.041,0) rot=(0,0,1;0rad)
  LinkedObject = -> Shape
  Placement = pos=(132.207,-74.041,0) rot=(0,0,1;0rad)
FEATURE [App::Link] __REFERENCE__Body_null_2__ln_062  label="${REFERENCE}_Body_null[2]063"
  LinkPlacement = pos=(133.477,-74.041,0) rot=(0,0,1;0rad)
  LinkedObject = -> Shape001
  Placement = pos=(133.477,-74.041,0) rot=(0,0,1;0rad)
FEATURE [App::Link] __REFERENCE__LED_D5_0mm_null_ln_104  label="${REFERENCE}_LED_D5.0mm_null105"
  LinkPlacement = pos=(101.981,-126.111,-3) rot=(0,0,1;0rad)
  LinkedObject = -> Shape002
  Placement = pos=(101.981,-126.111,-3) rot=(0,0,1;0rad)
FEATURE [App::Link] __REFERENCE__C_0805_2012Metric_null_ln_003  label="${REFERENCE}_C_0805_2012Metric_null004"
  LinkPlacement = pos=(31.75,-125.07,0) rot=(0,0,1;1.5708rad)
  LinkedObject = -> Shape004
  Placement = pos=(31.75,-125.07,0) rot=(0,0,1;1.5708rad)
FEATURE [App::Link] __REFERENCE__LED_D3_0mm_null_ln_063  label="${REFERENCE}_LED_D3.0mm_null064"
  LinkPlacement = pos=(122.047,-68.961,0) rot=(0,0,1;0rad)
  LinkedObject = -> Shape
  Placement = pos=(122.047,-68.961,0) rot=(0,0,1;0rad)
FEATURE [App::Link] __REFERENCE__Body_null_2__ln_063  label="${REFERENCE}_Body_null[2]064"
  LinkPlacement = pos=(123.317,-68.961,0) rot=(0,0,1;0rad)
  LinkedObject = -> Shape001
  Placement = pos=(123.317,-68.961,0) rot=(0,0,1;0rad)
FEATURE [App::Link] __REFERENCE__LED_D5_0mm_null_ln_105  label="${REFERENCE}_LED_D5.0mm_null106"
  LinkPlacement = pos=(101.981,-113.411,-3) rot=(0,0,1;0rad)
  LinkedObject = -> Shape002
  Placement = pos=(101.981,-113.411,-3) rot=(0,0,1;0rad)
FEATURE [App::Link] __REFERENCE__LED_D5_0mm_null_ln_106  label="${REFERENCE}_LED_D5.0mm_null107"
  LinkPlacement = pos=(74.041,-119.761,-3) rot=(0,0,1;0rad)
  LinkedObject = -> Shape002
  Placement = pos=(74.041,-119.761,-3) rot=(0,0,1;0rad)
FEATURE [App::Link] __REFERENCE__LED_D3_0mm_null_ln_064  label="${REFERENCE}_LED_D3.0mm_null065"
  LinkPlacement = pos=(132.207,-63.881,0) rot=(0,0,1;0rad)
  LinkedObject = -> Shape
  Placement = pos=(132.207,-63.881,0) rot=(0,0,1;0rad)
FEATURE [App::Link] __REFERENCE__Body_null_2__ln_064  label="${REFERENCE}_Body_null[2]065"
  LinkPlacement = pos=(133.477,-63.881,0) rot=(0,0,1;0rad)
  LinkedObject = -> Shape001
  Placement = pos=(133.477,-63.881,0) rot=(0,0,1;0rad)
FEATURE [App::Link] __REFERENCE__LED_D5_0mm_null_ln_107  label="${REFERENCE}_LED_D5.0mm_null108"
  LinkPlacement = pos=(54.991,-138.811,-3) rot=(0,0,1;0rad)
  LinkedObject = -> Shape002
  Placement = pos=(54.991,-138.811,-3) rot=(0,0,1;0rad)
FEATURE [App::Link] __REFERENCE__LED_D3_0mm_null_ln_065  label="${REFERENCE}_LED_D3.0mm_null066"
  LinkPlacement = pos=(104.775,-175.641,0) rot=(0,0,1;0rad)
  LinkedObject = -> Shape
  Placement = pos=(104.775,-175.641,0) rot=(0,0,1;0rad)
FEATURE [App::Link] __REFERENCE__Body_null_2__ln_065  label="${REFERENCE}_Body_null[2]066"
  LinkPlacement = pos=(106.045,-175.641,0) rot=(0,0,1;0rad)
  LinkedObject = -> Shape001
  Placement = pos=(106.045,-175.641,0) rot=(0,0,1;0rad)
FEATURE [App::Link] __REFERENCE__LED_D5_0mm_null_ln_108  label="${REFERENCE}_LED_D5.0mm_null109"
  LinkPlacement = pos=(141.351,-113.411,-3) rot=(0,0,1;0rad)
  LinkedObject = -> Shape002
  Placement = pos=(141.351,-113.411,-3) rot=(0,0,1;0rad)
FEATURE [App::Link] __REFERENCE__LED_D3_0mm_null_ln_066  label="${REFERENCE}_LED_D3.0mm_null067"
  LinkPlacement = pos=(99.695,-48.641,0) rot=(0,0,1;0rad)
  LinkedObject = -> Shape
  Placement = pos=(99.695,-48.641,0) rot=(0,0,1;0rad)
FEATURE [App::Link] __REFERENCE__Body_null_2__ln_066  label="${REFERENCE}_Body_null[2]067"
  LinkPlacement = pos=(100.965,-48.641,0) rot=(0,0,1;0rad)
  LinkedObject = -> Shape001
  Placement = pos=(100.965,-48.641,0) rot=(0,0,1;0rad)
FEATURE [App::Link] __REFERENCE__R_0805_2012Metric_null_ln_006  label="${REFERENCE}_R_0805_2012Metric_null007"
  LinkPlacement = pos=(70.358,-169.672,0) rot=(0,0,1;3.14159rad)
  LinkedObject = -> Shape003
  Placement = pos=(70.358,-169.672,0) rot=(0,0,1;3.14159rad)
FEATURE [App::Link] __REFERENCE__LED_D5_0mm_null_ln_109  label="${REFERENCE}_LED_D5.0mm_null110"
  LinkPlacement = pos=(74.041,-132.461,-3) rot=(0,0,1;0rad)
  LinkedObject = -> Shape002
  Placement = pos=(74.041,-132.461,-3) rot=(0,0,1;0rad)
FEATURE [App::Link] __REFERENCE__LED_D5_0mm_null_ln_110  label="${REFERENCE}_LED_D5.0mm_null111"
  LinkPlacement = pos=(175.641,-126.111,-3) rot=(0,0,1;0rad)
  LinkedObject = -> Shape002
  Placement = pos=(175.641,-126.111,-3) rot=(0,0,1;0rad)
FEATURE [App::Link] __REFERENCE__LED_D5_0mm_null_ln_111  label="${REFERENCE}_LED_D5.0mm_null112"
  LinkPlacement = pos=(141.351,-100.711,-3) rot=(0,0,1;0rad)
  LinkedObject = -> Shape002
  Placement = pos=(141.351,-100.711,-3) rot=(0,0,1;0rad)
FEATURE [App::Link] __REFERENCE__C_0805_2012Metric_null_ln_004  label="${REFERENCE}_C_0805_2012Metric_null005"
  LinkPlacement = pos=(81.4324,-64.77,0) rot=(0,0,1;1.5708rad)
  LinkedObject = -> Shape004
  Placement = pos=(81.4324,-64.77,0) rot=(0,0,1;1.5708rad)
FEATURE [App::Link] __REFERENCE__LED_D5_0mm_null_ln_112  label="${REFERENCE}_LED_D5.0mm_null113"
  LinkPlacement = pos=(21.034,-76.3703,-3) rot=(0,0,1;0rad)
  LinkedObject = -> Shape002
  Placement = pos=(21.034,-76.3703,-3) rot=(0,0,1;0rad)
FEATURE [App::Link] __REFERENCE__R_0805_2012Metric_null_ln_007  label="${REFERENCE}_R_0805_2012Metric_null008"
  LinkPlacement = pos=(27.0764,-130.404,0) rot=(0,0,1;1.5708rad)
  LinkedObject = -> Shape003
  Placement = pos=(27.0764,-130.404,0) rot=(0,0,1;1.5708rad)
FEATURE [App::Link] __REFERENCE__LED_D5_0mm_null_ln_113  label="${REFERENCE}_LED_D5.0mm_null114"
  LinkPlacement = pos=(12.3954,-130.912,-3) rot=(0,0,1;0rad)
  LinkedObject = -> Shape002
  Placement = pos=(12.3954,-130.912,-3) rot=(0,0,1;0rad)
FEATURE [App::Link] __REFERENCE__LED_D5_0mm_null_ln_114  label="${REFERENCE}_LED_D5.0mm_null115"
  LinkPlacement = pos=(181.196,-33.4551,-3) rot=(0,0,1;0rad)
  LinkedObject = -> Shape002
  Placement = pos=(181.196,-33.4551,-3) rot=(0,0,1;0rad)
FEATURE [App::Link] __REFERENCE__C_0805_2012Metric_null_ln_005  label="${REFERENCE}_C_0805_2012Metric_null006"
  LinkPlacement = pos=(214.732,-115.214,0) rot=(0,0,1;1.5708rad)
  LinkedObject = -> Shape004
  Placement = pos=(214.732,-115.214,0) rot=(0,0,1;1.5708rad)
FEATURE [App::Link] __REFERENCE__LED_D5_0mm_null_ln_115  label="${REFERENCE}_LED_D5.0mm_null116"
  LinkPlacement = pos=(189.874,-40.4823,-3) rot=(0,0,1;0rad)
  LinkedObject = -> Shape002
  Placement = pos=(189.874,-40.4823,-3) rot=(0,0,1;0rad)
FEATURE [App::Link] __REFERENCE__LED_D5_0mm_null_ln_116  label="${REFERENCE}_LED_D5.0mm_null117"
  LinkPlacement = pos=(162.941,-119.761,-3) rot=(0,0,1;0rad)
  LinkedObject = -> Shape002
  Placement = pos=(162.941,-119.761,-3) rot=(0,0,1;0rad)
FEATURE [App::Link] __REFERENCE__LED_D3_0mm_null_ln_067  label="${REFERENCE}_LED_D3.0mm_null068"
  LinkPlacement = pos=(94.615,-180.721,0) rot=(0,0,1;0rad)
  LinkedObject = -> Shape
  Placement = pos=(94.615,-180.721,0) rot=(0,0,1;0rad)
FEATURE [App::Link] __REFERENCE__Body_null_2__ln_067  label="${REFERENCE}_Body_null[2]068"
  LinkPlacement = pos=(95.885,-180.721,0) rot=(0,0,1;0rad)
  LinkedObject = -> Shape001
  Placement = pos=(95.885,-180.721,0) rot=(0,0,1;0rad)
FEATURE [App::Link] __REFERENCE__LED_D3_0mm_null_ln_068  label="${REFERENCE}_LED_D3.0mm_null069"
  LinkPlacement = pos=(104.775,-185.801,0) rot=(0,0,1;0rad)
  LinkedObject = -> Shape
  Placement = pos=(104.775,-185.801,0) rot=(0,0,1;0rad)
FEATURE [App::Link] __REFERENCE__Body_null_2__ln_068  label="${REFERENCE}_Body_null[2]069"
  LinkPlacement = pos=(106.045,-185.801,0) rot=(0,0,1;0rad)
  LinkedObject = -> Shape001
  Placement = pos=(106.045,-185.801,0) rot=(0,0,1;0rad)
FEATURE [App::Link] __REFERENCE__LED_D5_0mm_null_ln_117  label="${REFERENCE}_LED_D5.0mm_null118"
  LinkPlacement = pos=(14.1422,-141.941,-3) rot=(0,0,1;0rad)
  LinkedObject = -> Shape002
  Placement = pos=(14.1422,-141.941,-3) rot=(0,0,1;0rad)
FEATURE [App::Link] __REFERENCE__LED_D5_0mm_null_ln_118  label="${REFERENCE}_LED_D5.0mm_null119"
  LinkPlacement = pos=(188.341,-100.711,-3) rot=(0,0,1;0rad)
  LinkedObject = -> Shape002
  Placement = pos=(188.341,-100.711,-3) rot=(0,0,1;0rad)
FEATURE [App::Link] __REFERENCE__LED_D3_0mm_null_ln_069  label="${REFERENCE}_LED_D3.0mm_null070"
  LinkPlacement = pos=(137.287,-190.881,0) rot=(0,0,1;0rad)
  LinkedObject = -> Shape
  Placement = pos=(137.287,-190.881,0) rot=(0,0,1;0rad)
FEATURE [App::Link] __REFERENCE__Body_null_2__ln_069  label="${REFERENCE}_Body_null[2]070"
  LinkPlacement = pos=(138.557,-190.881,0) rot=(0,0,1;0rad)
  LinkedObject = -> Shape001
  Placement = pos=(138.557,-190.881,0) rot=(0,0,1;0rad)
FEATURE [App::Link] __REFERENCE__C_0805_2012Metric_null_ln_006  label="${REFERENCE}_C_0805_2012Metric_null007"
  LinkPlacement = pos=(113.03,-204.775,0) rot=(0,0,-1;1.5708rad)
  LinkedObject = -> Shape004
  Placement = pos=(113.03,-204.775,0) rot=(0,0,-1;1.5708rad)
FEATURE [App::Link] __REFERENCE__LED_D5_0mm_null_ln_119  label="${REFERENCE}_LED_D5.0mm_null120"
  LinkPlacement = pos=(224.587,-108.61,-3) rot=(0,0,1;0rad)
  LinkedObject = -> Shape002
  Placement = pos=(224.587,-108.61,-3) rot=(0,0,1;0rad)
FEATURE [App::Link] __REFERENCE__LED_D3_0mm_null_ln_070  label="${REFERENCE}_LED_D3.0mm_null071"
  LinkPlacement = pos=(122.047,-165.481,0) rot=(0,0,1;0rad)
  LinkedObject = -> Shape
  Placement = pos=(122.047,-165.481,0) rot=(0,0,1;0rad)
FEATURE [App::Link] __REFERENCE__Body_null_2__ln_070  label="${REFERENCE}_Body_null[2]071"
  LinkPlacement = pos=(123.317,-165.481,0) rot=(0,0,1;0rad)
  LinkedObject = -> Shape001
  Placement = pos=(123.317,-165.481,0) rot=(0,0,1;0rad)
FEATURE [App::Link] __REFERENCE__LED_D5_0mm_null_ln_120  label="${REFERENCE}_LED_D5.0mm_null121"
  LinkPlacement = pos=(128.651,-132.461,-3) rot=(0,0,1;0rad)
  LinkedObject = -> Shape002
  Placement = pos=(128.651,-132.461,-3) rot=(0,0,1;0rad)
FEATURE [App::Link] __REFERENCE__LED_D5_0mm_null_ln_121  label="${REFERENCE}_LED_D5.0mm_null122"
  LinkPlacement = pos=(140.671,-15.4122,-3) rot=(0,0,1;0rad)
  LinkedObject = -> Shape002
  Placement = pos=(140.671,-15.4122,-3) rot=(0,0,1;0rad)
FEATURE [App::Link] __REFERENCE__LED_D5_0mm_null_ln_122  label="${REFERENCE}_LED_D5.0mm_null123"
  LinkPlacement = pos=(162.941,-113.411,-3) rot=(0,0,1;0rad)
  LinkedObject = -> Shape002
  Placement = pos=(162.941,-113.411,-3) rot=(0,0,1;0rad)
FEATURE [App::Link] __REFERENCE__LED_D5_0mm_null_ln_123  label="${REFERENCE}_LED_D5.0mm_null124"
  LinkPlacement = pos=(188.341,-126.111,-3) rot=(0,0,1;0rad)
  LinkedObject = -> Shape002
  Placement = pos=(188.341,-126.111,-3) rot=(0,0,1;0rad)
FEATURE [App::Link] __REFERENCE__LED_D3_0mm_null_ln_071  label="${REFERENCE}_LED_D3.0mm_null072"
  LinkPlacement = pos=(99.695,-170.561,0) rot=(0,0,1;0rad)
  LinkedObject = -> Shape
  Placement = pos=(99.695,-170.561,0) rot=(0,0,1;0rad)
FEATURE [App::Link] __REFERENCE__Body_null_2__ln_071  label="${REFERENCE}_Body_null[2]072"
  LinkPlacement = pos=(100.965,-170.561,0) rot=(0,0,1;0rad)
  LinkedObject = -> Shape001
  Placement = pos=(100.965,-170.561,0) rot=(0,0,1;0rad)
FEATURE [App::Link] __REFERENCE__LED_D5_0mm_null_ln_124  label="${REFERENCE}_LED_D5.0mm_null125"
  LinkPlacement = pos=(154.051,-126.111,-3) rot=(0,0,1;0rad)
  LinkedObject = -> Shape002
  Placement = pos=(154.051,-126.111,-3) rot=(0,0,1;0rad)
FEATURE [App::Link] __REFERENCE__LED_D5_0mm_null_ln_125  label="${REFERENCE}_LED_D5.0mm_null126"
  LinkPlacement = pos=(222.84,-141.941,-3) rot=(0,0,1;0rad)
  LinkedObject = -> Shape002
  Placement = pos=(222.84,-141.941,-3) rot=(0,0,1;0rad)
FEATURE [App::Link] __REFERENCE__LED_D3_0mm_null_ln_072  label="${REFERENCE}_LED_D3.0mm_null073"
  LinkPlacement = pos=(132.207,-170.561,0) rot=(0,0,1;0rad)
  LinkedObject = -> Shape
  Placement = pos=(132.207,-170.561,0) rot=(0,0,1;0rad)
FEATURE [App::Link] __REFERENCE__Body_null_2__ln_072  label="${REFERENCE}_Body_null[2]073"
  LinkPlacement = pos=(133.477,-170.561,0) rot=(0,0,1;0rad)
  LinkedObject = -> Shape001
  Placement = pos=(133.477,-170.561,0) rot=(0,0,1;0rad)
FEATURE [App::Link] __REFERENCE__LED_D3_0mm_null_ln_073  label="${REFERENCE}_LED_D3.0mm_null074"
  LinkPlacement = pos=(137.287,-160.401,0) rot=(0,0,1;0rad)
  LinkedObject = -> Shape
  Placement = pos=(137.287,-160.401,0) rot=(0,0,1;0rad)
FEATURE [App::Link] __REFERENCE__Body_null_2__ln_073  label="${REFERENCE}_Body_null[2]074"
  LinkPlacement = pos=(138.557,-160.401,0) rot=(0,0,1;0rad)
  LinkedObject = -> Shape001
  Placement = pos=(138.557,-160.401,0) rot=(0,0,1;0rad)
FEATURE [App::Link] __REFERENCE__LED_D5_0mm_null_ln_126  label="${REFERENCE}_LED_D5.0mm_null127"
  LinkPlacement = pos=(181.991,-113.411,-3) rot=(0,0,1;0rad)
  LinkedObject = -> Shape002
  Placement = pos=(181.991,-113.411,-3) rot=(0,0,1;0rad)
FEATURE [App::Link] __REFERENCE__LED_D3_0mm_null_ln_074  label="${REFERENCE}_LED_D3.0mm_null075"
  LinkPlacement = pos=(104.775,-63.881,0) rot=(0,0,1;0rad)
  LinkedObject = -> Shape
  Placement = pos=(104.775,-63.881,0) rot=(0,0,1;0rad)
FEATURE [App::Link] __REFERENCE__Body_null_2__ln_074  label="${REFERENCE}_Body_null[2]075"
  LinkPlacement = pos=(106.045,-63.881,0) rot=(0,0,1;0rad)
  LinkedObject = -> Shape001
  Placement = pos=(106.045,-63.881,0) rot=(0,0,1;0rad)
FEATURE [App::Link] __REFERENCE__LED_D3_0mm_null_ln_075  label="${REFERENCE}_LED_D3.0mm_null076"
  LinkPlacement = pos=(122.047,-180.721,0) rot=(0,0,1;0rad)
  LinkedObject = -> Shape
  Placement = pos=(122.047,-180.721,0) rot=(0,0,1;0rad)
FEATURE [App::Link] __REFERENCE__Body_null_2__ln_075  label="${REFERENCE}_Body_null[2]076"
  LinkPlacement = pos=(123.317,-180.721,0) rot=(0,0,1;0rad)
  LinkedObject = -> Shape001
  Placement = pos=(123.317,-180.721,0) rot=(0,0,1;0rad)
FEATURE [App::Link] __REFERENCE__LED_D5_0mm_null_ln_127  label="${REFERENCE}_LED_D5.0mm_null128"
  LinkPlacement = pos=(135.001,-126.111,-3) rot=(0,0,1;0rad)
  LinkedObject = -> Shape002
  Placement = pos=(135.001,-126.111,-3) rot=(0,0,1;0rad)
FEATURE [App::Link] __REFERENCE__LED_D5_0mm_null_ln_128  label="${REFERENCE}_LED_D5.0mm_null129"
  LinkPlacement = pos=(188.341,-107.061,-3) rot=(0,0,1;0rad)
  LinkedObject = -> Shape002
  Placement = pos=(188.341,-107.061,-3) rot=(0,0,1;0rad)
FEATURE [App::Link] __REFERENCE__LED_D3_0mm_null_ln_076  label="${REFERENCE}_LED_D3.0mm_null077"
  LinkPlacement = pos=(122.047,-185.801,0) rot=(0,0,1;0rad)
  LinkedObject = -> Shape
  Placement = pos=(122.047,-185.801,0) rot=(0,0,1;0rad)
FEATURE [App::Link] __REFERENCE__Body_null_2__ln_076  label="${REFERENCE}_Body_null[2]077"
  LinkPlacement = pos=(123.317,-185.801,0) rot=(0,0,1;0rad)
  LinkedObject = -> Shape001
  Placement = pos=(123.317,-185.801,0) rot=(0,0,1;0rad)
FEATURE [App::Link] __REFERENCE__LED_D5_0mm_null_ln_129  label="${REFERENCE}_LED_D5.0mm_null130"
  LinkPlacement = pos=(85.5251,-221.22,-3) rot=(0,0,1;0rad)
  LinkedObject = -> Shape002
  Placement = pos=(85.5251,-221.22,-3) rot=(0,0,1;0rad)
FEATURE [App::Link] __REFERENCE__LED_D3_0mm_null_ln_077  label="${REFERENCE}_LED_D3.0mm_null078"
  LinkPlacement = pos=(99.695,-180.721,0) rot=(0,0,1;0rad)
  LinkedObject = -> Shape
  Placement = pos=(99.695,-180.721,0) rot=(0,0,1;0rad)
FEATURE [App::Link] __REFERENCE__Body_null_2__ln_077  label="${REFERENCE}_Body_null[2]078"
  LinkPlacement = pos=(100.965,-180.721,0) rot=(0,0,1;0rad)
  LinkedObject = -> Shape001
  Placement = pos=(100.965,-180.721,0) rot=(0,0,1;0rad)
FEATURE [App::Link] __REFERENCE__LED_D5_0mm_null_ln_130  label="${REFERENCE}_LED_D5.0mm_null131"
  LinkPlacement = pos=(225.171,-119.761,-3) rot=(0,0,1;0rad)
  LinkedObject = -> Shape002
  Placement = pos=(225.171,-119.761,-3) rot=(0,0,1;0rad)
FEATURE [App::Link] __REFERENCE__LED_D5_0mm_null_ln_131  label="${REFERENCE}_LED_D5.0mm_null132"
  LinkPlacement = pos=(135.001,-100.711,-3) rot=(0,0,1;0rad)
  LinkedObject = -> Shape002
  Placement = pos=(135.001,-100.711,-3) rot=(0,0,1;0rad)
FEATURE [App::Link] __REFERENCE__LED_D5_0mm_null_ln_132  label="${REFERENCE}_LED_D5.0mm_null133"
  LinkPlacement = pos=(95.631,-107.061,-3) rot=(0,0,1;0rad)
  LinkedObject = -> Shape002
  Placement = pos=(95.631,-107.061,-3) rot=(0,0,1;0rad)
FEATURE [App::Link] __REFERENCE__LED_D5_0mm_null_ln_133  label="${REFERENCE}_LED_D5.0mm_null134"
  LinkPlacement = pos=(32.7025,-70.231,-3) rot=(0,0,1;0rad)
  LinkedObject = -> Shape002
  Placement = pos=(32.7025,-70.231,-3) rot=(0,0,1;0rad)
FEATURE [App::Link] __REFERENCE__LED_D5_0mm_null_ln_134  label="${REFERENCE}_LED_D5.0mm_null135"
  LinkPlacement = pos=(147.701,-138.811,-3) rot=(0,0,1;0rad)
  LinkedObject = -> Shape002
  Placement = pos=(147.701,-138.811,-3) rot=(0,0,1;0rad)
FEATURE [App::Link] __REFERENCE__LED_D5_0mm_null_ln_135  label="${REFERENCE}_LED_D5.0mm_null136"
  LinkPlacement = pos=(75.1003,-217.218,-3) rot=(0,0,1;0rad)
  LinkedObject = -> Shape002
  Placement = pos=(75.1003,-217.218,-3) rot=(0,0,1;0rad)
FEATURE [App::Link] __REFERENCE__LED_D3_0mm_null_ln_078  label="${REFERENCE}_LED_D3.0mm_null079"
  LinkPlacement = pos=(109.855,-160.401,0) rot=(0,0,1;0rad)
  LinkedObject = -> Shape
  Placement = pos=(109.855,-160.401,0) rot=(0,0,1;0rad)
FEATURE [App::Link] __REFERENCE__Body_null_2__ln_078  label="${REFERENCE}_Body_null[2]079"
  LinkPlacement = pos=(111.125,-160.401,0) rot=(0,0,1;0rad)
  LinkedObject = -> Shape001
  Placement = pos=(111.125,-160.401,0) rot=(0,0,1;0rad)
FEATURE [App::Link] __REFERENCE__LED_D3_0mm_null_ln_079  label="${REFERENCE}_LED_D3.0mm_null080"
  LinkPlacement = pos=(114.935,-190.881,0) rot=(0,0,1;0rad)
  LinkedObject = -> Shape
  Placement = pos=(114.935,-190.881,0) rot=(0,0,1;0rad)
FEATURE [App::Link] __REFERENCE__Body_null_2__ln_079  label="${REFERENCE}_Body_null[2]080"
  LinkPlacement = pos=(116.205,-190.881,0) rot=(0,0,1;0rad)
  LinkedObject = -> Shape001
  Placement = pos=(116.205,-190.881,0) rot=(0,0,1;0rad)
FEATURE [App::Link] __REFERENCE__LED_D3_0mm_null_ln_080  label="${REFERENCE}_LED_D3.0mm_null081"
  LinkPlacement = pos=(127.127,-48.641,0) rot=(0,0,1;0rad)
  LinkedObject = -> Shape
  Placement = pos=(127.127,-48.641,0) rot=(0,0,1;0rad)
FEATURE [App::Link] __REFERENCE__Body_null_2__ln_080  label="${REFERENCE}_Body_null[2]081"
  LinkPlacement = pos=(128.397,-48.641,0) rot=(0,0,1;0rad)
  LinkedObject = -> Shape001
  Placement = pos=(128.397,-48.641,0) rot=(0,0,1;0rad)
FEATURE [App::Link] __REFERENCE__LED_D3_0mm_null_ln_081  label="${REFERENCE}_LED_D3.0mm_null082"
  LinkPlacement = pos=(94.615,-74.041,0) rot=(0,0,1;0rad)
  LinkedObject = -> Shape
  Placement = pos=(94.615,-74.041,0) rot=(0,0,1;0rad)
FEATURE [App::Link] __REFERENCE__Body_null_2__ln_081  label="${REFERENCE}_Body_null[2]082"
  LinkPlacement = pos=(95.885,-74.041,0) rot=(0,0,1;0rad)
  LinkedObject = -> Shape001
  Placement = pos=(95.885,-74.041,0) rot=(0,0,1;0rad)
FEATURE [App::Link] __REFERENCE__LED_D5_0mm_null_ln_136  label="${REFERENCE}_LED_D5.0mm_null137"
  LinkPlacement = pos=(141.351,-132.461,-3) rot=(0,0,1;0rad)
  LinkedObject = -> Shape002
  Placement = pos=(141.351,-132.461,-3) rot=(0,0,1;0rad)
FEATURE [App::Link] __REFERENCE__LED_D5_0mm_null_ln_137  label="${REFERENCE}_LED_D5.0mm_null138"
  LinkPlacement = pos=(95.631,-113.411,-3) rot=(0,0,1;0rad)
  LinkedObject = -> Shape002
  Placement = pos=(95.631,-113.411,-3) rot=(0,0,1;0rad)
FEATURE [App::Link] __REFERENCE__LED_D5_0mm_null_ln_138  label="${REFERENCE}_LED_D5.0mm_null139"
  LinkPlacement = pos=(101.981,-138.811,-3) rot=(0,0,1;0rad)
  LinkedObject = -> Shape002
  Placement = pos=(101.981,-138.811,-3) rot=(0,0,1;0rad)
FEATURE [App::Link] __REFERENCE__LED_D3_0mm_null_ln_082  label="${REFERENCE}_LED_D3.0mm_null083"
  LinkPlacement = pos=(104.775,-165.481,0) rot=(0,0,1;0rad)
  LinkedObject = -> Shape
  Placement = pos=(104.775,-165.481,0) rot=(0,0,1;0rad)
FEATURE [App::Link] __REFERENCE__Body_null_2__ln_082  label="${REFERENCE}_Body_null[2]083"
  LinkPlacement = pos=(106.045,-165.481,0) rot=(0,0,1;0rad)
  LinkedObject = -> Shape001
  Placement = pos=(106.045,-165.481,0) rot=(0,0,1;0rad)
FEATURE [App::Link] __REFERENCE__LED_D5_0mm_null_ln_139  label="${REFERENCE}_LED_D5.0mm_null140"
  LinkPlacement = pos=(67.691,-113.411,-3) rot=(0,0,1;0rad)
  LinkedObject = -> Shape002
  Placement = pos=(67.691,-113.411,-3) rot=(0,0,1;0rad)
FEATURE [App::Link] __REFERENCE__LED_D5_0mm_null_ln_140  label="${REFERENCE}_LED_D5.0mm_null141"
  LinkPlacement = pos=(169.291,-113.411,-3) rot=(0,0,1;0rad)
  LinkedObject = -> Shape002
  Placement = pos=(169.291,-113.411,-3) rot=(0,0,1;0rad)
FEATURE [App::Link] __REFERENCE__LED_D3_0mm_null_ln_083  label="${REFERENCE}_LED_D3.0mm_null084"
  LinkPlacement = pos=(142.367,-68.961,0) rot=(0,0,1;0rad)
  LinkedObject = -> Shape
  Placement = pos=(142.367,-68.961,0) rot=(0,0,1;0rad)
FEATURE [App::Link] __REFERENCE__Body_null_2__ln_083  label="${REFERENCE}_Body_null[2]084"
  LinkPlacement = pos=(143.637,-68.961,0) rot=(0,0,1;0rad)
  LinkedObject = -> Shape001
  Placement = pos=(143.637,-68.961,0) rot=(0,0,1;0rad)
FEATURE [App::Link] __REFERENCE__LED_0805_2012Metric_null_ln_  label="${REFERENCE}_LED_0805_2012Metric_null001"
  LinkPlacement = pos=(89.6611,-3.75988,0) rot=(0,0,1;1.5708rad)
  LinkedObject = -> Shape005
  Placement = pos=(89.6611,-3.75988,0) rot=(0,0,1;1.5708rad)
FEATURE [App::Link] __REFERENCE__LED_D3_0mm_null_ln_084  label="${REFERENCE}_LED_D3.0mm_null085"
  LinkPlacement = pos=(132.207,-58.801,0) rot=(0,0,1;0rad)
  LinkedObject = -> Shape
  Placement = pos=(132.207,-58.801,0) rot=(0,0,1;0rad)
FEATURE [App::Link] __REFERENCE__Body_null_2__ln_084  label="${REFERENCE}_Body_null[2]085"
  LinkPlacement = pos=(133.477,-58.801,0) rot=(0,0,1;0rad)
  LinkedObject = -> Shape001
  Placement = pos=(133.477,-58.801,0) rot=(0,0,1;0rad)
FEATURE [App::Link] __REFERENCE__C_0805_2012Metric_null_ln_007  label="${REFERENCE}_C_0805_2012Metric_null008"
  LinkPlacement = pos=(201.879,-125.12,0) rot=(0,0,1;1.5708rad)
  LinkedObject = -> Shape004
  Placement = pos=(201.879,-125.12,0) rot=(0,0,1;1.5708rad)
FEATURE [App::Link] __REFERENCE__LED_D3_0mm_null_ln_085  label="${REFERENCE}_LED_D3.0mm_null086"
  LinkPlacement = pos=(122.047,-58.801,0) rot=(0,0,1;0rad)
  LinkedObject = -> Shape
  Placement = pos=(122.047,-58.801,0) rot=(0,0,1;0rad)
FEATURE [App::Link] __REFERENCE__Body_null_2__ln_085  label="${REFERENCE}_Body_null[2]086"
  LinkPlacement = pos=(123.317,-58.801,0) rot=(0,0,1;0rad)
  LinkedObject = -> Shape001
  Placement = pos=(123.317,-58.801,0) rot=(0,0,1;0rad)
FEATURE [App::Link] __REFERENCE__LED_D5_0mm_null_ln_141  label="${REFERENCE}_LED_D5.0mm_null142"
  LinkPlacement = pos=(204.279,-169.291,-3) rot=(0,0,1;0rad)
  LinkedObject = -> Shape002
  Placement = pos=(204.279,-169.291,-3) rot=(0,0,1;0rad)
FEATURE [App::Link] __REFERENCE__LED_D3_0mm_null_ln_086  label="${REFERENCE}_LED_D3.0mm_null087"
  LinkPlacement = pos=(127.127,-180.721,0) rot=(0,0,1;0rad)
  LinkedObject = -> Shape
  Placement = pos=(127.127,-180.721,0) rot=(0,0,1;0rad)
FEATURE [App::Link] __REFERENCE__Body_null_2__ln_086  label="${REFERENCE}_Body_null[2]087"
  LinkPlacement = pos=(128.397,-180.721,0) rot=(0,0,1;0rad)
  LinkedObject = -> Shape001
  Placement = pos=(128.397,-180.721,0) rot=(0,0,1;0rad)
FEATURE [App::Link] __REFERENCE__LED_D5_0mm_null_ln_142  label="${REFERENCE}_LED_D5.0mm_null143"
  LinkPlacement = pos=(47.1081,-199.04,-3) rot=(0,0,1;0rad)
  LinkedObject = -> Shape002
  Placement = pos=(47.1081,-199.04,-3) rot=(0,0,1;0rad)
FEATURE [App::Link] __REFERENCE__LED_D5_0mm_null_ln_143  label="${REFERENCE}_LED_D5.0mm_null144"
  LinkPlacement = pos=(61.341,-138.811,-3) rot=(0,0,1;0rad)
  LinkedObject = -> Shape002
  Placement = pos=(61.341,-138.811,-3) rot=(0,0,1;0rad)
FEATURE [App::Link] __REFERENCE__LED_D5_0mm_null_ln_144  label="${REFERENCE}_LED_D5.0mm_null145"
  LinkPlacement = pos=(219.95,-152.727,-3) rot=(0,0,1;0rad)
  LinkedObject = -> Shape002
  Placement = pos=(219.95,-152.727,-3) rot=(0,0,1;0rad)
FEATURE [App::Link] __REFERENCE__LED_D3_0mm_null_ln_087  label="${REFERENCE}_LED_D3.0mm_null088"
  LinkPlacement = pos=(99.695,-58.801,0) rot=(0,0,1;0rad)
  LinkedObject = -> Shape
  Placement = pos=(99.695,-58.801,0) rot=(0,0,1;0rad)
FEATURE [App::Link] __REFERENCE__Body_null_2__ln_087  label="${REFERENCE}_Body_null[2]088"
  LinkPlacement = pos=(100.965,-58.801,0) rot=(0,0,1;0rad)
  LinkedObject = -> Shape001
  Placement = pos=(100.965,-58.801,0) rot=(0,0,1;0rad)
FEATURE [App::Link] __REFERENCE__LED_D5_0mm_null_ln_145  label="${REFERENCE}_LED_D5.0mm_null146"
  LinkPlacement = pos=(135.001,-113.411,-3) rot=(0,0,1;0rad)
  LinkedObject = -> Shape002
  Placement = pos=(135.001,-113.411,-3) rot=(0,0,1;0rad)
FEATURE [App::Link] __REFERENCE__LED_D5_0mm_null_ln_146  label="${REFERENCE}_LED_D5.0mm_null147"
  LinkPlacement = pos=(147.701,-119.761,-3) rot=(0,0,1;0rad)
  LinkedObject = -> Shape002
  Placement = pos=(147.701,-119.761,-3) rot=(0,0,1;0rad)
FEATURE [App::Link] __REFERENCE__LED_D3_0mm_null_ln_088  label="${REFERENCE}_LED_D3.0mm_null089"
  LinkPlacement = pos=(94.615,-175.641,0) rot=(0,0,1;0rad)
  LinkedObject = -> Shape
  Placement = pos=(94.615,-175.641,0) rot=(0,0,1;0rad)
FEATURE [App::Link] __REFERENCE__Body_null_2__ln_088  label="${REFERENCE}_Body_null[2]089"
  LinkPlacement = pos=(95.885,-175.641,0) rot=(0,0,1;0rad)
  LinkedObject = -> Shape001
  Placement = pos=(95.885,-175.641,0) rot=(0,0,1;0rad)
FEATURE [App::Link] __REFERENCE__LED_D3_0mm_null_ln_089  label="${REFERENCE}_LED_D3.0mm_null090"
  LinkPlacement = pos=(132.207,-185.801,0) rot=(0,0,1;0rad)
  LinkedObject = -> Shape
  Placement = pos=(132.207,-185.801,0) rot=(0,0,1;0rad)
FEATURE [App::Link] __REFERENCE__Body_null_2__ln_089  label="${REFERENCE}_Body_null[2]090"
  LinkPlacement = pos=(133.477,-185.801,0) rot=(0,0,1;0rad)
  LinkedObject = -> Shape001
  Placement = pos=(133.477,-185.801,0) rot=(0,0,1;0rad)
FEATURE [App::Link] __REFERENCE__LED_D5_0mm_null_ln_147  label="${REFERENCE}_LED_D5.0mm_null148"
  LinkPlacement = pos=(188.341,-132.461,-3) rot=(0,0,1;0rad)
  LinkedObject = -> Shape002
  Placement = pos=(188.341,-132.461,-3) rot=(0,0,1;0rad)
FEATURE [App::Link] __REFERENCE__LED_D5_0mm_null_ln_148  label="${REFERENCE}_LED_D5.0mm_null149"
  LinkPlacement = pos=(151.457,-18.3023,-3) rot=(0,0,1;0rad)
  LinkedObject = -> Shape002
  Placement = pos=(151.457,-18.3023,-3) rot=(0,0,1;0rad)
FEATURE [App::Link] __REFERENCE__LED_D3_0mm_null_ln_090  label="${REFERENCE}_LED_D3.0mm_null091"
  LinkPlacement = pos=(99.695,-160.401,0) rot=(0,0,1;0rad)
  LinkedObject = -> Shape
  Placement = pos=(99.695,-160.401,0) rot=(0,0,1;0rad)
FEATURE [App::Link] __REFERENCE__Body_null_2__ln_090  label="${REFERENCE}_Body_null[2]091"
  LinkPlacement = pos=(100.965,-160.401,0) rot=(0,0,1;0rad)
  LinkedObject = -> Shape001
  Placement = pos=(100.965,-160.401,0) rot=(0,0,1;0rad)
FEATURE [App::Link] __REFERENCE__LED_D5_0mm_null_ln_149  label="${REFERENCE}_LED_D5.0mm_null150"
  LinkPlacement = pos=(48.641,-132.461,-3) rot=(0,0,1;0rad)
  LinkedObject = -> Shape002
  Placement = pos=(48.641,-132.461,-3) rot=(0,0,1;0rad)
FEATURE [App::Link] __REFERENCE__LED_D3_0mm_null_ln_091  label="${REFERENCE}_LED_D3.0mm_null092"
  LinkPlacement = pos=(104.775,-68.961,0) rot=(0,0,1;0rad)
  LinkedObject = -> Shape
  Placement = pos=(104.775,-68.961,0) rot=(0,0,1;0rad)
FEATURE [App::Link] __REFERENCE__Body_null_2__ln_091  label="${REFERENCE}_Body_null[2]092"
  LinkPlacement = pos=(106.045,-68.961,0) rot=(0,0,1;0rad)
  LinkedObject = -> Shape001
  Placement = pos=(106.045,-68.961,0) rot=(0,0,1;0rad)
FEATURE [App::Link] __REFERENCE__LED_D3_0mm_null_ln_092  label="${REFERENCE}_LED_D3.0mm_null093"
  LinkPlacement = pos=(109.855,-48.641,0) rot=(0,0,1;0rad)
  LinkedObject = -> Shape
  Placement = pos=(109.855,-48.641,0) rot=(0,0,1;0rad)
FEATURE [App::Link] __REFERENCE__Body_null_2__ln_092  label="${REFERENCE}_Body_null[2]093"
  LinkPlacement = pos=(111.125,-48.641,0) rot=(0,0,1;0rad)
  LinkedObject = -> Shape001
  Placement = pos=(111.125,-48.641,0) rot=(0,0,1;0rad)
FEATURE [App::Link] __REFERENCE__LED_D3_0mm_null_ln_093  label="${REFERENCE}_LED_D3.0mm_null094"
  LinkPlacement = pos=(142.367,-53.721,0) rot=(0,0,1;0rad)
  LinkedObject = -> Shape
  Placement = pos=(142.367,-53.721,0) rot=(0,0,1;0rad)
FEATURE [App::Link] __REFERENCE__Body_null_2__ln_093  label="${REFERENCE}_Body_null[2]094"
  LinkPlacement = pos=(143.637,-53.721,0) rot=(0,0,1;0rad)
  LinkedObject = -> Shape001
  Placement = pos=(143.637,-53.721,0) rot=(0,0,1;0rad)
FEATURE [App::Link] __REFERENCE__LED_D3_0mm_null_ln_094  label="${REFERENCE}_LED_D3.0mm_null095"
  LinkPlacement = pos=(104.775,-190.881,0) rot=(0,0,1;0rad)
  LinkedObject = -> Shape
  Placement = pos=(104.775,-190.881,0) rot=(0,0,1;0rad)
FEATURE [App::Link] __REFERENCE__Body_null_2__ln_094  label="${REFERENCE}_Body_null[2]095"
  LinkPlacement = pos=(106.045,-190.881,0) rot=(0,0,1;0rad)
  LinkedObject = -> Shape001
  Placement = pos=(106.045,-190.881,0) rot=(0,0,1;0rad)
FEATURE [App::Link] __REFERENCE__LED_D3_0mm_null_ln_095  label="${REFERENCE}_LED_D3.0mm_null096"
  LinkPlacement = pos=(99.695,-175.641,0) rot=(0,0,1;0rad)
  LinkedObject = -> Shape
  Placement = pos=(99.695,-175.641,0) rot=(0,0,1;0rad)
FEATURE [App::Link] __REFERENCE__Body_null_2__ln_095  label="${REFERENCE}_Body_null[2]096"
  LinkPlacement = pos=(100.965,-175.641,0) rot=(0,0,1;0rad)
  LinkedObject = -> Shape001
  Placement = pos=(100.965,-175.641,0) rot=(0,0,1;0rad)
FEATURE [App::Link] __REFERENCE__LED_0805_2012Metric_null_ln_001  label="${REFERENCE}_LED_0805_2012Metric_null002"
  LinkPlacement = pos=(129.793,-3.75988,0) rot=(0,0,1;1.5708rad)
  LinkedObject = -> Shape005
  Placement = pos=(129.793,-3.75988,0) rot=(0,0,1;1.5708rad)
FEATURE [App::Link] __REFERENCE__R_0805_2012Metric_null_ln_008  label="${REFERENCE}_R_0805_2012Metric_null009"
  LinkPlacement = pos=(79.0448,-70.0024,0) rot=(0,0,1;0rad)
  LinkedObject = -> Shape003
  Placement = pos=(79.0448,-70.0024,0) rot=(0,0,1;0rad)
FEATURE [App::Link] __REFERENCE__LED_D3_0mm_null_ln_096  label="${REFERENCE}_LED_D3.0mm_null097"
  LinkPlacement = pos=(99.695,-79.121,0) rot=(0,0,1;0rad)
  LinkedObject = -> Shape
  Placement = pos=(99.695,-79.121,0) rot=(0,0,1;0rad)
FEATURE [App::Link] __REFERENCE__Body_null_2__ln_096  label="${REFERENCE}_Body_null[2]097"
  LinkPlacement = pos=(100.965,-79.121,0) rot=(0,0,1;0rad)
  LinkedObject = -> Shape001
  Placement = pos=(100.965,-79.121,0) rot=(0,0,1;0rad)
FEATURE [App::Link] __REFERENCE__LED_D3_0mm_null_ln_097  label="${REFERENCE}_LED_D3.0mm_null098"
  LinkPlacement = pos=(142.367,-180.721,0) rot=(0,0,1;0rad)
  LinkedObject = -> Shape
  Placement = pos=(142.367,-180.721,0) rot=(0,0,1;0rad)
FEATURE [App::Link] __REFERENCE__Body_null_2__ln_097  label="${REFERENCE}_Body_null[2]098"
  LinkPlacement = pos=(143.637,-180.721,0) rot=(0,0,1;0rad)
  LinkedObject = -> Shape001
  Placement = pos=(143.637,-180.721,0) rot=(0,0,1;0rad)
FEATURE [App::Link] __REFERENCE__LED_D3_0mm_null_ln_098  label="${REFERENCE}_LED_D3.0mm_null099"
  LinkPlacement = pos=(142.367,-48.641,0) rot=(0,0,1;0rad)
  LinkedObject = -> Shape
  Placement = pos=(142.367,-48.641,0) rot=(0,0,1;0rad)
FEATURE [App::Link] __REFERENCE__Body_null_2__ln_098  label="${REFERENCE}_Body_null[2]099"
  LinkPlacement = pos=(143.637,-48.641,0) rot=(0,0,1;0rad)
  LinkedObject = -> Shape001
  Placement = pos=(143.637,-48.641,0) rot=(0,0,1;0rad)
FEATURE [App::Link] __REFERENCE__LED_D3_0mm_null_ln_099  label="${REFERENCE}_LED_D3.0mm_null100"
  LinkPlacement = pos=(109.855,-58.801,0) rot=(0,0,1;0rad)
  LinkedObject = -> Shape
  Placement = pos=(109.855,-58.801,0) rot=(0,0,1;0rad)
FEATURE [App::Link] __REFERENCE__Body_null_2__ln_099  label="${REFERENCE}_Body_null[2]100"
  LinkPlacement = pos=(111.125,-58.801,0) rot=(0,0,1;0rad)
  LinkedObject = -> Shape001
  Placement = pos=(111.125,-58.801,0) rot=(0,0,1;0rad)
FEATURE [App::Link] __REFERENCE__LED_D5_0mm_null_ln_150  label="${REFERENCE}_LED_D5.0mm_null151"
  LinkPlacement = pos=(65.151,-212.149,-3) rot=(0,0,1;0rad)
  LinkedObject = -> Shape002
  Placement = pos=(65.151,-212.149,-3) rot=(0,0,1;0rad)
FEATURE [App::Link] __REFERENCE__LED_D5_0mm_null_ln_151  label="${REFERENCE}_LED_D5.0mm_null152"
  LinkPlacement = pos=(89.281,-126.111,-3) rot=(0,0,1;0rad)
  LinkedObject = -> Shape002
  Placement = pos=(89.281,-126.111,-3) rot=(0,0,1;0rad)
FEATURE [App::Link] __REFERENCE__LED_D5_0mm_null_ln_152  label="${REFERENCE}_LED_D5.0mm_null153"
  LinkPlacement = pos=(181.991,-126.111,-3) rot=(0,0,1;0rad)
  LinkedObject = -> Shape002
  Placement = pos=(181.991,-126.111,-3) rot=(0,0,1;0rad)
FEATURE [App::Link] __REFERENCE__LED_D5_0mm_null_ln_153  label="${REFERENCE}_LED_D5.0mm_null154"
  LinkPlacement = pos=(162.941,-100.711,-3) rot=(0,0,1;0rad)
  LinkedObject = -> Shape002
  Placement = pos=(162.941,-100.711,-3) rot=(0,0,1;0rad)
FEATURE [App::Link] __REFERENCE__LED_D5_0mm_null_ln_154  label="${REFERENCE}_LED_D5.0mm_null155"
  LinkPlacement = pos=(169.291,-100.711,-3) rot=(0,0,1;0rad)
  LinkedObject = -> Shape002
  Placement = pos=(169.291,-100.711,-3) rot=(0,0,1;0rad)
FEATURE [App::Link] __REFERENCE__LED_D3_0mm_null_ln_100  label="${REFERENCE}_LED_D3.0mm_null101"
  LinkPlacement = pos=(127.127,-190.881,0) rot=(0,0,1;0rad)
  LinkedObject = -> Shape
  Placement = pos=(127.127,-190.881,0) rot=(0,0,1;0rad)
FEATURE [App::Link] __REFERENCE__Body_null_2__ln_100  label="${REFERENCE}_Body_null[2]101"
  LinkPlacement = pos=(128.397,-190.881,0) rot=(0,0,1;0rad)
  LinkedObject = -> Shape001
  Placement = pos=(128.397,-190.881,0) rot=(0,0,1;0rad)
FEATURE [App::Link] __REFERENCE__C_0805_2012Metric_null_ln_008  label="${REFERENCE}_C_0805_2012Metric_null009"
  LinkPlacement = pos=(125.361,-91.761,0) rot=(0,0,-1;1.5708rad)
  LinkedObject = -> Shape004
  Placement = pos=(125.361,-91.761,0) rot=(0,0,-1;1.5708rad)
FEATURE [App::Link] __REFERENCE__LED_D5_0mm_null_ln_155  label="${REFERENCE}_LED_D5.0mm_null156"
  LinkPlacement = pos=(162.941,-107.061,-3) rot=(0,0,1;0rad)
  LinkedObject = -> Shape002
  Placement = pos=(162.941,-107.061,-3) rot=(0,0,1;0rad)
FEATURE [App::Link] __REFERENCE__LED_D3_0mm_null_ln_101  label="${REFERENCE}_LED_D3.0mm_null102"
  LinkPlacement = pos=(114.935,-53.721,0) rot=(0,0,1;0rad)
  LinkedObject = -> Shape
  Placement = pos=(114.935,-53.721,0) rot=(0,0,1;0rad)
FEATURE [App::Link] __REFERENCE__Body_null_2__ln_101  label="${REFERENCE}_Body_null[2]102"
  LinkPlacement = pos=(116.205,-53.721,0) rot=(0,0,1;0rad)
  LinkedObject = -> Shape001
  Placement = pos=(116.205,-53.721,0) rot=(0,0,1;0rad)
FEATURE [App::Link] __REFERENCE__LED_D3_0mm_null_ln_102  label="${REFERENCE}_LED_D3.0mm_null103"
  LinkPlacement = pos=(137.287,-175.641,0) rot=(0,0,1;0rad)
  LinkedObject = -> Shape
  Placement = pos=(137.287,-175.641,0) rot=(0,0,1;0rad)
FEATURE [App::Link] __REFERENCE__Body_null_2__ln_102  label="${REFERENCE}_Body_null[2]103"
  LinkPlacement = pos=(138.557,-175.641,0) rot=(0,0,1;0rad)
  LinkedObject = -> Shape001
  Placement = pos=(138.557,-175.641,0) rot=(0,0,1;0rad)
FEATURE [App::Link] __REFERENCE__LED_D5_0mm_null_ln_156  label="${REFERENCE}_LED_D5.0mm_null157"
  LinkPlacement = pos=(67.691,-138.811,-3) rot=(0,0,1;0rad)
  LinkedObject = -> Shape002
  Placement = pos=(67.691,-138.811,-3) rot=(0,0,1;0rad)
FEATURE [App::Link] __REFERENCE__LED_D5_0mm_null_ln_157  label="${REFERENCE}_LED_D5.0mm_null158"
  LinkPlacement = pos=(48.641,-100.711,-3) rot=(0,0,1;0rad)
  LinkedObject = -> Shape002
  Placement = pos=(48.641,-100.711,-3) rot=(0,0,1;0rad)
FEATURE [App::Link] __REFERENCE__LED_D3_0mm_null_ln_103  label="${REFERENCE}_LED_D3.0mm_null104"
  LinkPlacement = pos=(137.287,-180.721,0) rot=(0,0,1;0rad)
  LinkedObject = -> Shape
  Placement = pos=(137.287,-180.721,0) rot=(0,0,1;0rad)
FEATURE [App::Link] __REFERENCE__Body_null_2__ln_103  label="${REFERENCE}_Body_null[2]104"
  LinkPlacement = pos=(138.557,-180.721,0) rot=(0,0,1;0rad)
  LinkedObject = -> Shape001
  Placement = pos=(138.557,-180.721,0) rot=(0,0,1;0rad)
FEATURE [App::Link] __REFERENCE__LED_D5_0mm_null_ln_158  label="${REFERENCE}_LED_D5.0mm_null159"
  LinkPlacement = pos=(204.279,-70.231,-3) rot=(0,0,1;0rad)
  LinkedObject = -> Shape002
  Placement = pos=(204.279,-70.231,-3) rot=(0,0,1;0rad)
FEATURE [App::Link] __REFERENCE__C_0805_2012Metric_null_ln_009  label="${REFERENCE}_C_0805_2012Metric_null010"
  LinkPlacement = pos=(212.446,-115.214,0) rot=(0,0,1;1.5708rad)
  LinkedObject = -> Shape004
  Placement = pos=(212.446,-115.214,0) rot=(0,0,1;1.5708rad)
FEATURE [App::Link] __REFERENCE__LED_D3_0mm_null_ln_104  label="${REFERENCE}_LED_D3.0mm_null105"
  LinkPlacement = pos=(99.695,-74.041,0) rot=(0,0,1;0rad)
  LinkedObject = -> Shape
  Placement = pos=(99.695,-74.041,0) rot=(0,0,1;0rad)
FEATURE [App::Link] __REFERENCE__Body_null_2__ln_104  label="${REFERENCE}_Body_null[2]105"
  LinkPlacement = pos=(100.965,-74.041,0) rot=(0,0,1;0rad)
  LinkedObject = -> Shape001
  Placement = pos=(100.965,-74.041,0) rot=(0,0,1;0rad)
FEATURE [App::Link] __REFERENCE__LED_D5_0mm_null_ln_159  label="${REFERENCE}_LED_D5.0mm_null160"
  LinkPlacement = pos=(215.948,-163.152,-3) rot=(0,0,1;0rad)
  LinkedObject = -> Shape002
  Placement = pos=(215.948,-163.152,-3) rot=(0,0,1;0rad)
FEATURE [App::Link] __REFERENCE__LED_D5_0mm_null_ln_160  label="${REFERENCE}_LED_D5.0mm_null161"
  LinkPlacement = pos=(61.341,-100.711,-3) rot=(0,0,1;0rad)
  LinkedObject = -> Shape002
  Placement = pos=(61.341,-100.711,-3) rot=(0,0,1;0rad)
FEATURE [App::Link] __REFERENCE__LED_D5_0mm_null_ln_161  label="${REFERENCE}_LED_D5.0mm_null162"
  LinkPlacement = pos=(85.5251,-18.3023,-3) rot=(0,0,1;0rad)
  LinkedObject = -> Shape002
  Placement = pos=(85.5251,-18.3023,-3) rot=(0,0,1;0rad)
FEATURE [App::Link] __REFERENCE__LED_D5_0mm_null_ln_162  label="${REFERENCE}_LED_D5.0mm_null163"
  LinkPlacement = pos=(75.1003,-22.304,-3) rot=(0,0,1;0rad)
  LinkedObject = -> Shape002
  Placement = pos=(75.1003,-22.304,-3) rot=(0,0,1;0rad)
FEATURE [App::Link] __REFERENCE__LED_D5_0mm_null_ln_163  label="${REFERENCE}_LED_D5.0mm_null164"
  LinkPlacement = pos=(48.641,-126.111,-3) rot=(0,0,1;0rad)
  LinkedObject = -> Shape002
  Placement = pos=(48.641,-126.111,-3) rot=(0,0,1;0rad)
FEATURE [App::Link] __REFERENCE__LED_D3_0mm_null_ln_105  label="${REFERENCE}_LED_D3.0mm_null106"
  LinkPlacement = pos=(99.695,-68.961,0) rot=(0,0,1;0rad)
  LinkedObject = -> Shape
  Placement = pos=(99.695,-68.961,0) rot=(0,0,1;0rad)
FEATURE [App::Link] __REFERENCE__Body_null_2__ln_105  label="${REFERENCE}_Body_null[2]106"
  LinkPlacement = pos=(100.965,-68.961,0) rot=(0,0,1;0rad)
  LinkedObject = -> Shape001
  Placement = pos=(100.965,-68.961,0) rot=(0,0,1;0rad)
FEATURE [App::Link] __REFERENCE__LED_D5_0mm_null_ln_164  label="${REFERENCE}_LED_D5.0mm_null165"
  LinkPlacement = pos=(82.931,-100.711,-3) rot=(0,0,1;0rad)
  LinkedObject = -> Shape002
  Placement = pos=(82.931,-100.711,-3) rot=(0,0,1;0rad)
FEATURE [App::Link] __REFERENCE__LED_D5_0mm_null_ln_165  label="${REFERENCE}_LED_D5.0mm_null166"
  LinkPlacement = pos=(74.041,-126.111,-3) rot=(0,0,1;0rad)
  LinkedObject = -> Shape002
  Placement = pos=(74.041,-126.111,-3) rot=(0,0,1;0rad)
FEATURE [App::Link] __REFERENCE__LED_D5_0mm_null_ln_166  label="${REFERENCE}_LED_D5.0mm_null167"
  LinkPlacement = pos=(222.84,-97.581,-3) rot=(0,0,1;0rad)
  LinkedObject = -> Shape002
  Placement = pos=(222.84,-97.581,-3) rot=(0,0,1;0rad)
FEATURE [App::Link] __REFERENCE__LED_D5_0mm_null_ln_167  label="${REFERENCE}_LED_D5.0mm_null168"
  LinkPlacement = pos=(181.991,-107.061,-3) rot=(0,0,1;0rad)
  LinkedObject = -> Shape002
  Placement = pos=(181.991,-107.061,-3) rot=(0,0,1;0rad)
FEATURE [App::Link] __REFERENCE__LED_D5_0mm_null_ln_168  label="${REFERENCE}_LED_D5.0mm_null169"
  LinkPlacement = pos=(82.931,-132.461,-3) rot=(0,0,1;0rad)
  LinkedObject = -> Shape002
  Placement = pos=(82.931,-132.461,-3) rot=(0,0,1;0rad)
FEATURE [App::Link] __REFERENCE__LED_D5_0mm_null_ln_169  label="${REFERENCE}_LED_D5.0mm_null170"
  LinkPlacement = pos=(162.941,-138.811,-3) rot=(0,0,1;0rad)
  LinkedObject = -> Shape002
  Placement = pos=(162.941,-138.811,-3) rot=(0,0,1;0rad)
FEATURE [App::Link] __REFERENCE__LED_D3_0mm_null_ln_106  label="${REFERENCE}_LED_D3.0mm_null107"
  LinkPlacement = pos=(127.127,-68.961,0) rot=(0,0,1;0rad)
  LinkedObject = -> Shape
  Placement = pos=(127.127,-68.961,0) rot=(0,0,1;0rad)
FEATURE [App::Link] __REFERENCE__Body_null_2__ln_106  label="${REFERENCE}_Body_null[2]107"
  LinkPlacement = pos=(128.397,-68.961,0) rot=(0,0,1;0rad)
  LinkedObject = -> Shape001
  Placement = pos=(128.397,-68.961,0) rot=(0,0,1;0rad)
FEATURE [App::Link] __REFERENCE__LED_D3_0mm_null_ln_107  label="${REFERENCE}_LED_D3.0mm_null108"
  LinkPlacement = pos=(132.207,-180.721,0) rot=(0,0,1;0rad)
  LinkedObject = -> Shape
  Placement = pos=(132.207,-180.721,0) rot=(0,0,1;0rad)
FEATURE [App::Link] __REFERENCE__Body_null_2__ln_107  label="${REFERENCE}_Body_null[2]108"
  LinkPlacement = pos=(133.477,-180.721,0) rot=(0,0,1;0rad)
  LinkedObject = -> Shape001
  Placement = pos=(133.477,-180.721,0) rot=(0,0,1;0rad)
FEATURE [App::Link] __REFERENCE__LED_D3_0mm_null_ln_108  label="${REFERENCE}_LED_D3.0mm_null109"
  LinkPlacement = pos=(104.775,-74.041,0) rot=(0,0,1;0rad)
  LinkedObject = -> Shape
  Placement = pos=(104.775,-74.041,0) rot=(0,0,1;0rad)
FEATURE [App::Link] __REFERENCE__Body_null_2__ln_108  label="${REFERENCE}_Body_null[2]109"
  LinkPlacement = pos=(106.045,-74.041,0) rot=(0,0,1;0rad)
  LinkedObject = -> Shape001
  Placement = pos=(106.045,-74.041,0) rot=(0,0,1;0rad)
FEATURE [App::Link] __REFERENCE__LED_D5_0mm_null_ln_170  label="${REFERENCE}_LED_D5.0mm_null171"
  LinkPlacement = pos=(61.341,-107.061,-3) rot=(0,0,1;0rad)
  LinkedObject = -> Shape002
  Placement = pos=(61.341,-107.061,-3) rot=(0,0,1;0rad)
FEATURE [App::Link] __REFERENCE__LED_D5_0mm_null_ln_171  label="${REFERENCE}_LED_D5.0mm_null172"
  LinkPlacement = pos=(141.351,-107.061,-3) rot=(0,0,1;0rad)
  LinkedObject = -> Shape002
  Placement = pos=(141.351,-107.061,-3) rot=(0,0,1;0rad)
FEATURE [App::Link] __REFERENCE__LED_D5_0mm_null_ln_172  label="${REFERENCE}_LED_D5.0mm_null173"
  LinkPlacement = pos=(128.651,-119.761,-3) rot=(0,0,1;0rad)
  LinkedObject = -> Shape002
  Placement = pos=(128.651,-119.761,-3) rot=(0,0,1;0rad)
FEATURE [App::Link] __REFERENCE__R_0805_2012Metric_null_ln_009  label="${REFERENCE}_R_0805_2012Metric_null010"
  LinkPlacement = pos=(169.291,-69.977,0) rot=(0,0,1;0rad)
  LinkedObject = -> Shape003
  Placement = pos=(169.291,-69.977,0) rot=(0,0,1;0rad)
FEATURE [App::Link] __REFERENCE__LED_D3_0mm_null_ln_109  label="${REFERENCE}_LED_D3.0mm_null110"
  LinkPlacement = pos=(122.047,-53.721,0) rot=(0,0,1;0rad)
  LinkedObject = -> Shape
  Placement = pos=(122.047,-53.721,0) rot=(0,0,1;0rad)
FEATURE [App::Link] __REFERENCE__Body_null_2__ln_109  label="${REFERENCE}_Body_null[2]110"
  LinkPlacement = pos=(123.317,-53.721,0) rot=(0,0,1;0rad)
  LinkedObject = -> Shape001
  Placement = pos=(123.317,-53.721,0) rot=(0,0,1;0rad)
FEATURE [App::Link] __REFERENCE__LED_D5_0mm_null_ln_173  label="${REFERENCE}_LED_D5.0mm_null174"
  LinkPlacement = pos=(175.641,-132.461,-3) rot=(0,0,1;0rad)
  LinkedObject = -> Shape002
  Placement = pos=(175.641,-132.461,-3) rot=(0,0,1;0rad)
FEATURE [App::Link] __REFERENCE__LED_D5_0mm_null_ln_174  label="${REFERENCE}_LED_D5.0mm_null175"
  LinkPlacement = pos=(95.631,-100.711,-3) rot=(0,0,1;0rad)
  LinkedObject = -> Shape002
  Placement = pos=(95.631,-100.711,-3) rot=(0,0,1;0rad)
FEATURE [App::Link] __REFERENCE__C_0805_2012Metric_null_ln_010  label="${REFERENCE}_C_0805_2012Metric_null011"
  LinkPlacement = pos=(68.2752,-174.752,0) rot=(0,0,-1;1.5708rad)
  LinkedObject = -> Shape004
  Placement = pos=(68.2752,-174.752,0) rot=(0,0,-1;1.5708rad)
FEATURE [App::Link] __REFERENCE__LED_D5_0mm_null_ln_175  label="${REFERENCE}_LED_D5.0mm_null176"
  LinkPlacement = pos=(135.001,-138.811,-3) rot=(0,0,1;0rad)
  LinkedObject = -> Shape002
  Placement = pos=(135.001,-138.811,-3) rot=(0,0,1;0rad)
FEATURE [App::Link] __REFERENCE__LED_D5_0mm_null_ln_176  label="${REFERENCE}_LED_D5.0mm_null177"
  LinkPlacement = pos=(67.691,-119.761,-3) rot=(0,0,1;0rad)
  LinkedObject = -> Shape002
  Placement = pos=(67.691,-119.761,-3) rot=(0,0,1;0rad)
FEATURE [App::Link] __REFERENCE__LED_D3_0mm_null_ln_110  label="${REFERENCE}_LED_D3.0mm_null111"
  LinkPlacement = pos=(109.855,-79.121,0) rot=(0,0,1;0rad)
  LinkedObject = -> Shape
  Placement = pos=(109.855,-79.121,0) rot=(0,0,1;0rad)
FEATURE [App::Link] __REFERENCE__Body_null_2__ln_110  label="${REFERENCE}_Body_null[2]111"
  LinkPlacement = pos=(111.125,-79.121,0) rot=(0,0,1;0rad)
  LinkedObject = -> Shape001
  Placement = pos=(111.125,-79.121,0) rot=(0,0,1;0rad)
FEATURE [App::Link] __REFERENCE__LED_D5_0mm_null_ln_177  label="${REFERENCE}_LED_D5.0mm_null178"
  LinkPlacement = pos=(197.77,-48.3781,-3) rot=(0,0,1;0rad)
  LinkedObject = -> Shape002
  Placement = pos=(197.77,-48.3781,-3) rot=(0,0,1;0rad)
FEATURE [App::Link] __REFERENCE__LED_D5_0mm_null_ln_178  label="${REFERENCE}_LED_D5.0mm_null179"
  LinkPlacement = pos=(95.631,-119.761,-3) rot=(0,0,1;0rad)
  LinkedObject = -> Shape002
  Placement = pos=(95.631,-119.761,-3) rot=(0,0,1;0rad)
FEATURE [App::Link] __REFERENCE__LED_D5_0mm_null_ln_179  label="${REFERENCE}_LED_D5.0mm_null180"
  LinkPlacement = pos=(47.1081,-40.4823,-3) rot=(0,0,1;0rad)
  LinkedObject = -> Shape002
  Placement = pos=(47.1081,-40.4823,-3) rot=(0,0,1;0rad)
FEATURE [App::Link] __REFERENCE__LED_D5_0mm_null_ln_180  label="${REFERENCE}_LED_D5.0mm_null181"
  LinkPlacement = pos=(217.551,-119.761,-3) rot=(0,0,1;0rad)
  LinkedObject = -> Shape002
  Placement = pos=(217.551,-119.761,-3) rot=(0,0,1;0rad)
FEATURE [App::Link] __REFERENCE__LED_D5_0mm_null_ln_181  label="${REFERENCE}_LED_D5.0mm_null182"
  LinkPlacement = pos=(169.291,-119.761,-3) rot=(0,0,1;0rad)
  LinkedObject = -> Shape002
  Placement = pos=(169.291,-119.761,-3) rot=(0,0,1;0rad)
FEATURE [App::Link] __REFERENCE__LED_D3_0mm_null_ln_111  label="${REFERENCE}_LED_D3.0mm_null112"
  LinkPlacement = pos=(122.047,-63.881,0) rot=(0,0,1;0rad)
  LinkedObject = -> Shape
  Placement = pos=(122.047,-63.881,0) rot=(0,0,1;0rad)
FEATURE [App::Link] __REFERENCE__Body_null_2__ln_111  label="${REFERENCE}_Body_null[2]112"
  LinkPlacement = pos=(123.317,-63.881,0) rot=(0,0,1;0rad)
  LinkedObject = -> Shape001
  Placement = pos=(123.317,-63.881,0) rot=(0,0,1;0rad)
FEATURE [App::Link] __REFERENCE__LED_D3_0mm_null_ln_112  label="${REFERENCE}_LED_D3.0mm_null113"
  LinkPlacement = pos=(132.207,-48.641,0) rot=(0,0,1;0rad)
  LinkedObject = -> Shape
  Placement = pos=(132.207,-48.641,0) rot=(0,0,1;0rad)
FEATURE [App::Link] __REFERENCE__Body_null_2__ln_112  label="${REFERENCE}_Body_null[2]113"
  LinkPlacement = pos=(133.477,-48.641,0) rot=(0,0,1;0rad)
  LinkedObject = -> Shape001
  Placement = pos=(133.477,-48.641,0) rot=(0,0,1;0rad)
FEATURE [App::Link] __REFERENCE__LED_D5_0mm_null_ln_182  label="${REFERENCE}_LED_D5.0mm_null183"
  LinkPlacement = pos=(128.651,-138.811,-3) rot=(0,0,1;0rad)
  LinkedObject = -> Shape002
  Placement = pos=(128.651,-138.811,-3) rot=(0,0,1;0rad)
FEATURE [App::Link] __REFERENCE__LED_D3_0mm_null_ln_113  label="${REFERENCE}_LED_D3.0mm_null114"
  LinkPlacement = pos=(127.127,-170.561,0) rot=(0,0,1;0rad)
  LinkedObject = -> Shape
  Placement = pos=(127.127,-170.561,0) rot=(0,0,1;0rad)
FEATURE [App::Link] __REFERENCE__Body_null_2__ln_113  label="${REFERENCE}_Body_null[2]114"
  LinkPlacement = pos=(128.397,-170.561,0) rot=(0,0,1;0rad)
  LinkedObject = -> Shape001
  Placement = pos=(128.397,-170.561,0) rot=(0,0,1;0rad)
FEATURE [App::Link] __REFERENCE__LED_D5_0mm_null_ln_183  label="${REFERENCE}_LED_D5.0mm_null184"
  LinkPlacement = pos=(181.196,-206.067,-3) rot=(0,0,1;0rad)
  LinkedObject = -> Shape002
  Placement = pos=(181.196,-206.067,-3) rot=(0,0,1;0rad)
FEATURE [App::Link] __REFERENCE__LED_D5_0mm_null_ln_184  label="${REFERENCE}_LED_D5.0mm_null185"
  LinkPlacement = pos=(188.341,-119.761,-3) rot=(0,0,1;0rad)
  LinkedObject = -> Shape002
  Placement = pos=(188.341,-119.761,-3) rot=(0,0,1;0rad)
FEATURE [App::Link] __REFERENCE__LED_D5_0mm_null_ln_185  label="${REFERENCE}_LED_D5.0mm_null186"
  LinkPlacement = pos=(54.991,-107.061,-3) rot=(0,0,1;0rad)
  LinkedObject = -> Shape002
  Placement = pos=(54.991,-107.061,-3) rot=(0,0,1;0rad)
FEATURE [App::Link] __REFERENCE__LED_D3_0mm_null_ln_114  label="${REFERENCE}_LED_D3.0mm_null115"
  LinkPlacement = pos=(137.287,-58.801,0) rot=(0,0,1;0rad)
  LinkedObject = -> Shape
  Placement = pos=(137.287,-58.801,0) rot=(0,0,1;0rad)
FEATURE [App::Link] __REFERENCE__Body_null_2__ln_114  label="${REFERENCE}_Body_null[2]115"
  LinkPlacement = pos=(138.557,-58.801,0) rot=(0,0,1;0rad)
  LinkedObject = -> Shape001
  Placement = pos=(138.557,-58.801,0) rot=(0,0,1;0rad)
FEATURE [App::Link] __REFERENCE__LED_D3_0mm_null_ln_115  label="${REFERENCE}_LED_D3.0mm_null116"
  LinkPlacement = pos=(137.287,-165.481,0) rot=(0,0,1;0rad)
  LinkedObject = -> Shape
  Placement = pos=(137.287,-165.481,0) rot=(0,0,1;0rad)
FEATURE [App::Link] __REFERENCE__Body_null_2__ln_115  label="${REFERENCE}_Body_null[2]116"
  LinkPlacement = pos=(138.557,-165.481,0) rot=(0,0,1;0rad)
  LinkedObject = -> Shape001
  Placement = pos=(138.557,-165.481,0) rot=(0,0,1;0rad)
FEATURE [App::Link] __REFERENCE__LED_D5_0mm_null_ln_186  label="${REFERENCE}_LED_D5.0mm_null187"
  LinkPlacement = pos=(61.341,-113.411,-3) rot=(0,0,1;0rad)
  LinkedObject = -> Shape002
  Placement = pos=(61.341,-113.411,-3) rot=(0,0,1;0rad)
FEATURE [App::Link] __REFERENCE__LED_D5_0mm_null_ln_187  label="${REFERENCE}_LED_D5.0mm_null188"
  LinkPlacement = pos=(17.0323,-152.727,-3) rot=(0,0,1;0rad)
  LinkedObject = -> Shape002
  Placement = pos=(17.0323,-152.727,-3) rot=(0,0,1;0rad)
FEATURE [App::Link] __REFERENCE__LED_D3_0mm_null_ln_116  label="${REFERENCE}_LED_D3.0mm_null117"
  LinkPlacement = pos=(122.047,-74.041,0) rot=(0,0,1;0rad)
  LinkedObject = -> Shape
  Placement = pos=(122.047,-74.041,0) rot=(0,0,1;0rad)
FEATURE [App::Link] __REFERENCE__Body_null_2__ln_116  label="${REFERENCE}_Body_null[2]117"
  LinkPlacement = pos=(123.317,-74.041,0) rot=(0,0,1;0rad)
  LinkedObject = -> Shape001
  Placement = pos=(123.317,-74.041,0) rot=(0,0,1;0rad)
FEATURE [App::Link] __REFERENCE__LED_D5_0mm_null_ln_188  label="${REFERENCE}_LED_D5.0mm_null189"
  LinkPlacement = pos=(107.34,-13.6654,-3) rot=(0,0,1;0rad)
  LinkedObject = -> Shape002
  Placement = pos=(107.34,-13.6654,-3) rot=(0,0,1;0rad)
FEATURE [App::Link] __REFERENCE__LED_D3_0mm_null_ln_117  label="${REFERENCE}_LED_D3.0mm_null118"
  LinkPlacement = pos=(109.855,-63.881,0) rot=(0,0,1;0rad)
  LinkedObject = -> Shape
  Placement = pos=(109.855,-63.881,0) rot=(0,0,1;0rad)
FEATURE [App::Link] __REFERENCE__Body_null_2__ln_117  label="${REFERENCE}_Body_null[2]118"
  LinkPlacement = pos=(111.125,-63.881,0) rot=(0,0,1;0rad)
  LinkedObject = -> Shape001
  Placement = pos=(111.125,-63.881,0) rot=(0,0,1;0rad)
FEATURE [App::Link] __REFERENCE__LED_D5_0mm_null_ln_189  label="${REFERENCE}_LED_D5.0mm_null190"
  LinkPlacement = pos=(169.291,-107.061,-3) rot=(0,0,1;0rad)
  LinkedObject = -> Shape002
  Placement = pos=(169.291,-107.061,-3) rot=(0,0,1;0rad)
FEATURE [App::Link] __REFERENCE__LED_D3_0mm_null_ln_118  label="${REFERENCE}_LED_D3.0mm_null119"
  LinkPlacement = pos=(99.695,-165.481,0) rot=(0,0,1;0rad)
  LinkedObject = -> Shape
  Placement = pos=(99.695,-165.481,0) rot=(0,0,1;0rad)
FEATURE [App::Link] __REFERENCE__Body_null_2__ln_118  label="${REFERENCE}_Body_null[2]119"
  LinkPlacement = pos=(100.965,-165.481,0) rot=(0,0,1;0rad)
  LinkedObject = -> Shape001
  Placement = pos=(100.965,-165.481,0) rot=(0,0,1;0rad)
FEATURE [App::Link] __REFERENCE__LED_D5_0mm_null_ln_190  label="${REFERENCE}_LED_D5.0mm_null191"
  LinkPlacement = pos=(175.641,-113.411,-3) rot=(0,0,1;0rad)
  LinkedObject = -> Shape002
  Placement = pos=(175.641,-113.411,-3) rot=(0,0,1;0rad)
FEATURE [App::Link] __REFERENCE__LED_D3_0mm_null_ln_119  label="${REFERENCE}_LED_D3.0mm_null120"
  LinkPlacement = pos=(114.935,-170.561,0) rot=(0,0,1;0rad)
  LinkedObject = -> Shape
  Placement = pos=(114.935,-170.561,0) rot=(0,0,1;0rad)
FEATURE [App::Link] __REFERENCE__Body_null_2__ln_119  label="${REFERENCE}_Body_null[2]120"
  LinkPlacement = pos=(116.205,-170.561,0) rot=(0,0,1;0rad)
  LinkedObject = -> Shape001
  Placement = pos=(116.205,-170.561,0) rot=(0,0,1;0rad)
FEATURE [App::Link] __REFERENCE__LED_0805_2012Metric_null_ln_002  label="${REFERENCE}_LED_0805_2012Metric_null003"
  LinkPlacement = pos=(149.859,-3.75988,0) rot=(0,0,1;1.5708rad)
  LinkedObject = -> Shape005
  Placement = pos=(149.859,-3.75988,0) rot=(0,0,1;1.5708rad)
FEATURE [App::Link] __REFERENCE__LED_D5_0mm_null_ln_191  label="${REFERENCE}_LED_D5.0mm_null192"
  LinkPlacement = pos=(108.331,-138.811,-3) rot=(0,0,1;0rad)
  LinkedObject = -> Shape002
  Placement = pos=(108.331,-138.811,-3) rot=(0,0,1;0rad)
FEATURE [App::Link] __REFERENCE__LED_D3_0mm_null_ln_120  label="${REFERENCE}_LED_D3.0mm_null121"
  LinkPlacement = pos=(114.935,-160.401,0) rot=(0,0,1;0rad)
  LinkedObject = -> Shape
  Placement = pos=(114.935,-160.401,0) rot=(0,0,1;0rad)
FEATURE [App::Link] __REFERENCE__Body_null_2__ln_120  label="${REFERENCE}_Body_null[2]121"
  LinkPlacement = pos=(116.205,-160.401,0) rot=(0,0,1;0rad)
  LinkedObject = -> Shape001
  Placement = pos=(116.205,-160.401,0) rot=(0,0,1;0rad)
FEATURE [App::Link] __REFERENCE__LED_D5_0mm_null_ln_192  label="${REFERENCE}_LED_D5.0mm_null193"
  LinkPlacement = pos=(26.1034,-66.421,-3) rot=(0,0,1;0rad)
  LinkedObject = -> Shape002
  Placement = pos=(26.1034,-66.421,-3) rot=(0,0,1;0rad)
FEATURE [App::Link] __REFERENCE__LED_D5_0mm_null_ln_193  label="${REFERENCE}_LED_D5.0mm_null194"
  LinkPlacement = pos=(61.341,-119.761,-3) rot=(0,0,1;0rad)
  LinkedObject = -> Shape002
  Placement = pos=(61.341,-119.761,-3) rot=(0,0,1;0rad)
FEATURE [App::Link] __REFERENCE__LED_D5_0mm_null_ln_194  label="${REFERENCE}_LED_D5.0mm_null195"
  LinkPlacement = pos=(219.95,-86.7951,-3) rot=(0,0,1;0rad)
  LinkedObject = -> Shape002
  Placement = pos=(219.95,-86.7951,-3) rot=(0,0,1;0rad)
FEATURE [App::Link] __REFERENCE__LED_D5_0mm_null_ln_195  label="${REFERENCE}_LED_D5.0mm_null196"
  LinkPlacement = pos=(128.651,-107.061,-3) rot=(0,0,1;0rad)
  LinkedObject = -> Shape002
  Placement = pos=(128.651,-107.061,-3) rot=(0,0,1;0rad)
FEATURE [App::Link] __REFERENCE__LED_D3_0mm_null_ln_121  label="${REFERENCE}_LED_D3.0mm_null122"
  LinkPlacement = pos=(142.367,-165.481,0) rot=(0,0,1;0rad)
  LinkedObject = -> Shape
  Placement = pos=(142.367,-165.481,0) rot=(0,0,1;0rad)
FEATURE [App::Link] __REFERENCE__Body_null_2__ln_121  label="${REFERENCE}_Body_null[2]122"
  LinkPlacement = pos=(143.637,-165.481,0) rot=(0,0,1;0rad)
  LinkedObject = -> Shape001
  Placement = pos=(143.637,-165.481,0) rot=(0,0,1;0rad)
FEATURE [App::Link] __REFERENCE__LED_D3_0mm_null_ln_122  label="${REFERENCE}_LED_D3.0mm_null123"
  LinkPlacement = pos=(142.367,-175.641,0) rot=(0,0,1;0rad)
  LinkedObject = -> Shape
  Placement = pos=(142.367,-175.641,0) rot=(0,0,1;0rad)
FEATURE [App::Link] __REFERENCE__Body_null_2__ln_122  label="${REFERENCE}_Body_null[2]123"
  LinkPlacement = pos=(143.637,-175.641,0) rot=(0,0,1;0rad)
  LinkedObject = -> Shape001
  Placement = pos=(143.637,-175.641,0) rot=(0,0,1;0rad)
FEATURE [App::Link] __REFERENCE__LED_D3_0mm_null_ln_123  label="${REFERENCE}_LED_D3.0mm_null124"
  LinkPlacement = pos=(114.935,-74.041,0) rot=(0,0,1;0rad)
  LinkedObject = -> Shape
  Placement = pos=(114.935,-74.041,0) rot=(0,0,1;0rad)
FEATURE [App::Link] __REFERENCE__Body_null_2__ln_123  label="${REFERENCE}_Body_null[2]124"
  LinkPlacement = pos=(116.205,-74.041,0) rot=(0,0,1;0rad)
  LinkedObject = -> Shape001
  Placement = pos=(116.205,-74.041,0) rot=(0,0,1;0rad)
FEATURE [App::Link] __REFERENCE__LED_D5_0mm_null_ln_196  label="${REFERENCE}_LED_D5.0mm_null197"
  LinkPlacement = pos=(168.021,-33.9725,-3) rot=(0,0,1;0rad)
  LinkedObject = -> Shape002
  Placement = pos=(168.021,-33.9725,-3) rot=(0,0,1;0rad)
FEATURE [App::Link] __REFERENCE__LED_D5_0mm_null_ln_197  label="${REFERENCE}_LED_D5.0mm_null198"
  LinkPlacement = pos=(147.701,-113.411,-3) rot=(0,0,1;0rad)
  LinkedObject = -> Shape002
  Placement = pos=(147.701,-113.411,-3) rot=(0,0,1;0rad)
FEATURE [App::Link] __REFERENCE__LED_D5_0mm_null_ln_198  label="${REFERENCE}_LED_D5.0mm_null199"
  LinkPlacement = pos=(74.041,-138.811,-3) rot=(0,0,1;0rad)
  LinkedObject = -> Shape002
  Placement = pos=(74.041,-138.811,-3) rot=(0,0,1;0rad)
FEATURE [App::Link] __REFERENCE__LED_D5_0mm_null_ln_199  label="${REFERENCE}_LED_D5.0mm_null200"
  LinkPlacement = pos=(224.587,-130.912,-3) rot=(0,0,1;0rad)
  LinkedObject = -> Shape002
  Placement = pos=(224.587,-130.912,-3) rot=(0,0,1;0rad)
FEATURE [App::Link] __REFERENCE__LED_D5_0mm_null_ln_200  label="${REFERENCE}_LED_D5.0mm_null201"
  LinkPlacement = pos=(128.651,-126.111,-3) rot=(0,0,1;0rad)
  LinkedObject = -> Shape002
  Placement = pos=(128.651,-126.111,-3) rot=(0,0,1;0rad)
FEATURE [App::Link] __REFERENCE__LED_D3_0mm_null_ln_124  label="${REFERENCE}_LED_D3.0mm_null125"
  LinkPlacement = pos=(127.127,-63.881,0) rot=(0,0,1;0rad)
  LinkedObject = -> Shape
  Placement = pos=(127.127,-63.881,0) rot=(0,0,1;0rad)
FEATURE [App::Link] __REFERENCE__Body_null_2__ln_124  label="${REFERENCE}_Body_null[2]125"
  LinkPlacement = pos=(128.397,-63.881,0) rot=(0,0,1;0rad)
  LinkedObject = -> Shape001
  Placement = pos=(128.397,-63.881,0) rot=(0,0,1;0rad)
FEATURE [App::Link] __REFERENCE__LED_D5_0mm_null_ln_201  label="${REFERENCE}_LED_D5.0mm_null202"
  LinkPlacement = pos=(89.281,-100.711,-3) rot=(0,0,1;0rad)
  LinkedObject = -> Shape002
  Placement = pos=(89.281,-100.711,-3) rot=(0,0,1;0rad)
FEATURE [App::Link] __REFERENCE__LED_D5_0mm_null_ln_202  label="${REFERENCE}_LED_D5.0mm_null203"
  LinkPlacement = pos=(54.991,-126.111,-3) rot=(0,0,1;0rad)
  LinkedObject = -> Shape002
  Placement = pos=(54.991,-126.111,-3) rot=(0,0,1;0rad)
FEATURE [App::Link] __REFERENCE__LED_D3_0mm_null_ln_125  label="${REFERENCE}_LED_D3.0mm_null126"
  LinkPlacement = pos=(109.855,-175.641,0) rot=(0,0,1;0rad)
  LinkedObject = -> Shape
  Placement = pos=(109.855,-175.641,0) rot=(0,0,1;0rad)
FEATURE [App::Link] __REFERENCE__Body_null_2__ln_125  label="${REFERENCE}_Body_null[2]126"
  LinkPlacement = pos=(111.125,-175.641,0) rot=(0,0,1;0rad)
  LinkedObject = -> Shape001
  Placement = pos=(111.125,-175.641,0) rot=(0,0,1;0rad)
FEATURE [App::Link] __REFERENCE__LED_D5_0mm_null_ln_203  label="${REFERENCE}_LED_D5.0mm_null204"
  LinkPlacement = pos=(171.831,-212.149,-3) rot=(0,0,1;0rad)
  LinkedObject = -> Shape002
  Placement = pos=(171.831,-212.149,-3) rot=(0,0,1;0rad)
FEATURE [App::Link] __REFERENCE__LED_D3_0mm_null_ln_126  label="${REFERENCE}_LED_D3.0mm_null127"
  LinkPlacement = pos=(127.127,-185.801,0) rot=(0,0,1;0rad)
  LinkedObject = -> Shape
  Placement = pos=(127.127,-185.801,0) rot=(0,0,1;0rad)
FEATURE [App::Link] __REFERENCE__Body_null_2__ln_126  label="${REFERENCE}_Body_null[2]127"
  LinkPlacement = pos=(128.397,-185.801,0) rot=(0,0,1;0rad)
  LinkedObject = -> Shape001
  Placement = pos=(128.397,-185.801,0) rot=(0,0,1;0rad)
FEATURE [App::Link] __REFERENCE__LED_D3_0mm_null_ln_127  label="${REFERENCE}_LED_D3.0mm_null128"
  LinkPlacement = pos=(132.207,-160.401,0) rot=(0,0,1;0rad)
  LinkedObject = -> Shape
  Placement = pos=(132.207,-160.401,0) rot=(0,0,1;0rad)
FEATURE [App::Link] __REFERENCE__Body_null_2__ln_127  label="${REFERENCE}_Body_null[2]128"
  LinkPlacement = pos=(133.477,-160.401,0) rot=(0,0,1;0rad)
  LinkedObject = -> Shape001
  Placement = pos=(133.477,-160.401,0) rot=(0,0,1;0rad)
FEATURE [App::Link] __REFERENCE__LED_D5_0mm_null_ln_204  label="${REFERENCE}_LED_D5.0mm_null205"
  LinkPlacement = pos=(68.961,-33.9725,-3) rot=(0,0,1;0rad)
  LinkedObject = -> Shape002
  Placement = pos=(68.961,-33.9725,-3) rot=(0,0,1;0rad)
FEATURE [App::Link] __REFERENCE__LED_D3_0mm_null_ln_128  label="${REFERENCE}_LED_D3.0mm_null129"
  LinkPlacement = pos=(114.935,-185.801,0) rot=(0,0,1;0rad)
  LinkedObject = -> Shape
  Placement = pos=(114.935,-185.801,0) rot=(0,0,1;0rad)
FEATURE [App::Link] __REFERENCE__Body_null_2__ln_128  label="${REFERENCE}_Body_null[2]129"
  LinkPlacement = pos=(116.205,-185.801,0) rot=(0,0,1;0rad)
  LinkedObject = -> Shape001
  Placement = pos=(116.205,-185.801,0) rot=(0,0,1;0rad)
FEATURE [App::Link] __REFERENCE__LED_D3_0mm_null_ln_129  label="${REFERENCE}_LED_D3.0mm_null130"
  LinkPlacement = pos=(137.287,-74.041,0) rot=(0,0,1;0rad)
  LinkedObject = -> Shape
  Placement = pos=(137.287,-74.041,0) rot=(0,0,1;0rad)
FEATURE [App::Link] __REFERENCE__Body_null_2__ln_129  label="${REFERENCE}_Body_null[2]130"
  LinkPlacement = pos=(138.557,-74.041,0) rot=(0,0,1;0rad)
  LinkedObject = -> Shape001
  Placement = pos=(138.557,-74.041,0) rot=(0,0,1;0rad)
FEATURE [App::Link] __REFERENCE__LED_D3_0mm_null_ln_130  label="${REFERENCE}_LED_D3.0mm_null131"
  LinkPlacement = pos=(109.855,-165.481,0) rot=(0,0,1;0rad)
  LinkedObject = -> Shape
  Placement = pos=(109.855,-165.481,0) rot=(0,0,1;0rad)
FEATURE [App::Link] __REFERENCE__Body_null_2__ln_130  label="${REFERENCE}_Body_null[2]131"
  LinkPlacement = pos=(111.125,-165.481,0) rot=(0,0,1;0rad)
  LinkedObject = -> Shape001
  Placement = pos=(111.125,-165.481,0) rot=(0,0,1;0rad)
FEATURE [App::Link] __REFERENCE__LED_D5_0mm_null_ln_205  label="${REFERENCE}_LED_D5.0mm_null206"
  LinkPlacement = pos=(118.491,-13.081,-3) rot=(0,0,1;0rad)
  LinkedObject = -> Shape002
  Placement = pos=(118.491,-13.081,-3) rot=(0,0,1;0rad)
FEATURE [App::Link] __REFERENCE__LED_D3_0mm_null_ln_131  label="${REFERENCE}_LED_D3.0mm_null132"
  LinkPlacement = pos=(127.127,-74.041,0) rot=(0,0,1;0rad)
  LinkedObject = -> Shape
  Placement = pos=(127.127,-74.041,0) rot=(0,0,1;0rad)
FEATURE [App::Link] __REFERENCE__Body_null_2__ln_131  label="${REFERENCE}_Body_null[2]132"
  LinkPlacement = pos=(128.397,-74.041,0) rot=(0,0,1;0rad)
  LinkedObject = -> Shape001
  Placement = pos=(128.397,-74.041,0) rot=(0,0,1;0rad)
FEATURE [App::Link] __REFERENCE__LED_D3_0mm_null_ln_132  label="${REFERENCE}_LED_D3.0mm_null133"
  LinkPlacement = pos=(114.935,-175.641,0) rot=(0,0,1;0rad)
  LinkedObject = -> Shape
  Placement = pos=(114.935,-175.641,0) rot=(0,0,1;0rad)
FEATURE [App::Link] __REFERENCE__Body_null_2__ln_132  label="${REFERENCE}_Body_null[2]133"
  LinkPlacement = pos=(116.205,-175.641,0) rot=(0,0,1;0rad)
  LinkedObject = -> Shape001
  Placement = pos=(116.205,-175.641,0) rot=(0,0,1;0rad)
FEATURE [App::Link] __REFERENCE__LED_D3_0mm_null_ln_133  label="${REFERENCE}_LED_D3.0mm_null134"
  LinkPlacement = pos=(122.047,-175.641,0) rot=(0,0,1;0rad)
  LinkedObject = -> Shape
  Placement = pos=(122.047,-175.641,0) rot=(0,0,1;0rad)
FEATURE [App::Link] __REFERENCE__Body_null_2__ln_133  label="${REFERENCE}_Body_null[2]134"
  LinkPlacement = pos=(123.317,-175.641,0) rot=(0,0,1;0rad)
  LinkedObject = -> Shape001
  Placement = pos=(123.317,-175.641,0) rot=(0,0,1;0rad)
FEATURE [App::Link] __REFERENCE__LED_D5_0mm_null_ln_206  label="${REFERENCE}_LED_D5.0mm_null207"
  LinkPlacement = pos=(162.941,-132.461,-3) rot=(0,0,1;0rad)
  LinkedObject = -> Shape002
  Placement = pos=(162.941,-132.461,-3) rot=(0,0,1;0rad)
FEATURE [App::Link] __REFERENCE__LED_D5_0mm_null_ln_207  label="${REFERENCE}_LED_D5.0mm_null208"
  LinkPlacement = pos=(181.991,-132.461,-3) rot=(0,0,1;0rad)
  LinkedObject = -> Shape002
  Placement = pos=(181.991,-132.461,-3) rot=(0,0,1;0rad)
FEATURE [App::Link] __REFERENCE__LED_D3_0mm_null_ln_134  label="${REFERENCE}_LED_D3.0mm_null135"
  LinkPlacement = pos=(114.935,-63.881,0) rot=(0,0,1;0rad)
  LinkedObject = -> Shape
  Placement = pos=(114.935,-63.881,0) rot=(0,0,1;0rad)
FEATURE [App::Link] __REFERENCE__Body_null_2__ln_134  label="${REFERENCE}_Body_null[2]135"
  LinkPlacement = pos=(116.205,-63.881,0) rot=(0,0,1;0rad)
  LinkedObject = -> Shape001
  Placement = pos=(116.205,-63.881,0) rot=(0,0,1;0rad)
FEATURE [App::Link] __REFERENCE__LED_D3_0mm_null_ln_135  label="${REFERENCE}_LED_D3.0mm_null136"
  LinkPlacement = pos=(137.287,-63.881,0) rot=(0,0,1;0rad)
  LinkedObject = -> Shape
  Placement = pos=(137.287,-63.881,0) rot=(0,0,1;0rad)
FEATURE [App::Link] __REFERENCE__Body_null_2__ln_135  label="${REFERENCE}_Body_null[2]136"
  LinkPlacement = pos=(138.557,-63.881,0) rot=(0,0,1;0rad)
  LinkedObject = -> Shape001
  Placement = pos=(138.557,-63.881,0) rot=(0,0,1;0rad)
FEATURE [App::Link] __REFERENCE__LED_D5_0mm_null_ln_208  label="${REFERENCE}_LED_D5.0mm_null209"
  LinkPlacement = pos=(48.641,-107.061,-3) rot=(0,0,1;0rad)
  LinkedObject = -> Shape002
  Placement = pos=(48.641,-107.061,-3) rot=(0,0,1;0rad)
FEATURE [App::Link] __REFERENCE__C_0805_2012Metric_null_ln_011  label="${REFERENCE}_C_0805_2012Metric_null012"
  LinkPlacement = pos=(44.7548,-116.332,0) rot=(0,0,-1;1.5708rad)
  LinkedObject = -> Shape004
  Placement = pos=(44.7548,-116.332,0) rot=(0,0,-1;1.5708rad)
FEATURE [App::Link] __REFERENCE__LED_D5_0mm_null_ln_209  label="${REFERENCE}_LED_D5.0mm_null210"
  LinkPlacement = pos=(101.981,-119.761,-3) rot=(0,0,1;0rad)
  LinkedObject = -> Shape002
  Placement = pos=(101.981,-119.761,-3) rot=(0,0,1;0rad)
FEATURE [App::Link] __REFERENCE__LED_D3_0mm_null_ln_136  label="${REFERENCE}_LED_D3.0mm_null137"
  LinkPlacement = pos=(132.207,-68.961,0) rot=(0,0,1;0rad)
  LinkedObject = -> Shape
  Placement = pos=(132.207,-68.961,0) rot=(0,0,1;0rad)
FEATURE [App::Link] __REFERENCE__Body_null_2__ln_136  label="${REFERENCE}_Body_null[2]137"
  LinkPlacement = pos=(133.477,-68.961,0) rot=(0,0,1;0rad)
  LinkedObject = -> Shape001
  Placement = pos=(133.477,-68.961,0) rot=(0,0,1;0rad)
FEATURE [App::Link] __REFERENCE__LED_D5_0mm_null_ln_210  label="${REFERENCE}_LED_D5.0mm_null211"
  LinkPlacement = pos=(101.981,-132.461,-3) rot=(0,0,1;0rad)
  LinkedObject = -> Shape002
  Placement = pos=(101.981,-132.461,-3) rot=(0,0,1;0rad)
FEATURE [Part::Feature] Shape006  label="${REFERENCE}_VEML7700-TR_null"
  Placement = pos=(119.761,-91.94,0.8) rot=(0,0.707107,0.707107;3.14159rad)
  shape: bbox 6.8 x 3.002 x 2.352 mm, 92 faces, 5 solids (baked)
FEATURE [App::Link] __REFERENCE__LED_D3_0mm_null_ln_137  label="${REFERENCE}_LED_D3.0mm_null138"
  LinkPlacement = pos=(142.367,-79.121,0) rot=(0,0,1;0rad)
  LinkedObject = -> Shape
  Placement = pos=(142.367,-79.121,0) rot=(0,0,1;0rad)
FEATURE [App::Link] __REFERENCE__Body_null_2__ln_137  label="${REFERENCE}_Body_null[2]138"
  LinkPlacement = pos=(143.637,-79.121,0) rot=(0,0,1;0rad)
  LinkedObject = -> Shape001
  Placement = pos=(143.637,-79.121,0) rot=(0,0,1;0rad)
FEATURE [App::Link] __REFERENCE__LED_D5_0mm_null_ln_211  label="${REFERENCE}_LED_D5.0mm_null212"
  LinkPlacement = pos=(89.281,-138.811,-3) rot=(0,0,1;0rad)
  LinkedObject = -> Shape002
  Placement = pos=(89.281,-138.811,-3) rot=(0,0,1;0rad)
FEATURE [App::Link] __REFERENCE__LED_D5_0mm_null_ln_212  label="${REFERENCE}_LED_D5.0mm_null213"
  LinkPlacement = pos=(154.051,-113.411,-3) rot=(0,0,1;0rad)
  LinkedObject = -> Shape002
  Placement = pos=(154.051,-113.411,-3) rot=(0,0,1;0rad)
FEATURE [App::Link] __REFERENCE__LED_D3_0mm_null_ln_138  label="${REFERENCE}_LED_D3.0mm_null139"
  LinkPlacement = pos=(114.935,-165.481,0) rot=(0,0,1;0rad)
  LinkedObject = -> Shape
  Placement = pos=(114.935,-165.481,0) rot=(0,0,1;0rad)
FEATURE [App::Link] __REFERENCE__Body_null_2__ln_138  label="${REFERENCE}_Body_null[2]139"
  LinkPlacement = pos=(116.205,-165.481,0) rot=(0,0,1;0rad)
  LinkedObject = -> Shape001
  Placement = pos=(116.205,-165.481,0) rot=(0,0,1;0rad)
FEATURE [App::Part] Top_7181
  Group = -> [Shape,Shape001,__REFERENCE__LED_D3_0mm_null_ln_,__REFERENCE__Body_null_2__ln_,Shape002,__REFERENCE__LED_D5_0mm_null_ln_,__REFERENCE__LED_D5_0mm_null_ln_001,__REFERENCE__LED_D5_0mm_null_ln_002,__REFERENCE__LED_D5_0mm_null_ln_003,__REFERENCE__LED_D5_0mm_null_ln_004,__REFERENCE__LED_D5_0mm_null_ln_005,__REFERENCE__LED_D5_0mm_null_ln_006,__REFERENCE__LED_D5_0mm_null_ln_007,+510 more]
  Origin = -> Origin003
FEATURE [App::Link] __REFERENCE__R_0805_2012Metric_null_ln_010  label="${REFERENCE}_R_0805_2012Metric_null011"
  LinkPlacement = pos=(196.342,-16.891,-1.6) rot=(0.707107,0.707107,0;3.14159rad)
  LinkedObject = -> Shape003
  Placement = pos=(196.342,-16.891,-1.6) rot=(0.707107,0.707107,0;3.14159rad)
FEATURE [App::Link] __REFERENCE__R_0805_2012Metric_null_ln_011  label="${REFERENCE}_R_0805_2012Metric_null012"
  LinkPlacement = pos=(196.342,-13.208,-1.6) rot=(0.707107,-0.707107,0;3.14159rad)
  LinkedObject = -> Shape003
  Placement = pos=(196.342,-13.208,-1.6) rot=(0.707107,-0.707107,0;3.14159rad)
FEATURE [Part::Feature] Shape007  label="${REFERENCE}_HTSSOP_28_1EP_44x97mm_P065mm_null"
  Placement = pos=(74.761,-174.761,-1.6) rot=(0.707107,0.707107,0;3.14159rad)
  shape: bbox 9.7 x 6.4 x 1.2 mm, 461 faces (baked)
FEATURE [Part::Feature] Shape008  label="${REFERENCE}_SOT_223_null"
  Placement = pos=(194.761,-84.761,-1.6) rot=(0.707107,0.707107,0;3.14159rad)
  shape: bbox 6.5 x 7 x 1.7 mm, 78 faces (baked)
FEATURE [App::Link] __REFERENCE__R_0805_2012Metric_null_ln_012  label="${REFERENCE}_R_0805_2012Metric_null013"
  LinkPlacement = pos=(220.218,-27.94,-1.6) rot=(0.707107,-0.707107,0;3.14159rad)
  LinkedObject = -> Shape003
  Placement = pos=(220.218,-27.94,-1.6) rot=(0.707107,-0.707107,0;3.14159rad)
FEATURE [App::Link] __REFERENCE__C_0805_2012Metric_null_ln_012  label="${REFERENCE}_C_0805_2012Metric_null013"
  LinkPlacement = pos=(17.018,-166.116,-1.6) rot=(0.707107,-0.707107,0;3.14159rad)
  LinkedObject = -> Shape004
  Placement = pos=(17.018,-166.116,-1.6) rot=(0.707107,-0.707107,0;3.14159rad)
FEATURE [Part::Feature] Shape009  label="${REFERENCE}_Keystone_1058_1x2032_null"
  Placement = pos=(24.13,-39.116,-1.6) rot=(1,0,0;3.14159rad)
  shape: bbox 31.86 x 17.97 x 5.08 mm, 99 faces (baked)
FEATURE [Part::Feature] Shape010  label="${REFERENCE}_CP_Elec_18x175_null"
  Placement = pos=(12.7,-185.42,-1.6) rot=(0.707107,-0.707107,0;3.14159rad)
  shape: bbox 24.31 x 24.3 x 17.5 mm, 41 faces (baked)
FEATURE [Part::Feature] Shape011  label="${REFERENCE}_SW_SPST_TL3301_6x6mm_H4.3mm_null"
  Placement = pos=(228.6,-44.069,-1.6) rot=(0,1,0;3.14159rad)
  shape: bbox 10.05 x 6 x 4.3 mm, 81 faces, 11 solids (baked)
FEATURE [Part::Feature] Shape012  label="${REFERENCE}_SMA_Amphenol_132291-12_Vertical_null"
  Placement = pos=(14.732,-19.431,-1.6) rot=(0,1,0;3.14159rad)
  shape: bbox 7 x 7 x 20.24 mm, 137 faces (baked)
FEATURE [App::Link] __REFERENCE__SOT_223_null_ln_  label="${REFERENCE}_SOT_223_null001"
  LinkPlacement = pos=(11.557,-163.068,-1.6) rot=(0.707107,0.707107,0;3.14159rad)
  LinkedObject = -> Shape008
  Placement = pos=(11.557,-163.068,-1.6) rot=(0.707107,0.707107,0;3.14159rad)
FEATURE [App::Link] __REFERENCE__R_0805_2012Metric_null_ln_013  label="${REFERENCE}_R_0805_2012Metric_null014"
  LinkPlacement = pos=(220.218,-24.257,-1.6) rot=(0.707107,-0.707107,0;3.14159rad)
  LinkedObject = -> Shape003
  Placement = pos=(220.218,-24.257,-1.6) rot=(0.707107,-0.707107,0;3.14159rad)
FEATURE [Part::Feature] Shape013  label="${REFERENCE}_ESP32-WROVER-B_null"
  Placement = pos=(208.32,-16.155,-1.6) rot=(0,0.707107,-0.707107;3.14159rad)
  shape: bbox 18 x 31.4 x 3.8 mm, 853 faces, 46 solids (baked)
FEATURE [App::Link] __REFERENCE__HTSSOP_28_1EP_44x97mm_P065mm_null_ln_  label="${REFERENCE}_HTSSOP_28_1EP_44x97mm_P065mm_null001"
  LinkPlacement = pos=(119.761,-204.761,-1.6) rot=(0.707107,0.707107,0;3.14159rad)
  LinkedObject = -> Shape007
  Placement = pos=(119.761,-204.761,-1.6) rot=(0.707107,0.707107,0;3.14159rad)
FEATURE [App::Link] __REFERENCE__C_0805_2012Metric_null_ln_013  label="${REFERENCE}_C_0805_2012Metric_null014"
  LinkPlacement = pos=(14.986,-12.954,-1.6) rot=(1,0,0;3.14159rad)
  LinkedObject = -> Shape004
  Placement = pos=(14.986,-12.954,-1.6) rot=(1,0,0;3.14159rad)
FEATURE [App::Link] __REFERENCE__CP_Elec_18x175_null_ln_  label="${REFERENCE}_CP_Elec_18x175_null001"
  LinkPlacement = pos=(62.738,-12.446,-1.6) rot=(1,0,0;3.14159rad)
  LinkedObject = -> Shape010
  Placement = pos=(62.738,-12.446,-1.6) rot=(1,0,0;3.14159rad)
FEATURE [Part::Feature] Shape014  label="${REFERENCE}_DC044_connector_5.5x2.1mm_null"
  Placement = pos=(22.86,-204.692,-1.6) rot=(0.707107,-0.707107,0;3.14159rad)
  shape: bbox 9.5 x 11.5 x 9.7 mm, 54 faces, 5 solids (baked)
FEATURE [App::Link] __REFERENCE__SW_SPST_TL3301_6x6mm_H4_3mm_null_ln_  label="${REFERENCE}_SW_SPST_TL3301_6x6mm_H4.3mm_null001"
  LinkPlacement = pos=(228.6,-34.29,-1.6) rot=(0,1,0;3.14159rad)
  LinkedObject = -> Shape011
  Placement = pos=(228.6,-34.29,-1.6) rot=(0,1,0;3.14159rad)
FEATURE [App::Link] __REFERENCE__R_0805_2012Metric_null_ln_014  label="${REFERENCE}_R_0805_2012Metric_null015"
  LinkPlacement = pos=(196.342,-27.94,-1.6) rot=(0.707107,0.707107,0;3.14159rad)
  LinkedObject = -> Shape003
  Placement = pos=(196.342,-27.94,-1.6) rot=(0.707107,0.707107,0;3.14159rad)
FEATURE [App::Link] __REFERENCE__C_0805_2012Metric_null_ln_014  label="${REFERENCE}_C_0805_2012Metric_null015"
  LinkPlacement = pos=(192.786,-90.932,-1.6) rot=(1,0,0;3.14159rad)
  LinkedObject = -> Shape004
  Placement = pos=(192.786,-90.932,-1.6) rot=(1,0,0;3.14159rad)
FEATURE [App::Link] __REFERENCE__R_0805_2012Metric_null_ln_015  label="${REFERENCE}_R_0805_2012Metric_null016"
  LinkPlacement = pos=(41.91,-214.884,-1.6) rot=(0.707107,0.707107,0;3.14159rad)
  LinkedObject = -> Shape003
  Placement = pos=(41.91,-214.884,-1.6) rot=(0.707107,0.707107,0;3.14159rad)
FEATURE [Part::Feature] Shape015  label="${REFERENCE}_D_SMA_null"
  Placement = pos=(36.83,-214.884,-1.6) rot=(0,1,0;3.14159rad)
  shape: bbox 5 x 2.7 x 2.22 mm, 41 faces (baked)
FEATURE [App::Link] __REFERENCE__R_0805_2012Metric_null_ln_016  label="${REFERENCE}_R_0805_2012Metric_null017"
  LinkPlacement = pos=(22.479,-16.917,-1.6) rot=(0,1,0;3.14159rad)
  LinkedObject = -> Shape003
  Placement = pos=(22.479,-16.917,-1.6) rot=(0,1,0;3.14159rad)
FEATURE [App::Link] __REFERENCE__C_0805_2012Metric_null_ln_015  label="${REFERENCE}_C_0805_2012Metric_null016"
  LinkPlacement = pos=(81.717,-157.811,-1.6) rot=(1,0,0;3.14159rad)
  LinkedObject = -> Shape004
  Placement = pos=(81.717,-157.811,-1.6) rot=(1,0,0;3.14159rad)
FEATURE [App::Link] __REFERENCE__C_0805_2012Metric_null_ln_016  label="${REFERENCE}_C_0805_2012Metric_null017"
  LinkPlacement = pos=(22.479,-21.971,-1.6) rot=(0,1,0;3.14159rad)
  LinkedObject = -> Shape004
  Placement = pos=(22.479,-21.971,-1.6) rot=(0,1,0;3.14159rad)
FEATURE [App::Link] __REFERENCE__HTSSOP_28_1EP_44x97mm_P065mm_null_ln_001  label="${REFERENCE}_HTSSOP_28_1EP_44x97mm_P065mm_null002"
  LinkPlacement = pos=(164.761,-174.761,-1.6) rot=(0.707107,0.707107,0;3.14159rad)
  LinkedObject = -> Shape007
  Placement = pos=(164.761,-174.761,-1.6) rot=(0.707107,0.707107,0;3.14159rad)
FEATURE [App::Link] __REFERENCE__C_0805_2012Metric_null_ln_017  label="${REFERENCE}_C_0805_2012Metric_null018"
  LinkPlacement = pos=(220.218,-9.525,-1.6) rot=(0.707107,0.707107,0;3.14159rad)
  LinkedObject = -> Shape004
  Placement = pos=(220.218,-9.525,-1.6) rot=(0.707107,0.707107,0;3.14159rad)
FEATURE [Part::Feature] Shape016  label="${REFERENCE}_Inductor_Coilcraft_0805CS_null"
  Placement = pos=(22.479,-19.429,-1.6) rot=(1,0,0;3.14159rad)
  shape: bbox 2.29 x 1.73 x 1.52 mm, 38 faces, 3 solids (baked)
FEATURE [App::Link] __REFERENCE__R_0805_2012Metric_null_ln_017  label="${REFERENCE}_R_0805_2012Metric_null018"
  LinkPlacement = pos=(196.342,-24.257,-1.6) rot=(0.707107,0.707107,0;3.14159rad)
  LinkedObject = -> Shape003
  Placement = pos=(196.342,-24.257,-1.6) rot=(0.707107,0.707107,0;3.14159rad)
FEATURE [App::Link] __REFERENCE__C_0805_2012Metric_null_ln_018  label="${REFERENCE}_C_0805_2012Metric_null019"
  LinkPlacement = pos=(224.663,-9.525,-1.6) rot=(0.707107,0.707107,0;3.14159rad)
  LinkedObject = -> Shape004
  Placement = pos=(224.663,-9.525,-1.6) rot=(0.707107,0.707107,0;3.14159rad)
FEATURE [Part::Feature] Shape017  label="${REFERENCE}_PinHeader_1x06_P127mm_Vertical_null"
  Placement = pos=(47.498,-6.985,-1.6) rot=(0,1,0;3.14159rad)
  shape: bbox 2.1 x 7.62 x 6.3 mm, 148 faces (baked)
FEATURE [Part::Feature] Shape018  label="${REFERENCE}_Fuse_MXT250_With_Socket_null"
  Placement = pos=(7.112,-202.692,-1.6) rot=(0.707107,-0.707107,0;3.14159rad)
  shape: bbox 9.5 x 9.5 x 15.5 mm, 27 faces, 8 solids (baked)
FEATURE [Part::Feature] Shape019  label="${REFERENCE}_Fuse_MXT250_null[2]"
  Placement = pos=(7.112,-202.692,-1.6) rot=(0.707107,-0.707107,0;3.14159rad)
  shape: bbox 9.5 x 9.5 x 15.1 mm, 12 faces, 3 solids (baked)
FEATURE [App::Link] __REFERENCE__C_0805_2012Metric_null_ln_019  label="${REFERENCE}_C_0805_2012Metric_null020"
  LinkPlacement = pos=(10.287,-168.656,-1.6) rot=(1,0,0;3.14159rad)
  LinkedObject = -> Shape004
  Placement = pos=(10.287,-168.656,-1.6) rot=(1,0,0;3.14159rad)
FEATURE [App::Link] __REFERENCE__R_0805_2012Metric_null_ln_018  label="${REFERENCE}_R_0805_2012Metric_null019"
  LinkPlacement = pos=(220.218,-16.901,-1.6) rot=(0.707107,0.707107,0;3.14159rad)
  LinkedObject = -> Shape003
  Placement = pos=(220.218,-16.901,-1.6) rot=(0.707107,0.707107,0;3.14159rad)
FEATURE [App::Link] __REFERENCE__R_0805_2012Metric_null_ln_019  label="${REFERENCE}_R_0805_2012Metric_null020"
  LinkPlacement = pos=(196.342,-20.574,-1.6) rot=(0.707107,-0.707107,0;3.14159rad)
  LinkedObject = -> Shape003
  Placement = pos=(196.342,-20.574,-1.6) rot=(0.707107,-0.707107,0;3.14159rad)
FEATURE [Part::Feature] Shape020  label="${REFERENCE}_PE5393NSL_inductor_null"
  Placement = pos=(58.674,-227.076,-1.6) rot=(0.707107,0.707107,0;3.14159rad)
  shape: bbox 15.24 x 15.24 x 9.91 mm, 162 faces, 4 solids (baked)
FEATURE [App::Link] __REFERENCE__C_0805_2012Metric_null_ln_020  label="${REFERENCE}_C_0805_2012Metric_null021"
  LinkPlacement = pos=(77.907,-157.811,-1.6) rot=(1,0,0;3.14159rad)
  LinkedObject = -> Shape004
  Placement = pos=(77.907,-157.811,-1.6) rot=(1,0,0;3.14159rad)
FEATURE [App::Link] __REFERENCE__C_0805_2012Metric_null_ln_021  label="${REFERENCE}_C_0805_2012Metric_null022"
  LinkPlacement = pos=(196.596,-90.932,-1.6) rot=(1,0,0;3.14159rad)
  LinkedObject = -> Shape004
  Placement = pos=(196.596,-90.932,-1.6) rot=(1,0,0;3.14159rad)
FEATURE [App::Link] __REFERENCE__CP_Elec_18x175_null_ln_001  label="${REFERENCE}_CP_Elec_18x175_null002"
  LinkPlacement = pos=(12.446,-62.23,-1.6) rot=(0.707107,-0.707107,0;3.14159rad)
  LinkedObject = -> Shape010
  Placement = pos=(12.446,-62.23,-1.6) rot=(0.707107,-0.707107,0;3.14159rad)
FEATURE [Part::Feature] Shape021  label="${REFERENCE}_MAX6952EAX+_null"
  Placement = pos=(34.761,-119.761,-1.6) rot=(0,1,0;3.14159rad)
  shape: bbox 10.31 x 15.38 x 2.64 mm, 492 faces, 37 solids (baked)
FEATURE [App::Link] __REFERENCE__R_0805_2012Metric_null_ln_020  label="${REFERENCE}_R_0805_2012Metric_null021"
  LinkPlacement = pos=(220.218,-13.223,-1.6) rot=(0.707107,0.707107,0;3.14159rad)
  LinkedObject = -> Shape003
  Placement = pos=(220.218,-13.223,-1.6) rot=(0.707107,0.707107,0;3.14159rad)
FEATURE [App::Link] __REFERENCE__R_0805_2012Metric_null_ln_021  label="${REFERENCE}_R_0805_2012Metric_null022"
  LinkPlacement = pos=(196.342,-9.525,-1.6) rot=(0.707107,-0.707107,0;3.14159rad)
  LinkedObject = -> Shape003
  Placement = pos=(196.342,-9.525,-1.6) rot=(0.707107,-0.707107,0;3.14159rad)
FEATURE [Part::Feature] Shape022  label="${REFERENCE}_PogoFemale_null"
  Placement = pos=(191.865,-8.723,-1.6) rot=(-0.57735,0.57735,-0.57735;2.0944rad)
  shape: bbox 4 x 24.44 x 5.5 mm, 69 faces, 7 solids (baked)
FEATURE [App::Link] __REFERENCE__R_0805_2012Metric_null_ln_022  label="${REFERENCE}_R_0805_2012Metric_null023"
  LinkPlacement = pos=(46.99,-214.884,-1.6) rot=(0.707107,0.707107,0;3.14159rad)
  LinkedObject = -> Shape003
  Placement = pos=(46.99,-214.884,-1.6) rot=(0.707107,0.707107,0;3.14159rad)
FEATURE [Part::Feature] Shape023  label="${REFERENCE}_LM2596DSADJR4G_null"
  Placement = pos=(41.148,-232.817,-2.3) rot=(-1,0,0;1.5708rad)
  shape: bbox 10.24 x 14.71 x 5.104 mm, 168 faces, 7 solids (baked)
FEATURE [App::Link] __REFERENCE__MAX6952EAX__null_ln_  label="${REFERENCE}_MAX6952EAX+_null001"
  LinkPlacement = pos=(204.761,-119.761,-1.6) rot=(0,1,0;3.14159rad)
  LinkedObject = -> Shape021
  Placement = pos=(204.761,-119.761,-1.6) rot=(0,1,0;3.14159rad)
FEATURE [Part::Feature] Shape024  label="${REFERENCE}_Ublox_LEA_M8T_null"
  Placement = pos=(34.29,-14.732,-1.6) rot=(0,1,0;3.14159rad)
  shape: bbox 17 x 22.4 x 2.4 mm, 374 faces, 30 solids (baked)
FEATURE [App::Link] __REFERENCE__SOT_223_null_ln_001  label="${REFERENCE}_SOT_223_null002"
  LinkPlacement = pos=(79.869,-151.663,-1.6) rot=(0.707107,0.707107,0;3.14159rad)
  LinkedObject = -> Shape008
  Placement = pos=(79.869,-151.663,-1.6) rot=(0.707107,0.707107,0;3.14159rad)
FEATURE [App::Link] __REFERENCE__HTSSOP_28_1EP_44x97mm_P065mm_null_ln_002  label="${REFERENCE}_HTSSOP_28_1EP_44x97mm_P065mm_null003"
  LinkPlacement = pos=(74.761,-64.761,-1.6) rot=(0.707107,-0.707107,0;3.14159rad)
  LinkedObject = -> Shape007
  Placement = pos=(74.761,-64.761,-1.6) rot=(0.707107,-0.707107,0;3.14159rad)
FEATURE [App::Link] __REFERENCE__C_0805_2012Metric_null_ln_022  label="${REFERENCE}_C_0805_2012Metric_null023"
  LinkPlacement = pos=(44.45,-214.884,-1.6) rot=(0.707107,0.707107,0;3.14159rad)
  LinkedObject = -> Shape004
  Placement = pos=(44.45,-214.884,-1.6) rot=(0.707107,0.707107,0;3.14159rad)
FEATURE [Part::Feature] Shape025  label="${REFERENCE}_CP_Elec_8x10_null"
  Placement = pos=(34.036,-205.232,-1.6) rot=(0.707107,0.707107,0;3.14159rad)
  shape: bbox 10.92 x 10.73 x 10 mm, 41 faces (baked)
FEATURE [Part::Feature] Shape026  label="${REFERENCE}_TP094003_Transducer_9x9mm_null"
  Placement = pos=(229.743,-14.2875,-1.6) rot=(0,1,0;3.14159rad)
  shape: bbox 9 x 9 x 1.9 mm, 56 faces, 4 solids (baked)
FEATURE [App::Link] __REFERENCE__C_0805_2012Metric_null_ln_023  label="${REFERENCE}_C_0805_2012Metric_null024"
  LinkPlacement = pos=(22.352,-14.351,-1.6) rot=(0,1,0;3.14159rad)
  LinkedObject = -> Shape004
  Placement = pos=(22.352,-14.351,-1.6) rot=(0,1,0;3.14159rad)
FEATURE [App::Link] __REFERENCE__HTSSOP_28_1EP_44x97mm_P065mm_null_ln_003  label="${REFERENCE}_HTSSOP_28_1EP_44x97mm_P065mm_null004"
  LinkPlacement = pos=(164.761,-64.761,-1.6) rot=(0.707107,-0.707107,0;3.14159rad)
  LinkedObject = -> Shape007
  Placement = pos=(164.761,-64.761,-1.6) rot=(0.707107,-0.707107,0;3.14159rad)
FEATURE [Part::Feature] Shape027  label="${REFERENCE}_CMS04_null"
  Placement = pos=(14.986,-205.74,-1.6) rot=(0.707107,0.707107,0;3.14159rad)
  shape: bbox 2.45 x 4.7 x 1.08 mm, 28 faces, 4 solids (baked)
FEATURE [App::Link] __REFERENCE__SOT_223_null_ln_002  label="${REFERENCE}_SOT_223_null003"
  LinkPlacement = pos=(13.97,-7.366,-1.6) rot=(0.707107,0.707107,0;3.14159rad)
  LinkedObject = -> Shape008
  Placement = pos=(13.97,-7.366,-1.6) rot=(0.707107,0.707107,0;3.14159rad)
FEATURE [App::Part] Bot_7181
  Group = -> [__REFERENCE__R_0805_2012Metric_null_ln_010,__REFERENCE__R_0805_2012Metric_null_ln_011,Shape007,Shape008,__REFERENCE__R_0805_2012Metric_null_ln_012,__REFERENCE__C_0805_2012Metric_null_ln_012,Shape009,Shape010,Shape011,Shape012,__REFERENCE__SOT_223_null_ln_,__REFERENCE__R_0805_2012Metric_null_ln_013,Shape013,__REFERENCE__HTSSOP_28_1EP_44x97mm_P065mm_null_ln_,+43 more]
  Origin = -> Origin004
FEATURE [App::Part] Step_Models_7181
  Group = -> [Top_7181,Bot_7181]
  Origin = -> Origin002
FEATURE [App::Part] Board_7181  label="broadcast_clock"
  Group = -> [Local_CS_7181,Board_Geoms_7181,Step_Models_7181]
  Origin = -> Origin001
